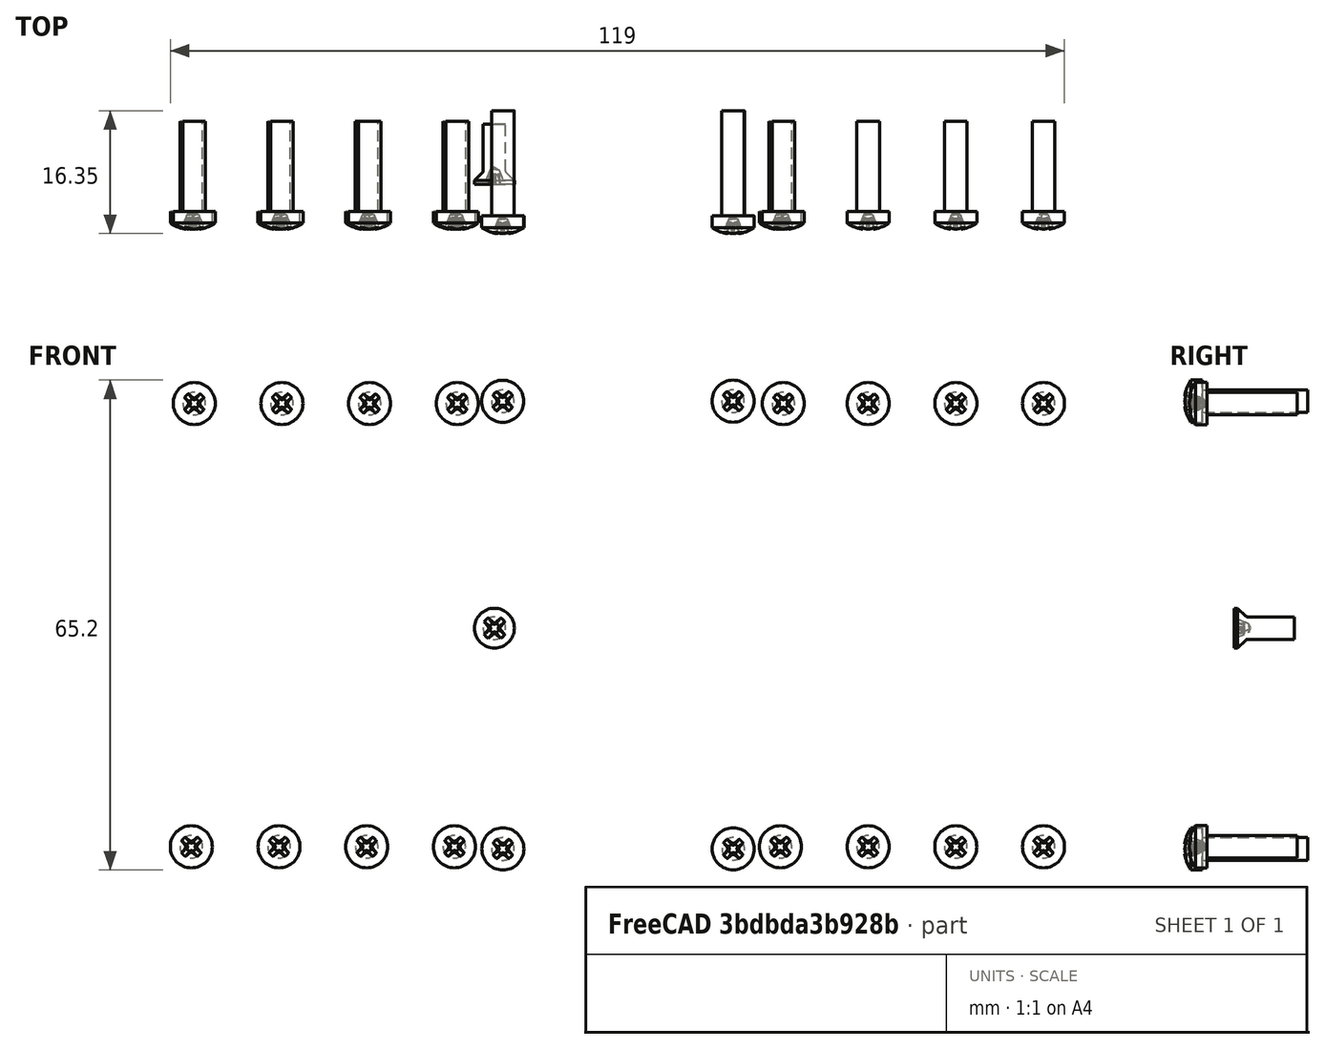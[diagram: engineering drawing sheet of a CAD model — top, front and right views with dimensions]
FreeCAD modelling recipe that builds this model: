
FCSTD DOCUMENT  (FreeCAD 0.19R24291 (Git))
Label: ESC
License: Creative Commons Attribution-NonCommercial-ShareAlike
LicenseURL: http://creativecommons.org/licenses/by-nc-sa/4.0/
objects: Part::FeaturePython×21, App::Link×12, App::DocumentObjectGroup×2, PartDesign::CoordinateSystem×1, App::FeaturePython×1, App::Part×1
note: 22 computed .brp shape members not serialized (recipe doc carries the construction recipe); baked Part::Feature solids carry a one-line shape summary decoded from their .brp
EXTERNAL_REF file=heatsink.FCStd obj=Part
EXTERNAL_REF file=heatsink.FCStd obj=LCS_1
EXTERNAL_REF file=switches.FCStd obj=LCS_0
EXTERNAL_REF file=switches.FCStd obj=Part
EXTERNAL_REF file=busbars.FCStd obj=HoleAxis_7
EXTERNAL_REF file=switches.FCStd obj=HoleAxis_10
EXTERNAL_REF file=busbars.FCStd obj=Body
EXTERNAL_REF file=switches.FCStd obj=HoleAxis_28
EXTERNAL_REF file=busbars.FCStd obj=HoleAxis_6
EXTERNAL_REF file=switches.FCStd obj=HoleAxis_15
EXTERNAL_REF file=busbars.FCStd obj=Body001
EXTERNAL_REF file=switches.FCStd obj=HoleAxis_14
EXTERNAL_REF file=controle.FCStd obj=HoleAxis_1
EXTERNAL_REF file=support1.FCStd obj=HoleAxis_5
EXTERNAL_REF file=controle.FCStd obj=Part
EXTERNAL_REF file=busbars.FCStd obj=HoleAxis_11
EXTERNAL_REF file=caps.FCStd obj=HoleAxis_2
EXTERNAL_REF file=caps.FCStd obj=Part
EXTERNAL_REF file=busbars.FCStd obj=HoleAxis_16
EXTERNAL_REF file=caps.FCStd obj=HoleAxis_4
EXTERNAL_REF file=caps.FCStd obj=HoleAxis_5
EXTERNAL_REF file=caps.FCStd obj=HoleAxis_6
EXTERNAL_REF file=caps.FCStd obj=HoleAxis_7
EXTERNAL_REF file=support1.FCStd obj=HoleAxis_10
EXTERNAL_REF file=support1.FCStd obj=Part
EXTERNAL_REF file=support1.FCStd obj=HoleAxis_11
EXTERNAL_REF file=support1.FCStd obj=HoleAxis_9
EXTERNAL_REF file=support1.FCStd obj=HoleAxis_2
EXTERNAL_REF file=support1.FCStd obj=HoleAxis_1
EXTERNAL_REF file=support1.FCStd obj=HoleAxis_3
EXTERNAL_REF file=support1.FCStd obj=HoleAxis_7
EXTERNAL_REF file=support1.FCStd obj=HoleAxis_4
EXTERNAL_REF file=support1.FCStd obj=HoleAxis_8
EXTERNAL_REF file=controle.FCStd obj=HoleAxis_2
EXTERNAL_REF file=controle.FCStd obj=HoleAxis_3
EXTERNAL_REF file=controle.FCStd obj=HoleAxis_4
EXTERNAL_REF file=busbars.FCStd obj=LCS_0
EXTERNAL_REF file=busbars.FCStd obj=insulator

FEATURE [PartDesign::CoordinateSystem] LCS_Origin
  AttacherType = Attacher::AttachEngine3D
  MapMode = 2
  Support = -> [X_Axis]
FEATURE [App::DocumentObjectGroup] Constraints
FEATURE [App::FeaturePython] Variables  # WARN: FeaturePython — macro-defined, semantics opaque (R4)
FEATURE [App::Link] heatsink_Part
  LinkedObject = -> <external heatsink.FCStd>#Part
FEATURE [App::Link] Switches_Part
  AssemblyType = Asm4EE
  AttachedBy = #LCS_0
  AttachedTo = heatsink_Part#LCS_1
  AttachmentOffset = pos=(87.5,1,0) rot=(-0.57735,-0.57735,-0.57735;2.0944rad)
  LinkPlacement = pos=(-55.0308,-40.4035,87.5) rot=(1,0,0;1.5708rad)
  LinkedObject = -> <external switches.FCStd>#Part
  Placement = pos=(-55.0308,-40.4035,87.5) rot=(1,0,0;1.5708rad)
  expr: Placement = heatsink_Part.Placement * heatsink#LCS_1.Placement * AttachmentOffset * switches#LCS_0.Placement ^ -1
FEATURE [App::Link] busbars_bar1_Body
  AssemblyType = Asm4EE
  AttachedBy = #HoleAxis_7
  AttachedTo = Switches_Part#HoleAxis_10
  AttachmentOffset = pos=(0,0,3) rot=(0,0,1;4.71239rad)
  LinkPlacement = pos=(5.01916,-40.2035,84.31) rot=(-0.57735,-0.57735,0.57735;4.18879rad)
  LinkedObject = -> <external busbars.FCStd>#Body
  Placement = pos=(5.01916,-40.2035,84.31) rot=(-0.57735,-0.57735,0.57735;4.18879rad)
  expr: Placement = Switches_Part.Placement * switches#HoleAxis_10.Placement * AttachmentOffset * busbars#HoleAxis_7.Placement ^ -1
FEATURE [App::Link] busbars_bar1_Body001
  AssemblyType = Asm4EE
  AttachedBy = #HoleAxis_7
  AttachedTo = Switches_Part#HoleAxis_28
  AttachmentOffset = pos=(0,0,3) rot=(0,0,-1;4.71239rad)
  LinkPlacement = pos=(4.91916,-40.2035,15.69) rot=(-0.57735,0.57735,-0.57735;4.18879rad)
  LinkedObject = -> <external busbars.FCStd>#Body
  Placement = pos=(4.91916,-40.2035,15.69) rot=(-0.57735,0.57735,-0.57735;4.18879rad)
  expr: Placement = Switches_Part.Placement * switches#HoleAxis_28.Placement * AttachmentOffset * busbars#HoleAxis_7.Placement ^ -1
FEATURE [App::Link] busbars_bar2_body
  AssemblyType = Asm4EE
  AttachedBy = #HoleAxis_6
  AttachedTo = Switches_Part#HoleAxis_15
  AttachmentOffset = pos=(0,0,3) rot=(0,0,1;4.71239rad)
  LinkPlacement = pos=(-54.6308,-40.2035,79.6) rot=(-0.57735,-0.57735,0.57735;4.18879rad)
  LinkedObject = -> <external busbars.FCStd>#Body001
  Placement = pos=(-54.6308,-40.2035,79.6) rot=(-0.57735,-0.57735,0.57735;4.18879rad)
  expr: Placement = Switches_Part.Placement * switches#HoleAxis_15.Placement * AttachmentOffset * busbars#HoleAxis_6.Placement ^ -1
FEATURE [App::Link] busbars_bar2_body001
  AssemblyType = Asm4EE
  AttachedBy = #HoleAxis_6
  AttachedTo = Switches_Part#HoleAxis_14
  AttachmentOffset = pos=(0,0,3) rot=(0,0,1;1.5708rad)
  LinkPlacement = pos=(64.5692,-40.2035,19.66) rot=(0.57735,-0.57735,0.57735;2.0944rad)
  LinkedObject = -> <external busbars.FCStd>#Body001
  Placement = pos=(64.5692,-40.2035,19.66) rot=(0.57735,-0.57735,0.57735;2.0944rad)
  expr: Placement = Switches_Part.Placement * switches#HoleAxis_14.Placement * AttachmentOffset * busbars#HoleAxis_6.Placement ^ -1
FEATURE [App::Link] Controle_Part
  AssemblyType = Asm4EE
  AttachedBy = #HoleAxis_1
  AttachedTo = support1_Part#HoleAxis_5
  AttachmentOffset = pos=(0.35,0,1.6) rot=(0,0,-1;1.5708rad)
  LinkPlacement = pos=(23.6658,-47.6035,17.45) rot=(-0.57735,0.57735,-0.57735;4.18879rad)
  LinkedObject = -> <external controle.FCStd>#Part
  Placement = pos=(23.6658,-47.6035,17.45) rot=(-0.57735,0.57735,-0.57735;4.18879rad)
  expr: Placement = support1_Part.Placement * support1#HoleAxis_5.Placement * AttachmentOffset * controle#HoleAxis_1.Placement ^ -1
FEATURE [App::Link] Caps_Part
  AssemblyType = Asm4EE
  AttachedBy = #HoleAxis_2
  AttachedTo = busbars_bar1_Body#HoleAxis_11
  AttachmentOffset = pos=(0,0,-1.6) rot=(0,-1,0;3.14159rad)
  LinkPlacement = pos=(-55.0342,-45.0035,12.5) rot=(-0.57735,0.57735,-0.57735;4.18879rad)
  LinkedObject = -> <external caps.FCStd>#Part
  Placement = pos=(-55.0342,-45.0035,12.5) rot=(-0.57735,0.57735,-0.57735;4.18879rad)
  expr: Placement = busbars_bar1_Body.Placement * busbars#HoleAxis_11.Placement * AttachmentOffset * caps#HoleAxis_2.Placement ^ -1
FEATURE [App::Link] Caps_Part001
  AssemblyType = Asm4EE
  AttachedBy = #HoleAxis_4
  AttachedTo = busbars_bar1_Body001#HoleAxis_16
  AttachmentOffset = pos=(0,0,-1.6) rot=(0,-1,0;3.14159rad)
  LinkPlacement = pos=(64.9792,-45.0035,87.5) rot=(0.57735,0.57735,-0.57735;2.0944rad)
  LinkedObject = -> <external caps.FCStd>#Part
  Placement = pos=(64.9792,-45.0035,87.5) rot=(0.57735,0.57735,-0.57735;2.0944rad)
  expr: Placement = busbars_bar1_Body001.Placement * busbars#HoleAxis_16.Placement * AttachmentOffset * caps#HoleAxis_4.Placement ^ -1
FEATURE [Part::FeaturePython] Screw  label="M3x12-Screw1523"  # Fasteners workbench fastener (typed FeaturePython)
  AssemblyType = Asm4EE
  AttachedBy = Origin
  AttachedTo = Caps_Part001#HoleAxis_5
  AttachmentOffset = pos=(0,0,2) rot=(0,0,-1;1.5708rad)
  Placement = pos=(61.4792,-47.0035,79.5) rot=(0,0.707107,-0.707107;3.14159rad)
  diameter = 4
  invert = false
  length = 5
  lengthCustom = 12
  matchOuter = false
  offset = 0
  thread = false
  type = 34
  expr: Placement = Caps_Part001.Placement * caps#HoleAxis_5.Placement * AttachmentOffset
FEATURE [Part::FeaturePython] Screw001  label="M3x12-Screw"  # Fasteners workbench fastener (typed FeaturePython)
  AssemblyType = Asm4EE
  AttachedBy = Origin
  AttachedTo = Caps_Part001#HoleAxis_6
  AttachmentOffset = pos=(0,0,2) rot=(0,0,1;0rad)
  Placement = pos=(49.8125,-47.0035,79.5) rot=(0.57735,0.57735,-0.57735;2.0944rad)
  diameter = 4
  invert = false
  length = 5
  lengthCustom = 12
  matchOuter = false
  offset = 0
  thread = false
  type = 34
  expr: Placement = Caps_Part001.Placement * caps#HoleAxis_6.Placement * AttachmentOffset
FEATURE [Part::FeaturePython] Screw002  label="M3x12-Screw1524"  # Fasteners workbench fastener (typed FeaturePython)
  AssemblyType = Asm4EE
  AttachedBy = Origin
  AttachedTo = Caps_Part001#HoleAxis_7
  AttachmentOffset = pos=(0,0,2) rot=(0,0,1;0rad)
  Placement = pos=(38.1458,-47.0035,79.5) rot=(0.57735,0.57735,-0.57735;2.0944rad)
  diameter = 4
  invert = false
  length = 5
  lengthCustom = 12
  matchOuter = false
  offset = 0
  thread = false
  type = 34
  expr: Placement = Caps_Part001.Placement * caps#HoleAxis_7.Placement * AttachmentOffset
FEATURE [App::Link] support1_Part
  AssemblyType = Asm4EE
  AttachedBy = #HoleAxis_1
  AttachedTo = Caps_Part#HoleAxis_4
  AttachmentOffset = pos=(0,0,2) rot=(0,0,1;1.5708rad)
  LinkPlacement = pos=(-12.8342,-47.0035,89.5) rot=(0,0.707107,-0.707107;3.14159rad)
  LinkedObject = -> <external support1.FCStd>#Part
  Placement = pos=(-12.8342,-47.0035,89.5) rot=(0,0.707107,-0.707107;3.14159rad)
  expr: Placement = Caps_Part.Placement * caps#HoleAxis_4.Placement * AttachmentOffset * support1#HoleAxis_10.Placement ^ -1
FEATURE [App::Link] support1_Part001
  AssemblyType = Asm4EE
  AttachedBy = #HoleAxis_10
  AttachedTo = Caps_Part001#HoleAxis_4
  AttachmentOffset = pos=(0,0,2) rot=(0,0,1;1.5708rad)
  LinkPlacement = pos=(22.7792,-47.0035,10.5) rot=(1,0,0;1.5708rad)
  LinkedObject = -> <external support1.FCStd>#Part
  Placement = pos=(22.7792,-47.0035,10.5) rot=(1,0,0;1.5708rad)
  expr: Placement = Caps_Part001.Placement * caps#HoleAxis_4.Placement * AttachmentOffset * support1#HoleAxis_10.Placement ^ -1
FEATURE [Part::FeaturePython] Screw005  label="M3x12-Screw1536"  # Fasteners workbench fastener (typed FeaturePython)
  AssemblyType = Asm4EE
  AttachedBy = Origin
  AttachedTo = support1_Part#HoleAxis_11
  Placement = pos=(-51.5342,-47.0035,79.5) rot=(0,0.707107,-0.707107;3.14159rad)
  diameter = 4
  invert = false
  length = 5
  lengthCustom = 12
  matchOuter = false
  offset = 0
  thread = false
  type = 34
  expr: Placement = support1_Part.Placement * support1#HoleAxis_11.Placement * AttachmentOffset
FEATURE [Part::FeaturePython] Screw006  label="M3x12-Screw1533"  # Fasteners workbench fastener (typed FeaturePython)
  AssemblyType = Asm4EE
  AttachedBy = Origin
  AttachedTo = support1_Part#HoleAxis_9
  Placement = pos=(-16.5242,-47.0035,79.5) rot=(0,0.707107,-0.707107;3.14159rad)
  diameter = 4
  invert = false
  length = 5
  lengthCustom = 12
  matchOuter = false
  offset = 0
  thread = false
  type = 34
  expr: Placement = support1_Part.Placement * support1#HoleAxis_9.Placement * AttachmentOffset
FEATURE [Part::FeaturePython] Screw007  label="M3x12-Screw1530"  # Fasteners workbench fastener (typed FeaturePython)
  AssemblyType = Asm4EE
  AttachedBy = Origin
  AttachedTo = support1_Part001#HoleAxis_2
  Placement = pos=(-40.2508,-47.0035,20.5) rot=(1,0,0;1.5708rad)
  diameter = 4
  invert = false
  length = 5
  lengthCustom = 12
  matchOuter = false
  offset = 0
  thread = false
  type = 34
  expr: Placement = support1_Part001.Placement * support1#HoleAxis_2.Placement * AttachmentOffset
FEATURE [Part::FeaturePython] Screw008  label="M3x12-Screw1531"  # Fasteners workbench fastener (typed FeaturePython)
  AssemblyType = Asm4EE
  AttachedBy = Origin
  AttachedTo = support1_Part001#HoleAxis_1
  Placement = pos=(-51.9208,-47.0035,20.5) rot=(1,0,0;1.5708rad)
  diameter = 4
  invert = false
  length = 5
  lengthCustom = 12
  matchOuter = false
  offset = 0
  thread = false
  type = 34
  expr: Placement = support1_Part001.Placement * support1#HoleAxis_1.Placement * AttachmentOffset
FEATURE [Part::FeaturePython] Screw009  label="M3x12-Screw1525"  # Fasteners workbench fastener (typed FeaturePython)
  AssemblyType = Asm4EE
  AttachedBy = Origin
  AttachedTo = support1_Part001#HoleAxis_3
  Placement = pos=(-28.5808,-47.0035,20.5) rot=(1,0,0;1.5708rad)
  diameter = 4
  invert = false
  length = 5
  lengthCustom = 12
  matchOuter = false
  offset = 0
  thread = false
  type = 34
  expr: Placement = support1_Part001.Placement * support1#HoleAxis_3.Placement * AttachmentOffset
FEATURE [Part::FeaturePython] Screw010  label="M3x12-Screw1537"  # Fasteners workbench fastener (typed FeaturePython)
  AssemblyType = Asm4EE
  AttachedBy = Origin
  AttachedTo = support1_Part#HoleAxis_7
  Placement = pos=(-28.1942,-47.0035,79.5) rot=(0.57735,0.57735,-0.57735;2.0944rad)
  diameter = 4
  invert = false
  length = 5
  lengthCustom = 12
  matchOuter = false
  offset = 0
  thread = false
  type = 34
  expr: Placement = support1_Part.Placement * support1#HoleAxis_7.Placement * AttachmentOffset
FEATURE [Part::FeaturePython] Screw011  label="M3x12-Screw1532"  # Fasteners workbench fastener (typed FeaturePython)
  AssemblyType = Asm4EE
  AttachedBy = Origin
  AttachedTo = support1_Part001#HoleAxis_4
  Placement = pos=(-16.9108,-47.0035,20.5) rot=(1,0,0;1.5708rad)
  diameter = 4
  invert = false
  length = 5
  lengthCustom = 12
  matchOuter = false
  offset = 0
  thread = false
  type = 34
  expr: Placement = support1_Part001.Placement * support1#HoleAxis_4.Placement * AttachmentOffset
FEATURE [Part::FeaturePython] Screw012  label="M3x12-Screw1527"  # Fasteners workbench fastener (typed FeaturePython)
  AssemblyType = Asm4EE
  AttachedBy = Origin
  AttachedTo = support1_Part001#HoleAxis_7
  Placement = pos=(38.1392,-47.0035,20.5) rot=(0.57735,-0.57735,0.57735;2.0944rad)
  diameter = 4
  invert = false
  length = 5
  lengthCustom = 12
  matchOuter = false
  offset = 0
  thread = false
  type = 34
  expr: Placement = support1_Part001.Placement * support1#HoleAxis_7.Placement * AttachmentOffset
FEATURE [Part::FeaturePython] Screw013  label="M3x12-Screw1526"  # Fasteners workbench fastener (typed FeaturePython)
  AssemblyType = Asm4EE
  AttachedBy = Origin
  AttachedTo = support1_Part001#HoleAxis_8
  Placement = pos=(49.8092,-47.0035,20.5) rot=(1,0,0;1.5708rad)
  diameter = 4
  invert = false
  length = 5
  lengthCustom = 12
  matchOuter = false
  offset = 0
  thread = false
  type = 34
  expr: Placement = support1_Part001.Placement * support1#HoleAxis_8.Placement * AttachmentOffset
FEATURE [Part::FeaturePython] Screw014  label="M3x12-Screw1535"  # Fasteners workbench fastener (typed FeaturePython)
  AssemblyType = Asm4EE
  AttachedBy = Origin
  AttachedTo = support1_Part#HoleAxis_8
  Placement = pos=(-39.8642,-47.0035,79.5) rot=(0,0.707107,-0.707107;3.14159rad)
  diameter = 4
  invert = false
  length = 5
  lengthCustom = 12
  matchOuter = false
  offset = 0
  thread = false
  type = 34
  expr: Placement = support1_Part.Placement * support1#HoleAxis_8.Placement * AttachmentOffset
FEATURE [Part::FeaturePython] Screw015  label="M3x12-Screw1528"  # Fasteners workbench fastener (typed FeaturePython)
  AssemblyType = Asm4EE
  AttachedBy = Origin
  AttachedTo = support1_Part001#HoleAxis_9
  Placement = pos=(26.4692,-47.0035,20.5) rot=(1,0,0;1.5708rad)
  diameter = 4
  invert = false
  length = 5
  lengthCustom = 12
  matchOuter = false
  offset = 0
  thread = false
  type = 34
  expr: Placement = support1_Part001.Placement * support1#HoleAxis_9.Placement * AttachmentOffset
FEATURE [Part::FeaturePython] Screw016  label="M3x12-Screw1529"  # Fasteners workbench fastener (typed FeaturePython)
  AssemblyType = Asm4EE
  AttachedBy = Origin
  AttachedTo = support1_Part001#HoleAxis_11
  Placement = pos=(61.4792,-47.0035,20.5) rot=(1,0,0;1.5708rad)
  diameter = 4
  invert = false
  length = 5
  lengthCustom = 12
  matchOuter = false
  offset = 0
  thread = false
  type = 34
  expr: Placement = support1_Part001.Placement * support1#HoleAxis_11.Placement * AttachmentOffset
FEATURE [Part::FeaturePython] Screw017  label="M3x12-Screw1534"  # Fasteners workbench fastener (typed FeaturePython)
  AssemblyType = Asm4EE
  AttachedBy = Origin
  AttachedTo = support1_Part#HoleAxis_4
  Placement = pos=(26.8558,-47.0035,79.5) rot=(0,0.707107,-0.707107;3.14159rad)
  diameter = 4
  invert = false
  length = 5
  lengthCustom = 12
  matchOuter = false
  offset = 0
  thread = false
  type = 34
  expr: Placement = support1_Part.Placement * support1#HoleAxis_4.Placement * AttachmentOffset
FEATURE [Part::FeaturePython] Screw018  label="M3x14-Screw"  # Fasteners workbench fastener (typed FeaturePython)
  AssemblyType = Asm4EE
  AttachedBy = Origin
  AttachedTo = Controle_Part#HoleAxis_1
  Placement = pos=(-10.4842,-47.6035,79.8) rot=(-0.57735,0.57735,-0.57735;4.18879rad)
  diameter = 4
  invert = false
  length = 6
  lengthCustom = 14
  matchOuter = false
  offset = 0
  thread = false
  type = 34
  expr: Placement = Controle_Part.Placement * controle#HoleAxis_1.Placement * AttachmentOffset
FEATURE [Part::FeaturePython] Screw019  label="M3x14-Screw118"  # Fasteners workbench fastener (typed FeaturePython)
  AssemblyType = Asm4EE
  AttachedBy = Origin
  AttachedTo = Controle_Part#HoleAxis_2
  Placement = pos=(-10.4608,-47.6035,20.2104) rot=(-0.57735,0.57735,-0.57735;4.18879rad)
  diameter = 4
  invert = false
  length = 6
  lengthCustom = 14
  matchOuter = false
  offset = 0
  thread = false
  type = 34
  expr: Placement = Controle_Part.Placement * controle#HoleAxis_2.Placement * AttachmentOffset
FEATURE [Part::FeaturePython] Screw020  label="M3x14-Screw119"  # Fasteners workbench fastener (typed FeaturePython)
  AssemblyType = Asm4EE
  AttachedBy = Origin
  AttachedTo = Controle_Part#HoleAxis_3
  Placement = pos=(20.1898,-47.6035,20.2235) rot=(-0.57735,0.57735,-0.57735;4.18879rad)
  diameter = 4
  invert = false
  length = 6
  lengthCustom = 14
  matchOuter = false
  offset = 0
  thread = false
  type = 34
  expr: Placement = Controle_Part.Placement * controle#HoleAxis_3.Placement * AttachmentOffset
FEATURE [Part::FeaturePython] Screw021  label="M3x14-Screw120"  # Fasteners workbench fastener (typed FeaturePython)
  AssemblyType = Asm4EE
  AttachedBy = Origin
  AttachedTo = Controle_Part#HoleAxis_4
  Placement = pos=(20.1658,-47.6035,79.8121) rot=(-0.57735,0.57735,-0.57735;4.18879rad)
  diameter = 4
  invert = false
  length = 6
  lengthCustom = 14
  matchOuter = false
  offset = 0
  thread = false
  type = 34
  expr: Placement = Controle_Part.Placement * controle#HoleAxis_4.Placement * AttachmentOffset
FEATURE [App::Link] busbars_insulator
  AssemblyType = Asm4EE
  AttachedBy = #LCS_0
  AttachedTo = busbars_bar2_body#HoleAxis_6
  AttachmentOffset = pos=(0,0,-2) rot=(0,0,1;0rad)
  LinkPlacement = pos=(-11.5808,-41.4035,49.6) rot=(-0.57735,-0.57735,0.57735;4.18879rad)
  LinkedObject = -> <external busbars.FCStd>#insulator
  Placement = pos=(-11.5808,-41.4035,49.6) rot=(-0.57735,-0.57735,0.57735;4.18879rad)
  expr: Placement = busbars_bar2_body.Placement * busbars#HoleAxis_6.Placement * AttachmentOffset * busbars#LCS_0.Placement ^ -1
FEATURE [Part::FeaturePython] Screw022  label="M3x8-Screw"  # Fasteners workbench fastener (typed FeaturePython)
  AssemblyType = Asm4EE
  AttachedBy = Origin
  AttachedTo = busbars_bar2_body#HoleAxis_6
  Placement = pos=(-11.5808,-43.4035,49.6) rot=(-0.57735,-0.57735,0.57735;4.18879rad)
  diameter = 4
  invert = false
  length = 3
  lengthCustom = 8
  matchOuter = false
  offset = 0
  thread = false
  type = 35
  expr: Placement = busbars_bar2_body.Placement * busbars#HoleAxis_6.Placement * AttachmentOffset
FEATURE [App::DocumentObjectGroup] Group  label="Screws"
  Group = -> [Screw016,Screw015,Screw013,Screw012,Screw011,Screw009,Screw007,Screw008,Screw005,Screw014,Screw006,Screw010,Screw017,Screw,Screw002,Screw001,Screw018,Screw019,Screw020,Screw021,Screw022]
FEATURE [App::Part] Model
  Configuration = 0
  Group = -> [LCS_Origin,Constraints,Variables,heatsink_Part,Switches_Part,busbars_bar1_Body,busbars_bar1_Body001,busbars_bar2_body,busbars_bar2_body001,Controle_Part,Caps_Part,Caps_Part001,support1_Part,support1_Part001,Screw001,Screw,Screw002,Screw006,Screw009,Screw013,Screw012,Screw015,Screw016,Screw017,Screw007,Screw014,Screw005,Screw010,Screw008,Screw011,Group,Screw018,Screw019,Screw020,Screw021,+2 more]
  Origin = -> Origin
  Placement = pos=(0,0,0) rot=(1,0,0;-1.5708rad)
  Type = Assembly4 Model

RESOLVED EXTERNAL PARTS (link-assembly join: the EXTERNAL_REF files above that resolve inside this repo's crawl, each included once):
---- part busbars.FCStd = doc fcstd_a403adba0c2a ----
FCSTD DOCUMENT  (FreeCAD 0.19R24291 (Git))
Label: busbars
License: All rights reserved
LicenseURL: http://en.wikipedia.org/wiki/All_rights_reserved
objects: TechDraw::DrawViewDimension×44, Part::Cylinder×18, PartDesign::Line×18, Part::Fuse×7, TechDraw::DrawProjGroupItem×6, Part::Box×5, Part::Cut×5, Part::MultiFuse×4, Sketcher::SketchObject×3, PartDesign::CoordinateSystem×3, PartDesign::Hole×3, PartDesign::Body×3, Part::Part2DObjectPython×2, PartDesign::Pad×2, TechDraw::DrawProjGroup×2, App::DocumentObjectGroup×2, TechDraw::DrawViewPart×2, Part::FeaturePython×2, Part::Mirroring×1, TechDraw::DrawSVGTemplate×1, +4 more types
note: 82 computed .brp shape members not serialized (recipe doc carries the construction recipe); baked Part::Feature solids carry a one-line shape summary decoded from their .brp

FEATURE [Part::Box] cube
  AttacherType = Attacher::AttachEngine3D
  Height = 3
  Length = 10
  Width = 60
FEATURE [Part::Cylinder] cylinder
  Angle = 360
  AttacherType = Attacher::AttachEngine3D
  Height = 5
  Placement = pos=(4.81,56.54,-1) rot=(0,0,1;0rad)
  Radius = 1.6
FEATURE [Part::Cylinder] cylinder001
  Angle = 360
  AttacherType = Attacher::AttachEngine3D
  Height = 5
  Placement = pos=(4.81,44.87,-1) rot=(0,0,1;0rad)
  Radius = 1.6
FEATURE [Part::Cylinder] cylinder002
  Angle = 360
  AttacherType = Attacher::AttachEngine3D
  Height = 5
  Placement = pos=(4.81,33.2,-1) rot=(0,0,1;0rad)
  Radius = 1.6
FEATURE [Part::Cylinder] cylinder003
  Angle = 360
  AttacherType = Attacher::AttachEngine3D
  Height = 5
  Placement = pos=(4.81,21.53,-1) rot=(0,0,1;0rad)
  Radius = 1.6
FEATURE [Part::MultiFuse] Group
  Shapes = -> [cylinder,cylinder001,cylinder002,cylinder003]
FEATURE [Part::Cylinder] cylinder004
  Angle = 360
  AttacherType = Attacher::AttachEngine3D
  Height = 5
  Placement = pos=(4.52,15.3,-1) rot=(0,0,1;0rad)
  Radius = 1.6
FEATURE [Part::Fuse] union
  Base = -> Group
  Tool = -> cylinder004
FEATURE [Part::Cut] difference
  Base = -> cube
  Tool = -> union
FEATURE [Part::Box] cube001
  AttacherType = Attacher::AttachEngine3D
  Height = 3
  Length = 10
  Width = 60
FEATURE [Part::Cylinder] cylinder005 .. cylinder008  x4 (patterned run collapsed; names and placements below)
  Angle = 360
  AttacherType = Attacher::AttachEngine3D
  Height = 5
  Radius = 1.6
  placements: 4 in arithmetic series — first pos=(4.81,56.54,-1) rot=(0,0,1;0rad), step (0,-11.67,0), last pos=(4.81,21.53,-1) rot=(0,0,1;0rad)
FEATURE [Part::MultiFuse] Group001
  Shapes = -> [cylinder005,cylinder006,cylinder007,cylinder008]
FEATURE [Part::Cylinder] cylinder009
  Angle = 360
  AttacherType = Attacher::AttachEngine3D
  Height = 5
  Placement = pos=(4.52,15.3,-1) rot=(0,0,1;0rad)
  Radius = 1.6
FEATURE [Part::Fuse] union001
  Base = -> Group001
  Tool = -> cylinder009
FEATURE [Part::Cut] difference001
  Base = -> cube001
  Tool = -> union001
FEATURE [Part::Mirroring] mirr_difference001  label="mirrored difference001"
  Base = (0,0,0)
  Normal = (0,1,0)
  Source = -> difference001
FEATURE [Part::Fuse] Group002
  Base = -> difference
  Tool = -> mirr_difference001
FEATURE [Part::Box] cube002
  AttacherType = Attacher::AttachEngine3D
  Height = 3
  Length = 10
  Placement = pos=(0,-80,0) rot=(0,0,1;0rad)
  Width = 20
FEATURE [Part::Cylinder] cylinder010
  Angle = 360
  AttacherType = Attacher::AttachEngine3D
  Height = 5
  Placement = pos=(5,-76,-1) rot=(0,0,1;0rad)
  Radius = 2.1
FEATURE [Part::Cylinder] cylinder011
  Angle = 360
  AttacherType = Attacher::AttachEngine3D
  Height = 5
  Placement = pos=(5,-68,-1) rot=(0,0,1;0rad)
  Radius = 2.1
FEATURE [Part::Fuse] union002
  Base = -> cylinder010
  Tool = -> cylinder011
FEATURE [Part::Cut] difference002
  Base = -> cube002
  Tool = -> union002
FEATURE [Part::Fuse] union003  label="bar1_fromOpenScad"
  Base = -> Group002
  Tool = -> difference002
FEATURE [Part::Box] cube003
  AttacherType = Attacher::AttachEngine3D
  Height = 3
  Length = 10
  Width = 60
FEATURE [Part::Cylinder] cylinder012 .. cylinder015  x4 (patterned run collapsed; names and placements below)
  Angle = 360
  AttacherType = Attacher::AttachEngine3D
  Height = 5
  Radius = 1.6
  placements: 4 in arithmetic series — first pos=(5,8.86,-1) rot=(0,0,1;0rad), step (0,13.8925,0), last pos=(5,50.5375,-1) rot=(0,0,1;0rad)
FEATURE [Part::MultiFuse] Group003
  Shapes = -> [cylinder012,cylinder013,cylinder014,cylinder015]
FEATURE [Part::Cut] difference003
  Base = -> cube003
  Tool = -> Group003
FEATURE [Part::Box] cube004
  AttacherType = Attacher::AttachEngine3D
  Height = 3
  Length = 10
  Placement = pos=(0,-20,0) rot=(0,0,1;0rad)
  Width = 20
FEATURE [Part::Cylinder] cylinder016
  Angle = 360
  AttacherType = Attacher::AttachEngine3D
  Height = 5
  Placement = pos=(5,-16,-1) rot=(0,0,1;0rad)
  Radius = 2.1
FEATURE [Part::Cylinder] cylinder017
  Angle = 360
  AttacherType = Attacher::AttachEngine3D
  Height = 5
  Placement = pos=(5,-8,-1) rot=(0,0,1;0rad)
  Radius = 2.1
FEATURE [Part::Fuse] union004
  Base = -> cylinder016
  Tool = -> cylinder017
FEATURE [Part::Cut] difference004
  Base = -> cube004
  Tool = -> union004
FEATURE [Part::Fuse] union005  label="bar2_fromOpenScad"
  Base = -> difference003
  Placement = pos=(25,0,0) rot=(0,0,1;0rad)
  Tool = -> difference004
FEATURE [TechDraw::DrawSVGTemplate] Template
  EditableTexts = APPROVER_NAME=APPROVER NAME,AUTHOR_NAME=AUTHOR NAME,DATE=YYYY-MM-DD,DN=DN,DOCUMENT_TYPE=Mechanical assembly drawing,OWNER_NAME=OWNER NAME,PM=PM,PN=PN,+7 more (map truncated)
  Height = 297
  Orientation = 1
  Width = 420
FEATURE [Part::Part2DObjectPython] Shape2DView  label="bar1_Shape2DView"  # Draft 2D object (typed FeaturePython)
  Base = -> union003
  FuseArch = false
  HiddenLines = false
  InPlace = true
  Projection = (0,0,1)
  ProjectionMode = 0
  SegmentLength = 0.05
  Tessellation = false
  VisibleOnly = false
FEATURE [Sketcher::SketchObject] Sketch  label="bar1_Sketch"
  FullyConstrained = true
  expr: Constraints[47] = Spreadsheet.varH
  expr: Constraints[46] = 2 * Spreadsheet.tab / 5
  expr: Constraints[33] = Spreadsheet.varA
  expr: Constraints[20] = Spreadsheet.varD
  expr: Constraints[45] = Spreadsheet.tab / 5
  expr: Constraints[34] = Spreadsheet.varA
  expr: Constraints[36] = Spreadsheet.varC
  expr: Constraints[41] = Spreadsheet.varE
  expr: Constraints[40] = Spreadsheet.varE
  expr: Constraints[39] = Spreadsheet.varD
  expr: Constraints[37] = Spreadsheet.varC
  expr: Constraints[35] = Spreadsheet.varA
  expr: Constraints[31] = Spreadsheet.varA
  expr: Constraints[25] = Spreadsheet.lenght1
  expr: Constraints[28] = Spreadsheet.varC
  expr: Constraints[30] = Spreadsheet.varA
  expr: Constraints[8] = Spreadsheet.hole2_diameter
  expr: Constraints[44] = Spreadsheet.width / 2
  expr: Constraints[19] = Spreadsheet.varA
  expr: Constraints[42] = Spreadsheet.varB
  expr: Constraints[7] = Spreadsheet.hole2_diameter
  expr: Constraints[43] = Spreadsheet.width / 2
  expr: Constraints[27] = Spreadsheet.varC
  expr: Constraints[9] = Spreadsheet.hole1_diameter
  expr: Constraints[32] = Spreadsheet.varA
  expr: Constraints[26] = Spreadsheet.varC
  expr: Constraints[3] = Spreadsheet.width
  expr: Constraints[29] = Spreadsheet.varA
  expr: Constraints[38] = Spreadsheet.varC
  sketch-geometry (16):
    g0: LineSegment StartX=0 StartY=60 StartZ=0 EndX=10 EndY=60 EndZ=0
    g1: Circle CenterX=4.52 CenterY=15.32 CenterZ=0 NormalX=0 NormalY=0 NormalZ=1 AngleXU=0 Radius=2
    g2: Circle CenterX=4.81 CenterY=21.54 CenterZ=0 NormalX=0 NormalY=0 NormalZ=1 AngleXU=0 Radius=2
    g3: Circle CenterX=4.81 CenterY=33.21 CenterZ=0 NormalX=0 NormalY=0 NormalZ=1 AngleXU=0 Radius=2
    g4: Circle CenterX=4.81 CenterY=44.88 CenterZ=0 NormalX=0 NormalY=0 NormalZ=1 AngleXU=0 Radius=2
    g5: Circle CenterX=4.81 CenterY=56.55 CenterZ=0 NormalX=0 NormalY=0 NormalZ=1 AngleXU=0 Radius=2
    g6: Circle CenterX=4.52 CenterY=-15.33 CenterZ=0 NormalX=0 NormalY=0 NormalZ=-1 AngleXU=-3.14159 Radius=2
    g7: Circle CenterX=4.81 CenterY=-21.55 CenterZ=0 NormalX=0 NormalY=0 NormalZ=-1 AngleXU=-3.14159 Radius=2
    g8: Circle CenterX=4.81 CenterY=-33.22 CenterZ=0 NormalX=0 NormalY=0 NormalZ=-1 AngleXU=-3.14159 Radius=2
    g9: Circle CenterX=4.81 CenterY=-44.89 CenterZ=0 NormalX=0 NormalY=0 NormalZ=-1 AngleXU=-3.14159 Radius=2
    g10: Circle CenterX=4.81 CenterY=-56.56 CenterZ=0 NormalX=0 NormalY=0 NormalZ=-1 AngleXU=-3.14159 Radius=2
    g11: LineSegment StartX=0 StartY=-80 StartZ=0 EndX=10 EndY=-80 EndZ=0
    g12: Circle CenterX=5 CenterY=-76 CenterZ=0 NormalX=0 NormalY=0 NormalZ=1 AngleXU=0 Radius=2.1
    g13: Circle CenterX=5 CenterY=-68 CenterZ=0 NormalX=0 NormalY=0 NormalZ=1 AngleXU=0 Radius=2.1
    g14: LineSegment StartX=0 StartY=60 StartZ=0 EndX=0 EndY=-80 EndZ=0
    g15: LineSegment StartX=10 StartY=-80 StartZ=0 EndX=10 EndY=60 EndZ=0
  constraints (50):
    c: Horizontal(g11)
    c: Horizontal(g0)
    c: Vertical(g14)
    c: Distance(g11) = 10
    c: Coincident(g11,g14)
    c: DistanceX(g11) = 0
    c: DistanceY(g11) = -80
    c: Diameter(g12) = 4.2
    c: Diameter(g13) = 4.2
    c: Diameter(g10) = 4
    c: Equal(g5,g4)
    c: Equal(g4,g3)
    c: Equal(g3,g2)
    c: Equal(g2,g1)
    c: Equal(g1,g7)
    c: Equal(g7,g6)
    c: Equal(g6,g8)
    c: Equal(g8,g10)
    c: Equal(g9,g10)
    c: Distance(g9,g14) = 4.81
    c: Distance(g6,g14) = 4.52
    c: Vertical(g15)
    c: Coincident(g0,g14)
    c: Coincident(g0,g15)
    c: Coincident(g15,g11)
    c: DistanceY(g11,g0) = 140
    c: DistanceY(g10,g9) = 11.67
    c: DistanceY(g9,g8) = 11.67
    c: DistanceY(g8,g7) = 11.67
    c: Distance(g10,g14) = 4.81
    c: Distance(g8,g14) = 4.81
    c: Distance(g7,g14) = 4.81
    c: Distance(g2,g14) = 4.81
    c: Distance(g3,g14) = 4.81
    c: Distance(g4,g14) = 4.81
    c: Distance(g5,g14) = 4.81
    c: DistanceY(g2,g3) = 11.67
    c: DistanceY(g3,g4) = 11.67
    c: DistanceY(g4,g5) = 11.67
    c: Distance(g1,g14) = 4.52
    c: DistanceY(g7,g6) = 6.22
    c: DistanceY(g1,g2) = 6.22
    c: Distance(g5,g0) = 3.45
    c: Distance(g12,g14) = 5
    c: Distance(g13,g14) = 5
    c: Distance(g12,g11) = 4
    c: DistanceY(g12,g13) = 8
    c: DistanceY(g6,g1) = 30.65
    c: Distance(g10,g11) = 23.44
    c: DistanceY(g13,g10) = 11.44
FEATURE [Part::Part2DObjectPython] Shape2DView001  label="bar2_Shape2DView"  # Draft 2D object (typed FeaturePython)
  Base = -> union005
  FuseArch = false
  HiddenLines = false
  InPlace = true
  Projection = (0,0,1)
  ProjectionMode = 0
  SegmentLength = 0.05
  Tessellation = false
  VisibleOnly = false
FEATURE [Sketcher::SketchObject] Sketch001  label="bar2_Sketch"
  FullyConstrained = true
  expr: Constraints[29] = Spreadsheet.varG
  expr: Constraints[26] = Spreadsheet.width / 2
  expr: Constraints[24] = Spreadsheet.width / 2
  expr: Constraints[28] = Spreadsheet.varG
  expr: Constraints[25] = Spreadsheet.width / 2
  expr: Constraints[21] = Spreadsheet.hole1_diameter
  expr: Constraints[23] = Spreadsheet.width / 2
  expr: Constraints[19] = Spreadsheet.hole1_diameter
  expr: Constraints[18] = Spreadsheet.hole1_diameter
  expr: Constraints[20] = Spreadsheet.hole1_diameter
  expr: Constraints[15] = Spreadsheet.width / 2
  expr: Constraints[13] = 2 * Spreadsheet.tab / 5
  expr: Constraints[12] = Spreadsheet.tab / 5
  expr: Constraints[22] = Spreadsheet.varF
  expr: Constraints[14] = Spreadsheet.width / 2
  expr: Constraints[17] = Spreadsheet.hole2_diameter
  expr: Constraints[9] = Spreadsheet.length2
  expr: Constraints[27] = Spreadsheet.varG
  expr: Constraints[16] = Spreadsheet.hole2_diameter
  expr: Constraints[8] = Spreadsheet.width
  sketch-geometry (10):
    g0: LineSegment StartX=25 StartY=47.5 StartZ=0 EndX=35 EndY=47.5 EndZ=0
    g1: Circle CenterX=30 CenterY=4.05 CenterZ=0 NormalX=0 NormalY=0 NormalZ=1 AngleXU=0 Radius=2
    g2: Circle CenterX=30 CenterY=17.05 CenterZ=0 NormalX=0 NormalY=0 NormalZ=1 AngleXU=0 Radius=2
    g3: Circle CenterX=30 CenterY=30.05 CenterZ=0 NormalX=0 NormalY=0 NormalZ=1 AngleXU=0 Radius=2
    g4: Circle CenterX=30 CenterY=43.05 CenterZ=0 NormalX=0 NormalY=0 NormalZ=1 AngleXU=0 Radius=2
    g5: LineSegment StartX=25 StartY=-20 StartZ=0 EndX=35 EndY=-20 EndZ=0
    g6: Circle CenterX=30 CenterY=-16 CenterZ=0 NormalX=0 NormalY=0 NormalZ=1 AngleXU=0 Radius=2.1
    g7: Circle CenterX=30 CenterY=-8 CenterZ=0 NormalX=0 NormalY=0 NormalZ=1 AngleXU=0 Radius=2.1
    g8: LineSegment StartX=35 StartY=-20 StartZ=0 EndX=35 EndY=47.5 EndZ=0
    g9: LineSegment StartX=25 StartY=47.5 StartZ=0 EndX=25 EndY=-20 EndZ=0
  constraints (32):
    c: Coincident(g8,g0)
    c: Coincident(g0,g9)
    c: Coincident(g9,g5)
    c: Coincident(g5,g8)
    c: Vertical(g8)
    c: Vertical(g9)
    c: Horizontal(g5)
    c: Horizontal(g0)
    c: Distance(g5) = 10
    c: Distance(g9) = 67.5
    c: DistanceX(g5) = 25
    c: DistanceY(g5) = -20
    c: Distance(g6,g5) = 4
    c: DistanceY(g6,g7) = 8
    c: Distance(g7,g9) = 5
    c: Distance(g6,g9) = 5
    c: Diameter(g7) = 4.2
    c: Diameter(g6) = 4.2
    c: Diameter(g1) = 4
    c: Diameter(g2) = 4
    c: Diameter(g3) = 4
    c: Diameter(g4) = 4
    c: Distance(g4,g0) = 4.45
    c: Distance(g1,g9) = 5
    c: Distance(g2,g9) = 5
    c: Distance(g4,g9) = 5
    c: Distance(g3,g9) = 5
    c: Distance(g4,g3) = 13
    c: Distance(g3,g2) = 13
    c: Distance(g1,g2) = 13
    c: Distance(g1,g5) = 24.05
    c: Distance(g7,g1) = 12.05
FEATURE [Spreadsheet::Sheet] Spreadsheet  label="Dimensions"
  cells = A1=Parameter; B1=Value; C1=Description; A2=L1; B2(lenght1)==120mm + tab; C2=Comprimento da barra 1; A3=L2; B3(length2)==50mm + tab - 2.5mm; C3=Comprimento da barra 2; A4=W; B4(width)==10mm; C4=Largura das barras; A5=T; B5(thickness)==3.2mm; C5=Espessura das barras; A6=H1; B6(hole1_diameter)==4mm; C6=Diâmetro interno do furo sem rosca; A7=H2; B7(hole2_diameter)==4.2mm; C7=Furo com rosca M5; A8=A; B8(varA)==4.81mm; C8=Distância entre a borda lateral da barra e centro do furo; A9=B; B9(varB)==3.45mm; A10=C; B10(varC)==11.67mm; A11=D; B11(varD)==4.52mm; C11=Distância entre a borda lateral da barra e centro do furo; A12=E; B12(varE)==6.22mm; A13=F; B13(varF)==4.45mm; C13=Distância entre a borda frontal da barra e centro do furo; A14=G; B14(varG)==13mm; A15=H; B15(varH)==30.65mm; A16=Tab; B16(tab)==20mm
FEATURE [PartDesign::Pad] Pad  label="bar1_Pad"
  Direction = (1,1,1)
  Length = 3.2
  Length2 = 100
  Profile = -> Sketch
  Type = 0
  expr: Length = Spreadsheet.thickness
FEATURE [PartDesign::Pad] Pad001  label="bar2_Pad"
  Direction = (1,1,1)
  Length = 3.2
  Length2 = 100
  Profile = -> Sketch001
  Type = 0
  expr: Length = Spreadsheet.thickness
FEATURE [TechDraw::DrawViewSpreadsheet] Sheet
  CellEnd = B15
  CellStart = A1
  Font = osifont
  LineWidth = 0.35
  LockPosition = false
  Rotation = 0
  ScaleType = 2
  Source = -> Spreadsheet
  Symbol = <blob: 6326 chars omitted>
  TextSize = 12
  X = 376.234
  Y = 116.135
FEATURE [PartDesign::CoordinateSystem] LCS_1
  AttacherType = Attacher::AttachEngine3D
  MapMode = 6
  Placement = pos=(10,60,3.2) rot=(0,0,1;3.14159rad)
  Support = -> [Pad]
FEATURE [PartDesign::CoordinateSystem] LCS_2
  AttacherType = Attacher::AttachEngine3D
  MapMode = 6
  Placement = pos=(35,47.5,3.2) rot=(0,0,1;3.14159rad)
  Support = -> [Pad001]
FEATURE [PartDesign::Line] HoleAxis_1
  AttacherType = Attacher::AttachEngineLine
  Length = 5.91808
  MapMode = 19
  Placement = pos=(30,-8,3.2) rot=(0,0,1;0rad)
  ResizeMode = 1
  Support = -> [Pad001]
FEATURE [PartDesign::Line] HoleAxis_2
  AttacherType = Attacher::AttachEngineLine
  Length = 5.91808
  MapMode = 19
  Placement = pos=(30,-16,3.2) rot=(0,0,1;0rad)
  ResizeMode = 1
  Support = -> [Pad001]
FEATURE [PartDesign::Line] HoleAxis_3
  AttacherType = Attacher::AttachEngineLine
  Length = 5.63627
  MapMode = 19
  Placement = pos=(30,17.05,3.2) rot=(0,0,1;0rad)
  ResizeMode = 1
  Support = -> [Pad001]
FEATURE [PartDesign::Line] HoleAxis_4
  AttacherType = Attacher::AttachEngineLine
  Length = 5.63627
  MapMode = 19
  Placement = pos=(30,30.05,3.2) rot=(0,0,1;0rad)
  ResizeMode = 1
  Support = -> [Pad001]
FEATURE [PartDesign::Line] HoleAxis_5
  AttacherType = Attacher::AttachEngineLine
  Length = 5.63627
  MapMode = 19
  Placement = pos=(30,4.05,3.2) rot=(0,0,1;0rad)
  ResizeMode = 1
  Support = -> [Pad001]
FEATURE [PartDesign::Line] HoleAxis_6
  AttacherType = Attacher::AttachEngineLine
  Length = 5.63627
  MapMode = 19
  Placement = pos=(30,43.05,3.2) rot=(0,0,1;0rad)
  ResizeMode = 1
  Support = -> [Pad001]
FEATURE [PartDesign::Line] HoleAxis_7
  AttacherType = Attacher::AttachEngineLine
  Length = 5.63627
  MapMode = 19
  Placement = pos=(4.81,56.55,3.2) rot=(0,0,1;0rad)
  ResizeMode = 1
  Support = -> [Pad]
FEATURE [PartDesign::Line] HoleAxis_8
  AttacherType = Attacher::AttachEngineLine
  Length = 5.63627
  MapMode = 19
  Placement = pos=(4.81,44.88,3.2) rot=(0,0,1;0rad)
  ResizeMode = 1
  Support = -> [Pad]
FEATURE [PartDesign::Line] HoleAxis_9
  AttacherType = Attacher::AttachEngineLine
  Length = 5.63627
  MapMode = 19
  Placement = pos=(4.81,33.21,3.2) rot=(0,0,1;0rad)
  ResizeMode = 1
  Support = -> [Pad]
FEATURE [PartDesign::Line] HoleAxis_10
  AttacherType = Attacher::AttachEngineLine
  Length = 5.63627
  MapMode = 19
  Placement = pos=(4.52,15.32,3.2) rot=(0,0,1;0rad)
  ResizeMode = 1
  Support = -> [Pad]
FEATURE [PartDesign::Line] HoleAxis_11
  AttacherType = Attacher::AttachEngineLine
  Length = 5.63627
  MapMode = 19
  Placement = pos=(4.81,-33.22,3.2) rot=(-1,0,0;3.14159rad)
  ResizeMode = 1
  Support = -> [Pad]
FEATURE [PartDesign::Line] HoleAxis_12
  AttacherType = Attacher::AttachEngineLine
  Length = 5.63627
  MapMode = 19
  Placement = pos=(4.81,21.54,3.2) rot=(0,0,1;0rad)
  ResizeMode = 1
  Support = -> [Pad]
FEATURE [PartDesign::Line] HoleAxis_13
  AttacherType = Attacher::AttachEngineLine
  Length = 5.63627
  MapMode = 19
  Placement = pos=(4.81,-21.55,3.2) rot=(-1,0,0;3.14159rad)
  ResizeMode = 1
  Support = -> [Pad]
FEATURE [PartDesign::Line] HoleAxis_14
  AttacherType = Attacher::AttachEngineLine
  Length = 5.63627
  MapMode = 19
  Placement = pos=(4.52,-15.33,3.2) rot=(-1,0,0;3.14159rad)
  ResizeMode = 1
  Support = -> [Pad]
FEATURE [PartDesign::Line] HoleAxis_15
  AttacherType = Attacher::AttachEngineLine
  Length = 5.63627
  MapMode = 19
  Placement = pos=(4.81,-44.89,3.2) rot=(-1,0,0;3.14159rad)
  ResizeMode = 1
  Support = -> [Pad]
FEATURE [PartDesign::Line] HoleAxis_16
  AttacherType = Attacher::AttachEngineLine
  Length = 5.63627
  MapMode = 19
  Placement = pos=(4.81,-56.56,3.2) rot=(-1,0,0;3.14159rad)
  ResizeMode = 1
  Support = -> [Pad]
FEATURE [PartDesign::Line] HoleAxis_17
  AttacherType = Attacher::AttachEngineLine
  Length = 5.91808
  MapMode = 19
  Placement = pos=(5,-68,3.2) rot=(0,0,1;0rad)
  ResizeMode = 1
  Support = -> [Pad]
FEATURE [PartDesign::Line] HoleAxis_18
  AttacherType = Attacher::AttachEngineLine
  Length = 5.91808
  MapMode = 19
  Placement = pos=(5,-76,3.2) rot=(0,0,1;0rad)
  ResizeMode = 1
  Support = -> [Pad]
FEATURE [Sketcher::SketchObject] Sketch002
  FullyConstrained = true
  MapMode = 5
  Placement = pos=(0,0,3.2) rot=(0,0,1;0rad)
  Support = -> [Pad]
FEATURE [PartDesign::Hole] Hole
  BaseFeature = -> Pad001
  Depth = 25
  DepthType = 0
  Diameter = 3.4
  DrillForDepth = true
  DrillPoint = 1
  DrillPointAngle = 118
  HoleCutCountersinkAngle = 90
  HoleCutCustomValues = false
  HoleCutDepth = 2
  HoleCutDiameter = 8
  HoleCutType = 1
  ModelActualThread = false
  Profile = -> Pad001 [Edge30,Edge27,Edge21,Edge24]
  Tapered = false
  TaperedAngle = 90
  ThreadAngle = 0
  ThreadClass = 0
  ThreadCutOffInner = 0
  ThreadCutOffOuter = 0
  ThreadDirection = 0
  ThreadFit = 0
  ThreadPitch = 0
  ThreadSize = 9
  ThreadType = 1
  Threaded = false
FEATURE [PartDesign::Hole] Hole001
  BaseFeature = -> Hole
  Depth = 3
  DepthType = 0
  Diameter = 4.2
  DrillForDepth = false
  DrillPoint = 1
  DrillPointAngle = 118
  HoleCutCountersinkAngle = 90
  HoleCutCustomValues = false
  HoleCutDepth = 5.4
  HoleCutDiameter = 6.72
  HoleCutType = 0
  ModelActualThread = false
  Profile = -> Hole [Edge20,Edge19]
  Tapered = false
  TaperedAngle = 90
  ThreadAngle = 60
  ThreadClass = 0
  ThreadCutOffInner = 0.0866025
  ThreadCutOffOuter = 0.173205
  ThreadDirection = 0
  ThreadFit = 0
  ThreadPitch = 0.8
  ThreadSize = 13
  ThreadType = 1
  Threaded = true
FEATURE [PartDesign::Body] Body001  label="bar2_body"
  Group = -> [Sketch001,Pad001,LCS_2,HoleAxis_1,HoleAxis_2,HoleAxis_3,HoleAxis_4,HoleAxis_5,HoleAxis_6,Hole,Hole001]
  Origin = -> Origin001
  Tip = -> Hole001
FEATURE [TechDraw::DrawProjGroupItem] ProjItem003  label="Front001"
  CoarseView = false
  Direction = (0,0,1)
  Focus = 100
  HardHidden = false
  IsoCount = 0
  IsoHidden = false
  IsoVisible = false
  LockPosition = true
  Perspective = false
  Rotation = 0
  RotationVector = (1,0,0)
  ScaleType = 2
  SeamHidden = false
  SeamVisible = true
  SmoothHidden = false
  SmoothVisible = true
  Source = -> [Body001]
  Type = 0
  X = 0
  XDirection = (1,0,0)
  Y = 0
FEATURE [TechDraw::DrawProjGroupItem] ProjItem004  label="Bottom001"
  CoarseView = false
  Direction = (0,-1,0)
  Focus = 100
  HardHidden = false
  IsoCount = 0
  IsoHidden = false
  IsoVisible = false
  LockPosition = false
  Perspective = false
  Rotation = 0
  RotationVector = (1,0,0)
  ScaleType = 2
  SeamHidden = false
  SeamVisible = true
  SmoothHidden = false
  SmoothVisible = true
  Source = -> [Body001]
  Type = 5
  X = 0
  XDirection = (1,0,0)
  Y = 50.35
FEATURE [TechDraw::DrawProjGroupItem] ProjItem005  label="Right001"
  CoarseView = false
  Direction = (1,0,1e-16)
  Focus = 100
  HardHidden = false
  IsoCount = 0
  IsoHidden = false
  IsoVisible = false
  LockPosition = false
  Perspective = false
  Rotation = 0
  RotationVector = (1,0,0)
  ScaleType = 2
  SeamHidden = false
  SeamVisible = true
  SmoothHidden = false
  SmoothVisible = true
  Source = -> [Body001]
  Type = 2
  X = -21.6
  XDirection = (1e-16,0,-1)
  Y = 0
FEATURE [TechDraw::DrawProjGroup] ProjGroup001  label="bar2_ProjGroup"
  Anchor = -> ProjItem003
  AutoDistribute = true
  LockPosition = false
  ProjectionType = 0
  Rotation = 0
  ScaleType = 0
  Source = -> [Body001]
  Views = -> [ProjItem003,ProjItem004,ProjItem005]
  X = 229.028
  Y = 134.779
  spacingX = 15
  spacingY = 15
FEATURE [App::DocumentObjectGroup] Group005  label="bar2_group"
  Group = -> [union005,Shape2DView001,Body001,ProjGroup001]
FEATURE [TechDraw::DrawViewDimension] Dimension024
  Arbitrary = false
  ArbitraryTolerances = false
  EqualTolerance = true
  FormatSpec = %.2f
  FormatSpecOverTolerance = %+.2f
  FormatSpecUnderTolerance = %+.2f
  Inverted = false
  LockPosition = false
  MeasureType = 1
  OverTolerance = 0
  References2D = -> [ProjItem003]
  Rotation = 0
  ScaleType = 0
  TheoreticalExact = false
  Type = 2
  UnderTolerance = 0
  X = 13.4217
  Y = 0.123273
FEATURE [TechDraw::DrawViewDimension] Dimension025
  Arbitrary = false
  ArbitraryTolerances = false
  EqualTolerance = true
  FormatSpec = %.2f
  FormatSpecOverTolerance = %+.2f
  FormatSpecUnderTolerance = %+.2f
  Inverted = false
  LockPosition = false
  MeasureType = 1
  OverTolerance = 0
  References2D = -> [ProjItem003]
  Rotation = 0
  ScaleType = 0
  TheoreticalExact = false
  Type = 2
  UnderTolerance = 0
  X = 13.3126
  Y = 13.6689
FEATURE [TechDraw::DrawViewDimension] Dimension026
  Arbitrary = false
  ArbitraryTolerances = false
  EqualTolerance = true
  FormatSpec = %.2f
  FormatSpecOverTolerance = %+.2f
  FormatSpecUnderTolerance = %+.2f
  Inverted = false
  LockPosition = false
  MeasureType = 1
  OverTolerance = 0
  References2D = -> [ProjItem003]
  Rotation = 0
  ScaleType = 0
  TheoreticalExact = false
  Type = 2
  UnderTolerance = 0
  X = 13.3126
  Y = 26.2324
FEATURE [TechDraw::DrawViewDimension] Dimension027
  Arbitrary = false
  ArbitraryTolerances = false
  EqualTolerance = true
  FormatSpec = %.2f
  FormatSpecOverTolerance = %+.2f
  FormatSpecUnderTolerance = %+.2f
  Inverted = false
  LockPosition = false
  MeasureType = 1
  OverTolerance = 0
  References2D = -> [ProjItem003]
  Rotation = 0
  ScaleType = 0
  TheoreticalExact = false
  Type = 2
  UnderTolerance = 0
  X = 13.4217
  Y = -13.6517
FEATURE [TechDraw::DrawViewDimension] Dimension028
  Arbitrary = false
  ArbitraryTolerances = false
  EqualTolerance = true
  FormatSpec = %.2f
  FormatSpecOverTolerance = %+.2f
  FormatSpecUnderTolerance = %+.2f
  Inverted = false
  LockPosition = false
  MeasureType = 1
  OverTolerance = 0
  References2D = -> [ProjItem003]
  Rotation = 0
  ScaleType = 0
  TheoreticalExact = false
  Type = 2
  UnderTolerance = 0
  X = 29.0448
  Y = -15.0874
FEATURE [TechDraw::DrawViewDimension] Dimension029
  Arbitrary = false
  ArbitraryTolerances = false
  EqualTolerance = true
  FormatSpec = %.2f
  FormatSpecOverTolerance = %+.2f
  FormatSpecUnderTolerance = %+.2f
  Inverted = false
  LockPosition = false
  MeasureType = 1
  OverTolerance = 0
  References2D = -> [ProjItem003]
  Rotation = 0
  ScaleType = 0
  TheoreticalExact = false
  Type = 2
  UnderTolerance = 0
  X = 28.9947
  Y = 42.3775
FEATURE [TechDraw::DrawViewDimension] Dimension030
  Arbitrary = false
  ArbitraryTolerances = false
  EqualTolerance = true
  FormatSpec = %.2f
  FormatSpecOverTolerance = %+.2f
  FormatSpecUnderTolerance = %+.2f
  Inverted = false
  LockPosition = false
  MeasureType = 1
  OverTolerance = 0
  References2D = -> [ProjItem003]
  Rotation = 0
  ScaleType = 0
  TheoreticalExact = false
  Type = 2
  UnderTolerance = 0
  X = 20.9139
  Y = -38.0316
FEATURE [TechDraw::DrawViewDimension] Dimension031
  Arbitrary = false
  ArbitraryTolerances = false
  EqualTolerance = true
  FormatSpec = %.2f
  FormatSpecOverTolerance = %+.2f
  FormatSpecUnderTolerance = %+.2f
  Inverted = false
  LockPosition = false
  MeasureType = 1
  OverTolerance = 0
  References2D = -> [ProjItem003]
  Rotation = 0
  ScaleType = 0
  TheoreticalExact = false
  Type = 1
  UnderTolerance = 0
  X = -18.1472
  Y = -12.4166
FEATURE [TechDraw::DrawViewDimension] Dimension032
  Arbitrary = false
  ArbitraryTolerances = false
  EqualTolerance = true
  FormatSpec = ⌀%.2f
  FormatSpecOverTolerance = %+.2f
  FormatSpecUnderTolerance = %+.2f
  Inverted = false
  LockPosition = false
  MeasureType = 1
  OverTolerance = 0
  References2D = -> [ProjItem003]
  Rotation = 0
  ScaleType = 0
  TheoreticalExact = false
  Type = 5
  UnderTolerance = 0
  X = -19.2094
  Y = 8.43112
FEATURE [TechDraw::DrawViewDimension] Dimension033
  Arbitrary = true
  ArbitraryTolerances = false
  EqualTolerance = true
  FormatSpec = ⌀M5 c/ rosca
  FormatSpecOverTolerance = %+.2f
  FormatSpecUnderTolerance = %+.2f
  Inverted = false
  LockPosition = false
  MeasureType = 1
  OverTolerance = 0
  References2D = -> [ProjItem003]
  Rotation = 0
  ScaleType = 0
  TheoreticalExact = false
  Type = 5
  UnderTolerance = 0
  X = -22.7419
  Y = -33.2918
FEATURE [TechDraw::DrawViewDimension] Dimension035
  Arbitrary = true
  ArbitraryTolerances = false
  EqualTolerance = true
  FormatSpec = ⌀M5 c/ rosca
  FormatSpecOverTolerance = %+.2f
  FormatSpecUnderTolerance = %+.2f
  Inverted = false
  LockPosition = false
  MeasureType = 1
  OverTolerance = 0
  References2D = -> [ProjItem003]
  Rotation = 0
  ScaleType = 0
  TheoreticalExact = false
  Type = 5
  UnderTolerance = 0
  X = -23.8113
  Y = -25.5326
FEATURE [TechDraw::DrawViewDimension] Dimension043
  Arbitrary = false
  ArbitraryTolerances = false
  EqualTolerance = true
  FormatSpec = %.2f
  FormatSpecOverTolerance = %+.2f
  FormatSpecUnderTolerance = %+.2f
  Inverted = false
  LockPosition = false
  MeasureType = 1
  OverTolerance = 0
  References2D = -> [ProjItem005]
  Rotation = 0
  ScaleType = 0
  TheoreticalExact = false
  Type = 2
  UnderTolerance = 0
  X = -14.6369
  Y = 1.23933
FEATURE [TechDraw::DrawViewDimension] Dimension044
  Arbitrary = false
  ArbitraryTolerances = false
  EqualTolerance = true
  FormatSpec = %.2f
  FormatSpecOverTolerance = %+.2f
  FormatSpecUnderTolerance = %+.2f
  Inverted = false
  LockPosition = false
  MeasureType = 1
  OverTolerance = 0
  References2D = -> [ProjItem005]
  Rotation = 0
  ScaleType = 0
  TheoreticalExact = false
  Type = 1
  UnderTolerance = 0
  X = -0.495734
  Y = 44.6668
FEATURE [TechDraw::DrawViewDimension] Dimension045
  Arbitrary = false
  ArbitraryTolerances = false
  EqualTolerance = true
  FormatSpec = %.2f
  FormatSpecOverTolerance = %+.2f
  FormatSpecUnderTolerance = %+.2f
  Inverted = false
  LockPosition = false
  MeasureType = 1
  OverTolerance = 0
  References2D = -> [ProjItem004]
  Rotation = 0
  ScaleType = 0
  TheoreticalExact = false
  Type = 1
  UnderTolerance = 0
  X = 0
  Y = 13.6455
FEATURE [TechDraw::DrawViewPart] View001
  CoarseView = false
  Direction = (0.577,-0.577,0.577)
  Focus = 100
  HardHidden = false
  IsoCount = 0
  IsoHidden = false
  IsoVisible = false
  LockPosition = false
  Perspective = false
  Rotation = 0
  ScaleType = 0
  SeamHidden = false
  SeamVisible = true
  SmoothHidden = false
  SmoothVisible = true
  Source = -> [Body001]
  X = 212.253
  XDirection = (0.707,0.707,0)
  Y = 231.311
FEATURE [PartDesign::Hole] Hole002
  BaseFeature = -> Pad
  Depth = 25
  DepthType = 0
  Diameter = 4.2
  DrillForDepth = false
  DrillPoint = 1
  DrillPointAngle = 118
  HoleCutCountersinkAngle = 90
  HoleCutCustomValues = false
  HoleCutDepth = 0
  HoleCutDiameter = 6.1
  HoleCutType = 0
  ModelActualThread = false
  Profile = -> Pad [Edge15,Edge18]
  Tapered = false
  TaperedAngle = 90
  ThreadAngle = 60
  ThreadClass = 0
  ThreadCutOffInner = 0.0866025
  ThreadCutOffOuter = 0.173205
  ThreadDirection = 0
  ThreadFit = 0
  ThreadPitch = 0.8
  ThreadSize = 13
  ThreadType = 1
  Threaded = true
FEATURE [PartDesign::Body] Body  label="bar1_Body"
  Group = -> [Sketch,Pad,LCS_1,HoleAxis_7,HoleAxis_8,HoleAxis_9,HoleAxis_10,HoleAxis_11,HoleAxis_12,HoleAxis_13,HoleAxis_14,HoleAxis_15,HoleAxis_16,HoleAxis_17,HoleAxis_18,Hole002]
  Origin = -> Origin
  Tip = -> Hole002
FEATURE [TechDraw::DrawProjGroupItem] ProjItem  label="Front"
  CoarseView = false
  Direction = (0,0,1)
  Focus = 100
  HardHidden = false
  IsoCount = 0
  IsoHidden = false
  IsoVisible = false
  LockPosition = true
  Perspective = false
  Rotation = 0
  RotationVector = (1,0,0)
  ScaleType = 2
  SeamHidden = false
  SeamVisible = true
  SmoothHidden = false
  SmoothVisible = true
  Source = -> [Body]
  Type = 0
  X = 0
  XDirection = (1,0,0)
  Y = 0
FEATURE [TechDraw::DrawProjGroupItem] ProjItem001  label="Right"
  CoarseView = false
  Direction = (1,0,1e-16)
  Focus = 100
  HardHidden = false
  IsoCount = 0
  IsoHidden = false
  IsoVisible = false
  LockPosition = false
  Perspective = false
  Rotation = 0
  RotationVector = (1,0,0)
  ScaleType = 2
  SeamHidden = false
  SeamVisible = true
  SmoothHidden = false
  SmoothVisible = true
  Source = -> [Body]
  Type = 2
  X = -21.6
  XDirection = (1e-16,0,-1)
  Y = 0
FEATURE [TechDraw::DrawProjGroupItem] ProjItem002  label="Bottom"
  CoarseView = false
  Direction = (0,-1,0)
  Focus = 100
  HardHidden = false
  IsoCount = 0
  IsoHidden = false
  IsoVisible = false
  LockPosition = false
  Perspective = false
  Rotation = 0
  RotationVector = (1,0,0)
  ScaleType = 2
  SeamHidden = false
  SeamVisible = true
  SmoothHidden = false
  SmoothVisible = true
  Source = -> [Body]
  Type = 5
  X = 0
  XDirection = (1,0,0)
  Y = 86.6
FEATURE [TechDraw::DrawProjGroup] ProjGroup  label="bar1_ProjGroup"
  Anchor = -> ProjItem
  AutoDistribute = true
  LockPosition = false
  ProjectionType = 0
  Rotation = 0
  ScaleType = 0
  Source = -> [Body]
  Views = -> [ProjItem,ProjItem001,ProjItem002]
  X = 113.787
  Y = 98.3052
  spacingX = 15
  spacingY = 15
FEATURE [App::DocumentObjectGroup] Group004  label="bar1_group"
  Group = -> [union003,Shape2DView,Body,ProjGroup]
FEATURE [TechDraw::DrawViewDimension] Dimension001
  Arbitrary = false
  ArbitraryTolerances = false
  EqualTolerance = true
  FormatSpec = %.2f
  FormatSpecOverTolerance = %+.2f
  FormatSpecUnderTolerance = %+.2f
  Inverted = false
  LockPosition = false
  MeasureType = 1
  OverTolerance = 0
  References2D = -> [ProjItem]
  Rotation = 0
  ScaleType = 0
  TheoreticalExact = false
  Type = 1
  UnderTolerance = 0
  X = -17.6797
  Y = -35.607
FEATURE [TechDraw::DrawViewDimension] Dimension
  Arbitrary = false
  ArbitraryTolerances = false
  EqualTolerance = true
  FormatSpec = %.2f
  FormatSpecOverTolerance = %+.2f
  FormatSpecUnderTolerance = %+.2f
  Inverted = false
  LockPosition = false
  MeasureType = 1
  OverTolerance = 0
  References2D = -> [ProjItem]
  Rotation = 0
  ScaleType = 0
  TheoreticalExact = false
  Type = 1
  UnderTolerance = 0
  X = -17.4484
  Y = -47.7836
FEATURE [TechDraw::DrawViewDimension] Dimension003
  Arbitrary = false
  ArbitraryTolerances = false
  EqualTolerance = true
  FormatSpec = %.2f
  FormatSpecOverTolerance = %+.2f
  FormatSpecUnderTolerance = %+.2f
  Inverted = false
  LockPosition = false
  MeasureType = 1
  OverTolerance = 0
  References2D = -> [ProjItem]
  Rotation = 0
  ScaleType = 0
  TheoreticalExact = false
  Type = 2
  UnderTolerance = 0
  X = 13.8288
  Y = -38.2243
FEATURE [TechDraw::DrawViewDimension] Dimension004
  Arbitrary = false
  ArbitraryTolerances = false
  EqualTolerance = true
  FormatSpec = %.2f
  FormatSpecOverTolerance = %+.2f
  FormatSpecUnderTolerance = %+.2f
  Inverted = false
  LockPosition = false
  MeasureType = 1
  OverTolerance = 0
  References2D = -> [ProjItem]
  Rotation = 0
  ScaleType = 0
  TheoreticalExact = false
  Type = 2
  UnderTolerance = 0
  X = 13.8387
  Y = -26.3987
FEATURE [TechDraw::DrawViewDimension] Dimension005
  Arbitrary = false
  ArbitraryTolerances = false
  EqualTolerance = true
  FormatSpec = %.2f
  FormatSpecOverTolerance = %+.2f
  FormatSpecUnderTolerance = %+.2f
  Inverted = false
  LockPosition = false
  MeasureType = 1
  OverTolerance = 0
  References2D = -> [ProjItem]
  Rotation = 0
  ScaleType = 0
  TheoreticalExact = false
  Type = 2
  UnderTolerance = 0
  X = 13.8387
  Y = -15.1437
FEATURE [TechDraw::DrawViewDimension] Dimension006
  Arbitrary = false
  ArbitraryTolerances = false
  EqualTolerance = true
  FormatSpec = %.2f
  FormatSpecOverTolerance = %+.2f
  FormatSpecUnderTolerance = %+.2f
  Inverted = false
  LockPosition = false
  MeasureType = 1
  OverTolerance = 0
  References2D = -> [ProjItem]
  Rotation = 0
  ScaleType = 0
  TheoreticalExact = false
  Type = 2
  UnderTolerance = 0
  X = 20.2765
  Y = 1.03219
FEATURE [TechDraw::DrawViewDimension] Dimension007
  Arbitrary = false
  ArbitraryTolerances = false
  EqualTolerance = true
  FormatSpec = %.2f
  FormatSpecOverTolerance = %+.2f
  FormatSpecUnderTolerance = %+.2f
  Inverted = false
  LockPosition = false
  MeasureType = 1
  OverTolerance = 0
  References2D = -> [ProjItem]
  Rotation = 0
  ScaleType = 0
  TheoreticalExact = false
  Type = 2
  UnderTolerance = 0
  X = 28.4399
  Y = -50.4693
FEATURE [TechDraw::DrawViewDimension] Dimension008
  Arbitrary = false
  ArbitraryTolerances = false
  EqualTolerance = true
  FormatSpec = %.2f
  FormatSpecOverTolerance = %+.2f
  FormatSpecUnderTolerance = %+.2f
  Inverted = false
  LockPosition = false
  MeasureType = 1
  OverTolerance = 0
  References2D = -> [ProjItem]
  Rotation = 0
  ScaleType = 0
  TheoreticalExact = false
  Type = 2
  UnderTolerance = 0
  X = 19.8657
  Y = -73.109
FEATURE [TechDraw::DrawViewDimension] Dimension009
  Arbitrary = true
  ArbitraryTolerances = false
  EqualTolerance = true
  FormatSpec = ⌀M5 c/ rosca
  FormatSpecOverTolerance = %+.2f
  FormatSpecUnderTolerance = %+.2f
  Inverted = false
  LockPosition = false
  MeasureType = 1
  OverTolerance = 0
  References2D = -> [ProjItem]
  Rotation = 0
  ScaleType = 0
  TheoreticalExact = false
  Type = 5
  UnderTolerance = 0
  X = -21.8084
  Y = -66.722
FEATURE [TechDraw::DrawViewDimension] Dimension010
  Arbitrary = false
  ArbitraryTolerances = false
  EqualTolerance = true
  FormatSpec = %.2f
  FormatSpecOverTolerance = %+.2f
  FormatSpecUnderTolerance = %+.2f
  Inverted = false
  LockPosition = false
  MeasureType = 1
  OverTolerance = 0
  References2D = -> [ProjItem]
  Rotation = 0
  ScaleType = 0
  TheoreticalExact = false
  Type = 2
  UnderTolerance = 0
  X = 9.28199
  Y = 11.788
FEATURE [TechDraw::DrawViewDimension] Dimension011
  Arbitrary = false
  ArbitraryTolerances = false
  EqualTolerance = true
  FormatSpec = %.2f
  FormatSpecOverTolerance = %+.2f
  FormatSpecUnderTolerance = %+.2f
  Inverted = false
  LockPosition = false
  MeasureType = 1
  OverTolerance = 0
  References2D = -> [ProjItem]
  Rotation = 0
  ScaleType = 0
  TheoreticalExact = false
  Type = 2
  UnderTolerance = 0
  X = 20.2847
  Y = 22.1544
FEATURE [TechDraw::DrawViewDimension] Dimension012
  Arbitrary = false
  ArbitraryTolerances = false
  EqualTolerance = true
  FormatSpec = %.2f
  FormatSpecOverTolerance = %+.2f
  FormatSpecUnderTolerance = %+.2f
  Inverted = false
  LockPosition = false
  MeasureType = 1
  OverTolerance = 0
  References2D = -> [ProjItem]
  Rotation = 0
  ScaleType = 0
  TheoreticalExact = false
  Type = 2
  UnderTolerance = 0
  X = 13.5804
  Y = 51.1966
FEATURE [TechDraw::DrawViewDimension] Dimension013
  Arbitrary = false
  ArbitraryTolerances = false
  EqualTolerance = true
  FormatSpec = %.2f
  FormatSpecOverTolerance = %+.2f
  FormatSpecUnderTolerance = %+.2f
  Inverted = false
  LockPosition = false
  MeasureType = 1
  OverTolerance = 0
  References2D = -> [ProjItem]
  Rotation = 0
  ScaleType = 0
  TheoreticalExact = false
  Type = 2
  UnderTolerance = 0
  X = 13.5804
  Y = 63.2969
FEATURE [TechDraw::DrawViewDimension] Dimension014
  Arbitrary = false
  ArbitraryTolerances = false
  EqualTolerance = true
  FormatSpec = %.2f
  FormatSpecOverTolerance = %+.2f
  FormatSpecUnderTolerance = %+.2f
  Inverted = false
  LockPosition = false
  MeasureType = 1
  OverTolerance = 0
  References2D = -> [ProjItem]
  Rotation = 0
  ScaleType = 0
  TheoreticalExact = false
  Type = 2
  UnderTolerance = 0
  X = 13.5804
  Y = 39.5266
FEATURE [TechDraw::DrawViewDimension] Dimension015
  Arbitrary = false
  ArbitraryTolerances = false
  EqualTolerance = true
  FormatSpec = %.2f
  FormatSpecOverTolerance = %+.2f
  FormatSpecUnderTolerance = %+.2f
  Inverted = false
  LockPosition = false
  MeasureType = 1
  OverTolerance = 0
  References2D = -> [ProjItem]
  Rotation = 0
  ScaleType = 0
  TheoreticalExact = false
  Type = 1
  UnderTolerance = 0
  X = -17.2861
  Y = 66.9147
FEATURE [TechDraw::DrawViewDimension] Dimension016
  Arbitrary = false
  ArbitraryTolerances = false
  EqualTolerance = true
  FormatSpec = %.2f
  FormatSpecOverTolerance = %+.2f
  FormatSpecUnderTolerance = %+.2f
  Inverted = false
  LockPosition = false
  MeasureType = 1
  OverTolerance = 0
  References2D = -> [ProjItem]
  Rotation = 0
  ScaleType = 0
  TheoreticalExact = false
  Type = 2
  UnderTolerance = 0
  X = 20.7713
  Y = 79.0366
FEATURE [TechDraw::DrawViewDimension] Dimension017
  Arbitrary = false
  ArbitraryTolerances = false
  EqualTolerance = true
  FormatSpec = %.2f
  FormatSpecOverTolerance = %+.2f
  FormatSpecUnderTolerance = %+.2f
  Inverted = false
  LockPosition = false
  MeasureType = 1
  OverTolerance = 0
  References2D = -> [ProjItem001]
  Rotation = 0
  ScaleType = 0
  TheoreticalExact = false
  Type = 2
  UnderTolerance = 0
  X = -13.5557
  Y = -1.1404
FEATURE [TechDraw::DrawViewDimension] Dimension018
  Arbitrary = false
  ArbitraryTolerances = false
  EqualTolerance = true
  FormatSpec = %.2f
  FormatSpecOverTolerance = %+.2f
  FormatSpecUnderTolerance = %+.2f
  Inverted = false
  LockPosition = false
  MeasureType = 1
  OverTolerance = 0
  References2D = -> [ProjItem001]
  Rotation = 0
  ScaleType = 0
  TheoreticalExact = false
  Type = 1
  UnderTolerance = 0
  X = -1.0861
  Y = 80.5895
FEATURE [TechDraw::DrawViewDimension] Dimension019
  Arbitrary = false
  ArbitraryTolerances = false
  EqualTolerance = true
  FormatSpec = %.2f
  FormatSpecOverTolerance = %+.2f
  FormatSpecUnderTolerance = %+.2f
  Inverted = false
  LockPosition = false
  MeasureType = 1
  OverTolerance = 0
  References2D = -> [ProjItem002]
  Rotation = 0
  ScaleType = 0
  TheoreticalExact = false
  Type = 1
  UnderTolerance = 0
  X = -0.543049
  Y = 11.8047
FEATURE [TechDraw::DrawViewDimension] Dimension020
  Arbitrary = false
  ArbitraryTolerances = false
  EqualTolerance = true
  FormatSpec = ⌀%.2f
  FormatSpecOverTolerance = %+.2f
  FormatSpecUnderTolerance = %+.2f
  Inverted = false
  LockPosition = false
  MeasureType = 1
  OverTolerance = 0
  References2D = -> [ProjItem]
  Rotation = 0
  ScaleType = 0
  TheoreticalExact = false
  Type = 5
  UnderTolerance = 0
  X = -28.5336
  Y = 41.9241
FEATURE [TechDraw::DrawViewDimension] Dimension021
  Arbitrary = false
  ArbitraryTolerances = false
  EqualTolerance = true
  FormatSpec = ⌀%.2f
  FormatSpecOverTolerance = %+.2f
  FormatSpecUnderTolerance = %+.2f
  Inverted = false
  LockPosition = false
  MeasureType = 1
  OverTolerance = 0
  References2D = -> [ProjItem]
  Rotation = 0
  ScaleType = 0
  TheoreticalExact = false
  Type = 5
  UnderTolerance = 0
  X = -26.8721
  Y = 61.6716
FEATURE [TechDraw::DrawViewDimension] Dimension022
  Arbitrary = false
  ArbitraryTolerances = false
  EqualTolerance = true
  FormatSpec = ⌀%.2f
  FormatSpecOverTolerance = %+.2f
  FormatSpecUnderTolerance = %+.2f
  Inverted = false
  LockPosition = false
  MeasureType = 1
  OverTolerance = 0
  References2D = -> [ProjItem]
  Rotation = 0
  ScaleType = 0
  TheoreticalExact = false
  Type = 5
  UnderTolerance = 0
  X = -33.8173
  Y = -24.6167
FEATURE [TechDraw::DrawViewDimension] Dimension023
  Arbitrary = false
  ArbitraryTolerances = false
  EqualTolerance = true
  FormatSpec = %.2f
  FormatSpecOverTolerance = %+.2f
  FormatSpecUnderTolerance = %+.2f
  Inverted = false
  LockPosition = false
  MeasureType = 1
  OverTolerance = 0
  References2D = -> [ProjItem]
  Rotation = 0
  ScaleType = 0
  TheoreticalExact = false
  Type = 2
  UnderTolerance = 0
  X = 13.8374
  Y = -49.9492
FEATURE [TechDraw::DrawViewDimension] Dimension034
  Arbitrary = true
  ArbitraryTolerances = false
  EqualTolerance = true
  FormatSpec = ⌀M5 c/ rosca
  FormatSpecOverTolerance = %+.2f
  FormatSpecUnderTolerance = %+.2f
  Inverted = false
  LockPosition = false
  MeasureType = 1
  OverTolerance = 0
  References2D = -> [ProjItem]
  Rotation = 0
  ScaleType = 0
  TheoreticalExact = false
  Type = 5
  UnderTolerance = 0
  X = -23.9847
  Y = -59.5306
FEATURE [TechDraw::DrawViewDimension] Dimension036
  Arbitrary = false
  ArbitraryTolerances = false
  EqualTolerance = true
  FormatSpec = ⌀%.2f
  FormatSpecOverTolerance = %+.2f
  FormatSpecUnderTolerance = %+.2f
  Inverted = false
  LockPosition = false
  MeasureType = 1
  OverTolerance = 0
  References2D = -> [ProjItem]
  Rotation = 0
  ScaleType = 0
  TheoreticalExact = false
  Type = 5
  UnderTolerance = 0
  X = -29.5552
  Y = 34.0748
FEATURE [TechDraw::DrawViewDimension] Dimension037
  Arbitrary = false
  ArbitraryTolerances = false
  EqualTolerance = true
  FormatSpec = ⌀%.2f
  FormatSpecOverTolerance = %+.2f
  FormatSpecUnderTolerance = %+.2f
  Inverted = false
  LockPosition = false
  MeasureType = 1
  OverTolerance = 0
  References2D = -> [ProjItem]
  Rotation = 0
  ScaleType = 0
  TheoreticalExact = false
  Type = 5
  UnderTolerance = 0
  X = -24.9027
  Y = -16.2327
FEATURE [TechDraw::DrawViewDimension] Dimension038
  Arbitrary = false
  ArbitraryTolerances = false
  EqualTolerance = true
  FormatSpec = ⌀%.2f
  FormatSpecOverTolerance = %+.2f
  FormatSpecUnderTolerance = %+.2f
  Inverted = false
  LockPosition = false
  MeasureType = 1
  OverTolerance = 0
  References2D = -> [ProjItem]
  Rotation = 0
  ScaleType = 0
  TheoreticalExact = false
  Type = 5
  UnderTolerance = 0
  X = -34.52
  Y = -37.7093
FEATURE [TechDraw::DrawViewDimension] Dimension039
  Arbitrary = false
  ArbitraryTolerances = false
  EqualTolerance = true
  FormatSpec = ⌀%.2f
  FormatSpecOverTolerance = %+.2f
  FormatSpecUnderTolerance = %+.2f
  Inverted = false
  LockPosition = false
  MeasureType = 1
  OverTolerance = 0
  References2D = -> [ProjItem]
  Rotation = 0
  ScaleType = 0
  TheoreticalExact = false
  Type = 5
  UnderTolerance = 0
  X = -27.8953
  Y = 52.4132
FEATURE [TechDraw::DrawViewPart] View
  CoarseView = false
  Direction = (0.577,-0.577,0.577)
  Focus = 100
  HardHidden = false
  IsoCount = 0
  IsoHidden = false
  IsoVisible = false
  LockPosition = false
  Perspective = false
  Rotation = 0
  ScaleType = 0
  SeamHidden = false
  SeamVisible = true
  SmoothHidden = false
  SmoothVisible = true
  Source = -> [Body]
  X = 100.708
  XDirection = (0.707,0.707,0)
  Y = 245.598
FEATURE [PartDesign::CoordinateSystem] LCS_0
  AttacherType = Attacher::AttachEngine3D
  MapMode = 2
  Support = -> [X_Axis002]
FEATURE [Part::FeaturePython] Tube  # WARN: FeaturePython — macro-defined, semantics opaque (R4)
  AttacherType = Attacher::AttachEngine3D
  Height = 2
  InnerRadius = 3
  OuterRadius = 4
FEATURE [Part::FeaturePython] Tube001  # WARN: FeaturePython — macro-defined, semantics opaque (R4)
  AttacherType = Attacher::AttachEngine3D
  Height = 1
  InnerRadius = 1.5
  OuterRadius = 3
FEATURE [Part::MultiFuse] Fusion
  Shapes = -> [Tube,Tube001]
FEATURE [PartDesign::FeatureBase] BaseFeature
  BaseFeature = -> Fusion
FEATURE [PartDesign::Body] insulator
  BaseFeature = -> Fusion
  Group = -> [BaseFeature,LCS_0]
  Origin = -> Origin002
  Placement = pos=(50,0,0) rot=(0,0,1;0rad)
  Tip = -> BaseFeature
FEATURE [TechDraw::DrawViewDimension] Dimension046
  Arbitrary = false
  ArbitraryTolerances = false
  EqualTolerance = true
  FormatSpec = ⌀%.4f
  FormatSpecOverTolerance = %+.4f
  FormatSpecUnderTolerance = %+.4f
  Inverted = false
  LockPosition = false
  MeasureType = 1
  OverTolerance = 0
  References2D = -> [ProjItem003]
  Rotation = 0
  ScaleType = 0
  TheoreticalExact = false
  Type = 5
  UnderTolerance = 0
  X = -25.2801
  Y = -3.641
FEATURE [TechDraw::DrawViewDimension] Dimension047
  Arbitrary = false
  ArbitraryTolerances = false
  EqualTolerance = true
  FormatSpec = %.4f
  FormatSpecOverTolerance = %+.4f
  FormatSpecUnderTolerance = %+.4f
  Inverted = false
  LockPosition = false
  MeasureType = 1
  OverTolerance = 0
  References2D = -> [ProjItem]
  Rotation = 0
  ScaleType = 0
  TheoreticalExact = false
  Type = 0
  UnderTolerance = 0
  X = -16.9882
  Y = 6.72652
FEATURE [TechDraw::DrawPage] Page
  KeepUpdated = true
  NextBalloonIndex = 1
  ProjectionType = 0
  Template = -> Template
  Views = -> [Sheet,ProjGroup,ProjGroup001,Dimension001,Dimension,Dimension003,Dimension004,Dimension005,Dimension006,Dimension007,Dimension008,Dimension009,Dimension010,Dimension011,Dimension012,Dimension013,Dimension014,Dimension015,Dimension016,Dimension017,Dimension018,Dimension019,Dimension020,Dimension021,Dimension022,Dimension023,Dimension024,Dimension025,Dimension026,Dimension027,Dimension028,+18 more]
---- part caps.FCStd = doc fcstd_51091139d212 ----
FCSTD DOCUMENT  (FreeCAD 0.19R24291 (Git))
Label: caps
License: Creative Commons Attribution-NonCommercial-ShareAlike
LicenseURL: http://creativecommons.org/licenses/by-nc-sa/4.0/
objects: App::Link×106, PartDesign::Line×8, App::LinkGroup×4, Part::Feature×3, PartDesign::CoordinateSystem×2, Sketcher::SketchObject×1, App::Part×1
note: 14 computed .brp shape members not serialized (recipe doc carries the construction recipe); baked Part::Feature solids carry a one-line shape summary decoded from their .brp

FEATURE [PartDesign::CoordinateSystem] Local_CS_1fb6
  AttacherType = Attacher::AttachEngine3D
FEATURE [Part::Feature] Pcb_1fb6
  Placement = pos=(-110.5,80.5,0) rot=(0,0,1;0rad)
  shape: bbox 75 x 42 x 1.6 mm, 14 faces (baked)
FEATURE [Sketcher::SketchObject] PCB_Sketch_1fb6
  FullyConstrained = false
  sketch-geometry (4):
    g0: LineSegment StartX=0 StartY=0 StartZ=0 EndX=75 EndY=0 EndZ=0
    g1: LineSegment StartX=0 StartY=-42 StartZ=0 EndX=0 EndY=0 EndZ=0
    g2: LineSegment StartX=75 StartY=-42 StartZ=0 EndX=0 EndY=-42 EndZ=0
    g3: LineSegment StartX=75 StartY=0 StartZ=0 EndX=75 EndY=-42 EndZ=0
  constraints (4):
    c: Coincident(g1,g2)
    c: Coincident(g0,g1)
    c: Coincident(g2,g3)
    c: Coincident(g0,g3)
FEATURE [App::LinkGroup] Board_Geoms_1fb6
  ElementList = -> [Pcb_1fb6,Local_CS_1fb6,PCB_Sketch_1fb6]
  LinkMode = 0
FEATURE [Part::Feature] Shape  label="C232_C_0603_1608Metric_6077F2BE"
  Placement = pos=(13.825,-10.655,0) rot=(0,0,-1;1.5708rad)
  shape: bbox 0.8 x 1.6 x 0.8 mm, 28 faces (baked)
FEATURE [App::Link] C232_C_0603_1608Metric_6077F2BE_ln_  label="C231_C_0603_1608Metric_607530A9"
  LinkPlacement = pos=(12.3,-10.65,0) rot=(0,0,-1;1.5708rad)
  LinkedObject = -> Shape
  Placement = pos=(12.3,-10.65,0) rot=(0,0,-1;1.5708rad)
FEATURE [Part::Feature] Shape001  label="C230_C_1210_3225Metric_6077E91F"
  Placement = pos=(35.875,-24.645,0) rot=(0,0,-1;1.5708rad)
  shape: bbox 2.5 x 3.2 x 2.5 mm, 28 faces (baked)
FEATURE [App::Link] C230_C_1210_3225Metric_6077E91F_ln_  label="C229_C_1210_3225Metric_6077F675"
  LinkPlacement = pos=(19.575,-10.655,0) rot=(0,0,-1;1.5708rad)
  LinkedObject = -> Shape001
  Placement = pos=(19.575,-10.655,0) rot=(0,0,-1;1.5708rad)
FEATURE [App::Link] C230_C_1210_3225Metric_6077E91F_ln_001  label="C228_C_1210_3225Metric_6077E3C7"
  LinkPlacement = pos=(32.625,-24.645,0) rot=(0,0,-1;1.5708rad)
  LinkedObject = -> Shape001
  Placement = pos=(32.625,-24.645,0) rot=(0,0,-1;1.5708rad)
FEATURE [App::Link] C230_C_1210_3225Metric_6077E91F_ln_002  label="C227_C_1210_3225Metric_6077FA4A"
  LinkPlacement = pos=(32.575,-10.655,0) rot=(0,0,-1;1.5708rad)
  LinkedObject = -> Shape001
  Placement = pos=(32.575,-10.655,0) rot=(0,0,-1;1.5708rad)
FEATURE [App::Link] C230_C_1210_3225Metric_6077E91F_ln_003  label="C225_C_1210_3225Metric_6077EF6A"
  LinkPlacement = pos=(26.075,-10.655,0) rot=(0,0,-1;1.5708rad)
  LinkedObject = -> Shape001
  Placement = pos=(26.075,-10.655,0) rot=(0,0,-1;1.5708rad)
FEATURE [App::Link] C230_C_1210_3225Metric_6077E91F_ln_004  label="C222_C_1210_3225Metric_6077F4A1"
  LinkPlacement = pos=(26.125,-24.645,0) rot=(0,0,-1;1.5708rad)
  LinkedObject = -> Shape001
  Placement = pos=(26.125,-24.645,0) rot=(0,0,-1;1.5708rad)
FEATURE [App::Link] C230_C_1210_3225Metric_6077E91F_ln_005  label="C221_C_1210_3225Metric_6077EDA8"
  LinkPlacement = pos=(42.325,-10.655,0) rot=(0,0,-1;1.5708rad)
  LinkedObject = -> Shape001
  Placement = pos=(42.325,-10.655,0) rot=(0,0,-1;1.5708rad)
FEATURE [App::Link] C230_C_1210_3225Metric_6077E91F_ln_006  label="C218_C_1210_3225Metric_6077F705"
  LinkPlacement = pos=(16.375,-24.65,0) rot=(0,0,-1;1.5708rad)
  LinkedObject = -> Shape001
  Placement = pos=(16.375,-24.65,0) rot=(0,0,-1;1.5708rad)
FEATURE [App::Link] C230_C_1210_3225Metric_6077E91F_ln_007  label="C217_C_1210_3225Metric_6077EF34"
  LinkPlacement = pos=(16.375,-10.65,0) rot=(0,0,-1;1.5708rad)
  LinkedObject = -> Shape001
  Placement = pos=(16.375,-10.65,0) rot=(0,0,-1;1.5708rad)
FEATURE [App::Link] C230_C_1210_3225Metric_6077E91F_ln_008  label="C216_C_1210_3225Metric_6077F9F0"
  LinkPlacement = pos=(35.825,-10.655,0) rot=(0,0,-1;1.5708rad)
  LinkedObject = -> Shape001
  Placement = pos=(35.825,-10.655,0) rot=(0,0,-1;1.5708rad)
FEATURE [App::Link] C230_C_1210_3225Metric_6077E91F_ln_009  label="C215_C_1210_3225Metric_6077E9EE"
  LinkPlacement = pos=(39.075,-10.655,0) rot=(0,0,-1;1.5708rad)
  LinkedObject = -> Shape001
  Placement = pos=(39.075,-10.655,0) rot=(0,0,-1;1.5708rad)
FEATURE [App::Link] C230_C_1210_3225Metric_6077E91F_ln_010  label="C214_C_1210_3225Metric_6077F0CC"
  LinkPlacement = pos=(19.625,-24.645,0) rot=(0,0,-1;1.5708rad)
  LinkedObject = -> Shape001
  Placement = pos=(19.625,-24.645,0) rot=(0,0,-1;1.5708rad)
FEATURE [App::Link] C230_C_1210_3225Metric_6077E91F_ln_011  label="C213_C_1210_3225Metric_6077EB6E"
  LinkPlacement = pos=(45.625,-24.645,0) rot=(0,0,-1;1.5708rad)
  LinkedObject = -> Shape001
  Placement = pos=(45.625,-24.645,0) rot=(0,0,-1;1.5708rad)
FEATURE [App::Link] C232_C_0603_1608Metric_6077F2BE_ln_001  label="C212_C_0603_1608Metric_6077F138"
  LinkPlacement = pos=(62.625,-24.6325,0) rot=(0,0,-1;1.5708rad)
  LinkedObject = -> Shape
  Placement = pos=(62.625,-24.6325,0) rot=(0,0,-1;1.5708rad)
FEATURE [App::Link] C232_C_0603_1608Metric_6077F2BE_ln_002  label="C211_C_0603_1608Metric_6077E469"
  LinkPlacement = pos=(61.075,-10.655,0) rot=(0,0,-1;1.5708rad)
  LinkedObject = -> Shape
  Placement = pos=(61.075,-10.655,0) rot=(0,0,-1;1.5708rad)
FEATURE [App::Link] C232_C_0603_1608Metric_6077F2BE_ln_003  label="C210_C_0603_1608Metric_6077F9C0"
  LinkPlacement = pos=(12.375,-24.645,0) rot=(0,0,-1;1.5708rad)
  LinkedObject = -> Shape
  Placement = pos=(12.375,-24.645,0) rot=(0,0,-1;1.5708rad)
FEATURE [App::Link] C232_C_0603_1608Metric_6077F2BE_ln_004  label="C209_C_0603_1608Metric_6077E2A4"
  LinkPlacement = pos=(62.575,-10.655,0) rot=(0,0,-1;1.5708rad)
  LinkedObject = -> Shape
  Placement = pos=(62.575,-10.655,0) rot=(0,0,-1;1.5708rad)
FEATURE [App::Link] C230_C_1210_3225Metric_6077E91F_ln_012  label="C208_C_1210_3225Metric_6077F1FE"
  LinkPlacement = pos=(52.075,-10.655,0) rot=(0,0,-1;1.5708rad)
  LinkedObject = -> Shape001
  Placement = pos=(52.075,-10.655,0) rot=(0,0,-1;1.5708rad)
FEATURE [App::Link] C230_C_1210_3225Metric_6077E91F_ln_013  label="C207_C_1210_3225Metric_6077EAE7"
  LinkPlacement = pos=(55.375,-24.645,0) rot=(0,0,-1;1.5708rad)
  LinkedObject = -> Shape001
  Placement = pos=(55.375,-24.645,0) rot=(0,0,-1;1.5708rad)
FEATURE [App::Link] C230_C_1210_3225Metric_6077E91F_ln_014  label="C206_C_1210_3225Metric_6077E7AE"
  LinkPlacement = pos=(48.875,-24.645,0) rot=(0,0,-1;1.5708rad)
  LinkedObject = -> Shape001
  Placement = pos=(48.875,-24.645,0) rot=(0,0,-1;1.5708rad)
FEATURE [App::Link] C230_C_1210_3225Metric_6077E91F_ln_015  label="C204_C_1210_3225Metric_6077EC8B"
  LinkPlacement = pos=(45.575,-10.655,0) rot=(0,0,-1;1.5708rad)
  LinkedObject = -> Shape001
  Placement = pos=(45.575,-10.655,0) rot=(0,0,-1;1.5708rad)
FEATURE [App::Link] C230_C_1210_3225Metric_6077E91F_ln_016  label="C203_C_1210_3225Metric_6077EC58"
  LinkPlacement = pos=(22.875,-24.645,0) rot=(0,0,-1;1.5708rad)
  LinkedObject = -> Shape001
  Placement = pos=(22.875,-24.645,0) rot=(0,0,-1;1.5708rad)
FEATURE [App::Link] C230_C_1210_3225Metric_6077E91F_ln_017  label="C201_C_1210_3225Metric_6077EA1E"
  LinkPlacement = pos=(48.825,-10.655,0) rot=(0,0,-1;1.5708rad)
  LinkedObject = -> Shape001
  Placement = pos=(48.825,-10.655,0) rot=(0,0,-1;1.5708rad)
FEATURE [App::Link] C230_C_1210_3225Metric_6077E91F_ln_018  label="C200_C_1210_3225Metric_6077FC45"
  LinkPlacement = pos=(52.125,-24.645,0) rot=(0,0,-1;1.5708rad)
  LinkedObject = -> Shape001
  Placement = pos=(52.125,-24.645,0) rot=(0,0,-1;1.5708rad)
FEATURE [App::Link] C230_C_1210_3225Metric_6077E91F_ln_019  label="C199_C_1210_3225Metric_6077EAB1"
  LinkPlacement = pos=(55.325,-10.655,0) rot=(0,0,-1;1.5708rad)
  LinkedObject = -> Shape001
  Placement = pos=(55.325,-10.655,0) rot=(0,0,-1;1.5708rad)
FEATURE [App::Link] C230_C_1210_3225Metric_6077E91F_ln_020  label="C198_C_1210_3225Metric_6077F34E"
  LinkPlacement = pos=(29.375,-24.645,0) rot=(0,0,-1;1.5708rad)
  LinkedObject = -> Shape001
  Placement = pos=(29.375,-24.645,0) rot=(0,0,-1;1.5708rad)
FEATURE [App::Link] C230_C_1210_3225Metric_6077E91F_ln_021  label="C196_C_1210_3225Metric_6077EDE1"
  LinkPlacement = pos=(58.625,-24.645,0) rot=(0,0,-1;1.5708rad)
  LinkedObject = -> Shape001
  Placement = pos=(58.625,-24.645,0) rot=(0,0,-1;1.5708rad)
FEATURE [App::Link] C230_C_1210_3225Metric_6077E91F_ln_022  label="C195_C_1210_3225Metric_6077E23E"
  LinkPlacement = pos=(58.575,-10.655,0) rot=(0,0,-1;1.5708rad)
  LinkedObject = -> Shape001
  Placement = pos=(58.575,-10.655,0) rot=(0,0,-1;1.5708rad)
FEATURE [App::Link] C230_C_1210_3225Metric_6077E91F_ln_023  label="C194_C_1210_3225Metric_6077FB79"
  LinkPlacement = pos=(22.825,-10.655,0) rot=(0,0,-1;1.5708rad)
  LinkedObject = -> Shape001
  Placement = pos=(22.825,-10.655,0) rot=(0,0,-1;1.5708rad)
FEATURE [App::Link] C230_C_1210_3225Metric_6077E91F_ln_024  label="C193_C_1210_3225Metric_6077EA7B"
  LinkPlacement = pos=(39.125,-24.645,0) rot=(0,0,-1;1.5708rad)
  LinkedObject = -> Shape001
  Placement = pos=(39.125,-24.645,0) rot=(0,0,-1;1.5708rad)
FEATURE [App::Link] C230_C_1210_3225Metric_6077E91F_ln_025  label="C192_C_1210_3225Metric_6077E5B9"
  LinkPlacement = pos=(42.375,-24.645,0) rot=(0,0,-1;1.5708rad)
  LinkedObject = -> Shape001
  Placement = pos=(42.375,-24.645,0) rot=(0,0,-1;1.5708rad)
FEATURE [App::Link] C230_C_1210_3225Metric_6077E91F_ln_026  label="C191_C_1210_3225Metric_6077E5E9"
  LinkPlacement = pos=(29.325,-10.655,0) rot=(0,0,-1;1.5708rad)
  LinkedObject = -> Shape001
  Placement = pos=(29.325,-10.655,0) rot=(0,0,-1;1.5708rad)
FEATURE [App::Link] C232_C_0603_1608Metric_6077F2BE_ln_005  label="C190_C_0603_1608Metric_6077F465"
  LinkPlacement = pos=(13.875,-24.645,0) rot=(0,0,-1;1.5708rad)
  LinkedObject = -> Shape
  Placement = pos=(13.875,-24.645,0) rot=(0,0,-1;1.5708rad)
FEATURE [App::Link] C232_C_0603_1608Metric_6077F2BE_ln_006  label="C189_C_0603_1608Metric_6077F633"
  LinkPlacement = pos=(61.125,-24.6325,0) rot=(0,0,-1;1.5708rad)
  LinkedObject = -> Shape
  Placement = pos=(61.125,-24.6325,0) rot=(0,0,-1;1.5708rad)
FEATURE [App::Link] C232_C_0603_1608Metric_6077F2BE_ln_007  label="C168_C_0603_1608Metric_6077F7CE"
  LinkPlacement = pos=(12.375,-38.2125,0) rot=(0,0,-1;1.5708rad)
  LinkedObject = -> Shape
  Placement = pos=(12.375,-38.2125,0) rot=(0,0,-1;1.5708rad)
FEATURE [App::Link] C232_C_0603_1608Metric_6077F2BE_ln_008  label="C188_C_0603_1608Metric_6077E1F6"
  LinkPlacement = pos=(62.625,-38.2125,0) rot=(0,0,-1;1.5708rad)
  LinkedObject = -> Shape
  Placement = pos=(62.625,-38.2125,0) rot=(0,0,-1;1.5708rad)
FEATURE [App::Link] C232_C_0603_1608Metric_6077F2BE_ln_009  label="C187_C_0603_1608Metric_6077E391"
  LinkPlacement = pos=(13.875,-38.2125,0) rot=(0,0,-1;1.5708rad)
  LinkedObject = -> Shape
  Placement = pos=(13.875,-38.2125,0) rot=(0,0,-1;1.5708rad)
FEATURE [App::Link] C230_C_1210_3225Metric_6077E91F_ln_027  label="C186_C_1210_3225Metric_6077F381"
  LinkPlacement = pos=(58.625,-38.2125,0) rot=(0,0,-1;1.5708rad)
  LinkedObject = -> Shape001
  Placement = pos=(58.625,-38.2125,0) rot=(0,0,-1;1.5708rad)
FEATURE [App::Link] C230_C_1210_3225Metric_6077E91F_ln_028  label="C184_C_1210_3225Metric_6077F045"
  LinkPlacement = pos=(29.375,-38.2125,0) rot=(0,0,-1;1.5708rad)
  LinkedObject = -> Shape001
  Placement = pos=(29.375,-38.2125,0) rot=(0,0,-1;1.5708rad)
FEATURE [App::Link] C230_C_1210_3225Metric_6077E91F_ln_029  label="C183_C_1210_3225Metric_6077F288"
  LinkPlacement = pos=(16.375,-38.2125,0) rot=(0,0,-1;1.5708rad)
  LinkedObject = -> Shape001
  Placement = pos=(16.375,-38.2125,0) rot=(0,0,-1;1.5708rad)
FEATURE [App::Link] C230_C_1210_3225Metric_6077E91F_ln_030  label="C182_C_1210_3225Metric_6077F906"
  LinkPlacement = pos=(39.125,-38.2125,0) rot=(0,0,-1;1.5708rad)
  LinkedObject = -> Shape001
  Placement = pos=(39.125,-38.2125,0) rot=(0,0,-1;1.5708rad)
FEATURE [App::Link] C230_C_1210_3225Metric_6077E91F_ln_031  label="C180_C_1210_3225Metric_6077F3C3"
  LinkPlacement = pos=(19.625,-38.2125,0) rot=(0,0,-1;1.5708rad)
  LinkedObject = -> Shape001
  Placement = pos=(19.625,-38.2125,0) rot=(0,0,-1;1.5708rad)
FEATURE [App::Link] C230_C_1210_3225Metric_6077E91F_ln_032  label="C179_C_1210_3225Metric_6077E733"
  LinkPlacement = pos=(48.875,-38.2125,0) rot=(0,0,-1;1.5708rad)
  LinkedObject = -> Shape001
  Placement = pos=(48.875,-38.2125,0) rot=(0,0,-1;1.5708rad)
FEATURE [App::Link] C230_C_1210_3225Metric_6077E91F_ln_033  label="C178_C_1210_3225Metric_6077EF9D"
  LinkPlacement = pos=(45.625,-38.2125,0) rot=(0,0,-1;1.5708rad)
  LinkedObject = -> Shape001
  Placement = pos=(45.625,-38.2125,0) rot=(0,0,-1;1.5708rad)
FEATURE [App::Link] C230_C_1210_3225Metric_6077E91F_ln_034  label="C177_C_1210_3225Metric_6077F4EC"
  LinkPlacement = pos=(35.875,-38.2125,0) rot=(0,0,-1;1.5708rad)
  LinkedObject = -> Shape001
  Placement = pos=(35.875,-38.2125,0) rot=(0,0,-1;1.5708rad)
FEATURE [App::Link] C230_C_1210_3225Metric_6077E91F_ln_035  label="C175_C_1210_3225Metric_6077E67C"
  LinkPlacement = pos=(26.125,-38.2125,0) rot=(0,0,-1;1.5708rad)
  LinkedObject = -> Shape001
  Placement = pos=(26.125,-38.2125,0) rot=(0,0,-1;1.5708rad)
FEATURE [App::Link] C230_C_1210_3225Metric_6077E91F_ln_036  label="C174_C_1210_3225Metric_6077FB28"
  LinkPlacement = pos=(52.125,-38.2125,0) rot=(0,0,-1;1.5708rad)
  LinkedObject = -> Shape001
  Placement = pos=(52.125,-38.2125,0) rot=(0,0,-1;1.5708rad)
FEATURE [App::Link] C230_C_1210_3225Metric_6077E91F_ln_037  label="C172_C_1210_3225Metric_6077E61C"
  LinkPlacement = pos=(32.625,-38.2125,0) rot=(0,0,-1;1.5708rad)
  LinkedObject = -> Shape001
  Placement = pos=(32.625,-38.2125,0) rot=(0,0,-1;1.5708rad)
FEATURE [App::Link] C230_C_1210_3225Metric_6077E91F_ln_038  label="C171_C_1210_3225Metric_6077E64C"
  LinkPlacement = pos=(55.375,-38.2125,0) rot=(0,0,-1;1.5708rad)
  LinkedObject = -> Shape001
  Placement = pos=(55.375,-38.2125,0) rot=(0,0,-1;1.5708rad)
FEATURE [App::Link] C230_C_1210_3225Metric_6077E91F_ln_039  label="C170_C_1210_3225Metric_6077F3F3"
  LinkPlacement = pos=(42.375,-38.2125,0) rot=(0,0,-1;1.5708rad)
  LinkedObject = -> Shape001
  Placement = pos=(42.375,-38.2125,0) rot=(0,0,-1;1.5708rad)
FEATURE [App::Link] C230_C_1210_3225Metric_6077E91F_ln_040  label="C169_C_1210_3225Metric_6077F08D"
  LinkPlacement = pos=(22.875,-38.2125,0) rot=(0,0,-1;1.5708rad)
  LinkedObject = -> Shape001
  Placement = pos=(22.875,-38.2125,0) rot=(0,0,-1;1.5708rad)
FEATURE [App::Link] C232_C_0603_1608Metric_6077F2BE_ln_010  label="C167_C_0603_1608Metric_6077F82E"
  LinkPlacement = pos=(61.125,-38.2125,0) rot=(0,0,-1;1.5708rad)
  LinkedObject = -> Shape
  Placement = pos=(61.125,-38.2125,0) rot=(0,0,-1;1.5708rad)
FEATURE [App::Link] C232_C_0603_1608Metric_6077F2BE_ln_011  label="C166_C_0603_1608Metric_6077E982"
  LinkPlacement = pos=(61.125,-31.3125,0) rot=(0,0,-1;1.5708rad)
  LinkedObject = -> Shape
  Placement = pos=(61.125,-31.3125,0) rot=(0,0,-1;1.5708rad)
FEATURE [App::Link] C232_C_0603_1608Metric_6077F2BE_ln_012  label="C165_C_0603_1608Metric_6077ED2D"
  LinkPlacement = pos=(12.375,-31.3125,0) rot=(0,0,-1;1.5708rad)
  LinkedObject = -> Shape
  Placement = pos=(12.375,-31.3125,0) rot=(0,0,-1;1.5708rad)
FEATURE [App::Link] C230_C_1210_3225Metric_6077E91F_ln_041  label="C164_C_1210_3225Metric_6077ED6F"
  LinkPlacement = pos=(16.375,-31.3125,0) rot=(0,0,-1;1.5708rad)
  LinkedObject = -> Shape001
  Placement = pos=(16.375,-31.3125,0) rot=(0,0,-1;1.5708rad)
FEATURE [App::Link] C230_C_1210_3225Metric_6077E91F_ln_042  label="C162_C_1210_3225Metric_6077EE9B"
  LinkPlacement = pos=(19.625,-31.3125,0) rot=(0,0,-1;1.5708rad)
  LinkedObject = -> Shape001
  Placement = pos=(19.625,-31.3125,0) rot=(0,0,-1;1.5708rad)
FEATURE [App::Link] C230_C_1210_3225Metric_6077E91F_ln_043  label="C161_C_1210_3225Metric_6077FA89"
  LinkPlacement = pos=(22.875,-31.3125,0) rot=(0,0,-1;1.5708rad)
  LinkedObject = -> Shape001
  Placement = pos=(22.875,-31.3125,0) rot=(0,0,-1;1.5708rad)
FEATURE [App::Link] C230_C_1210_3225Metric_6077E91F_ln_044  label="C160_C_1210_3225Metric_6077E826"
  LinkPlacement = pos=(35.875,-31.3125,0) rot=(0,0,-1;1.5708rad)
  LinkedObject = -> Shape001
  Placement = pos=(35.875,-31.3125,0) rot=(0,0,-1;1.5708rad)
FEATURE [App::Link] C230_C_1210_3225Metric_6077E91F_ln_045  label="C159_C_1210_3225Metric_6077EBB9"
  LinkPlacement = pos=(26.125,-31.3125,0) rot=(0,0,-1;1.5708rad)
  LinkedObject = -> Shape001
  Placement = pos=(26.125,-31.3125,0) rot=(0,0,-1;1.5708rad)
FEATURE [App::Link] C230_C_1210_3225Metric_6077E91F_ln_046  label="C157_C_1210_3225Metric_6077F23A"
  LinkPlacement = pos=(58.625,-31.3125,0) rot=(0,0,-1;1.5708rad)
  LinkedObject = -> Shape001
  Placement = pos=(58.625,-31.3125,0) rot=(0,0,-1;1.5708rad)
FEATURE [App::Link] C230_C_1210_3225Metric_6077E91F_ln_047  label="C156_C_1210_3225Metric_6077E868"
  LinkPlacement = pos=(42.375,-31.3125,0) rot=(0,0,-1;1.5708rad)
  LinkedObject = -> Shape001
  Placement = pos=(42.375,-31.3125,0) rot=(0,0,-1;1.5708rad)
FEATURE [App::Link] C230_C_1210_3225Metric_6077E91F_ln_048  label="C155_C_1210_3225Metric_6077FCF3"
  LinkPlacement = pos=(29.375,-31.3125,0) rot=(0,0,-1;1.5708rad)
  LinkedObject = -> Shape001
  Placement = pos=(29.375,-31.3125,0) rot=(0,0,-1;1.5708rad)
FEATURE [App::Link] C230_C_1210_3225Metric_6077E91F_ln_049  label="C153_C_1210_3225Metric_6077E9BE"
  LinkPlacement = pos=(48.875,-31.3125,0) rot=(0,0,-1;1.5708rad)
  LinkedObject = -> Shape001
  Placement = pos=(48.875,-31.3125,0) rot=(0,0,-1;1.5708rad)
FEATURE [App::Link] C230_C_1210_3225Metric_6077E91F_ln_050  label="C152_C_1210_3225Metric_6077E26E"
  LinkPlacement = pos=(32.625,-31.3125,0) rot=(0,0,-1;1.5708rad)
  LinkedObject = -> Shape001
  Placement = pos=(32.625,-31.3125,0) rot=(0,0,-1;1.5708rad)
FEATURE [App::Link] C230_C_1210_3225Metric_6077E91F_ln_051  label="C151_C_1210_3225Metric_6077ECFD"
  LinkPlacement = pos=(39.125,-31.3125,0) rot=(0,0,-1;1.5708rad)
  LinkedObject = -> Shape001
  Placement = pos=(39.125,-31.3125,0) rot=(0,0,-1;1.5708rad)
FEATURE [App::Link] C230_C_1210_3225Metric_6077E91F_ln_052  label="C150_C_1210_3225Metric_6077E89B"
  LinkPlacement = pos=(52.125,-31.3125,0) rot=(0,0,-1;1.5708rad)
  LinkedObject = -> Shape001
  Placement = pos=(52.125,-31.3125,0) rot=(0,0,-1;1.5708rad)
FEATURE [App::Link] C230_C_1210_3225Metric_6077E91F_ln_053  label="C149_C_1210_3225Metric_6077F6A5"
  LinkPlacement = pos=(45.625,-31.3125,0) rot=(0,0,-1;1.5708rad)
  LinkedObject = -> Shape001
  Placement = pos=(45.625,-31.3125,0) rot=(0,0,-1;1.5708rad)
FEATURE [App::Link] C230_C_1210_3225Metric_6077E91F_ln_054  label="C148_C_1210_3225Metric_6077E34C"
  LinkPlacement = pos=(55.375,-31.3125,0) rot=(0,0,-1;1.5708rad)
  LinkedObject = -> Shape001
  Placement = pos=(55.375,-31.3125,0) rot=(0,0,-1;1.5708rad)
FEATURE [App::Link] C232_C_0603_1608Metric_6077F2BE_ln_013  label="C146_C_0603_1608Metric_6077E3FA"
  LinkPlacement = pos=(62.625,-31.3125,0) rot=(0,0,-1;1.5708rad)
  LinkedObject = -> Shape
  Placement = pos=(62.625,-31.3125,0) rot=(0,0,-1;1.5708rad)
FEATURE [App::Link] C232_C_0603_1608Metric_6077F2BE_ln_014  label="C145_C_0603_1608Metric_6077ECCA"
  LinkPlacement = pos=(13.875,-31.3125,0) rot=(0,0,-1;1.5708rad)
  LinkedObject = -> Shape
  Placement = pos=(13.875,-31.3125,0) rot=(0,0,-1;1.5708rad)
FEATURE [App::Link] C232_C_0603_1608Metric_6077F2BE_ln_015  label="C144_C_0603_1608Metric_6077E2DD"
  LinkPlacement = pos=(12.375,-17.65,0) rot=(0,0,-1;1.5708rad)
  LinkedObject = -> Shape
  Placement = pos=(12.375,-17.65,0) rot=(0,0,-1;1.5708rad)
FEATURE [App::Link] C232_C_0603_1608Metric_6077F2BE_ln_016  label="C143_C_0603_1608Metric_6077E439"
  LinkPlacement = pos=(13.875,-17.65,0) rot=(0,0,-1;1.5708rad)
  LinkedObject = -> Shape
  Placement = pos=(13.875,-17.65,0) rot=(0,0,-1;1.5708rad)
FEATURE [App::Link] C230_C_1210_3225Metric_6077E91F_ln_055  label="C142_C_1210_3225Metric_6077E4F6"
  LinkPlacement = pos=(52.125,-17.65,0) rot=(0,0,-1;1.5708rad)
  LinkedObject = -> Shape001
  Placement = pos=(52.125,-17.65,0) rot=(0,0,-1;1.5708rad)
FEATURE [App::Link] C230_C_1210_3225Metric_6077E91F_ln_056  label="C141_C_1210_3225Metric_6077FC78"
  LinkPlacement = pos=(35.875,-17.65,0) rot=(0,0,-1;1.5708rad)
  LinkedObject = -> Shape001
  Placement = pos=(35.875,-17.65,0) rot=(0,0,-1;1.5708rad)
FEATURE [App::Link] C230_C_1210_3225Metric_6077E91F_ln_057  label="C140_C_1210_3225Metric_6077F76E"
  LinkPlacement = pos=(22.875,-17.65,0) rot=(0,0,-1;1.5708rad)
  LinkedObject = -> Shape001
  Placement = pos=(22.875,-17.65,0) rot=(0,0,-1;1.5708rad)
FEATURE [App::Link] C230_C_1210_3225Metric_6077E91F_ln_058  label="C139_C_1210_3225Metric_6077F891"
  LinkPlacement = pos=(55.375,-17.65,0) rot=(0,0,-1;1.5708rad)
  LinkedObject = -> Shape001
  Placement = pos=(55.375,-17.65,0) rot=(0,0,-1;1.5708rad)
FEATURE [App::Link] C230_C_1210_3225Metric_6077E91F_ln_059  label="C138_C_1210_3225Metric_6077F423"
  LinkPlacement = pos=(42.375,-17.65,0) rot=(0,0,-1;1.5708rad)
  LinkedObject = -> Shape001
  Placement = pos=(42.375,-17.65,0) rot=(0,0,-1;1.5708rad)
FEATURE [App::Link] C230_C_1210_3225Metric_6077E91F_ln_060  label="C137_C_1210_3225Metric_6077FBAC"
  LinkPlacement = pos=(29.375,-17.65,0) rot=(0,0,-1;1.5708rad)
  LinkedObject = -> Shape001
  Placement = pos=(29.375,-17.65,0) rot=(0,0,-1;1.5708rad)
FEATURE [App::Link] C230_C_1210_3225Metric_6077E91F_ln_061  label="C135_C_1210_3225Metric_6077F16B"
  LinkPlacement = pos=(58.625,-17.65,0) rot=(0,0,-1;1.5708rad)
  LinkedObject = -> Shape001
  Placement = pos=(58.625,-17.65,0) rot=(0,0,-1;1.5708rad)
FEATURE [App::Link] C230_C_1210_3225Metric_6077E91F_ln_062  label="C134_C_1210_3225Metric_6077E76F"
  LinkPlacement = pos=(48.875,-17.65,0) rot=(0,0,-1;1.5708rad)
  LinkedObject = -> Shape001
  Placement = pos=(48.875,-17.65,0) rot=(0,0,-1;1.5708rad)
FEATURE [App::Link] C230_C_1210_3225Metric_6077E91F_ln_063  label="C131_C_1210_3225Metric_6077F5A3"
  LinkPlacement = pos=(19.625,-17.65,0) rot=(0,0,-1;1.5708rad)
  LinkedObject = -> Shape001
  Placement = pos=(19.625,-17.65,0) rot=(0,0,-1;1.5708rad)
FEATURE [App::Link] C230_C_1210_3225Metric_6077E91F_ln_064  label="C129_C_1210_3225Metric_6077F73B"
  LinkPlacement = pos=(39.125,-17.65,0) rot=(0,0,-1;1.5708rad)
  LinkedObject = -> Shape001
  Placement = pos=(39.125,-17.65,0) rot=(0,0,-1;1.5708rad)
FEATURE [App::Link] C230_C_1210_3225Metric_6077E91F_ln_065  label="C128_C_1210_3225Metric_6077F7FE"
  LinkPlacement = pos=(26.125,-17.65,0) rot=(0,0,-1;1.5708rad)
  LinkedObject = -> Shape001
  Placement = pos=(26.125,-17.65,0) rot=(0,0,-1;1.5708rad)
FEATURE [App::Link] C230_C_1210_3225Metric_6077E91F_ln_066  label="C127_C_1210_3225Metric_6077F009"
  LinkPlacement = pos=(45.625,-17.65,0) rot=(0,0,-1;1.5708rad)
  LinkedObject = -> Shape001
  Placement = pos=(45.625,-17.65,0) rot=(0,0,-1;1.5708rad)
FEATURE [App::Link] C230_C_1210_3225Metric_6077E91F_ln_067  label="C126_C_1210_3225Metric_6077F603"
  LinkPlacement = pos=(32.625,-17.65,0) rot=(0,0,-1;1.5708rad)
  LinkedObject = -> Shape001
  Placement = pos=(32.625,-17.65,0) rot=(0,0,-1;1.5708rad)
FEATURE [App::Link] C230_C_1210_3225Metric_6077E91F_ln_068  label="C125_C_1210_3225Metric_6077F31E"
  LinkPlacement = pos=(16.375,-17.65,0) rot=(0,0,-1;1.5708rad)
  LinkedObject = -> Shape001
  Placement = pos=(16.375,-17.65,0) rot=(0,0,-1;1.5708rad)
FEATURE [App::Link] C232_C_0603_1608Metric_6077F2BE_ln_017  label="C124_C_0603_1608Metric_6077F1AA"
  LinkPlacement = pos=(61.125,-17.65,0) rot=(0,0,-1;1.5708rad)
  LinkedObject = -> Shape
  Placement = pos=(61.125,-17.65,0) rot=(0,0,-1;1.5708rad)
FEATURE [App::Link] C232_C_0603_1608Metric_6077F2BE_ln_018  label="C123_C_0603_1608Metric_6077F531"
  LinkPlacement = pos=(62.625,-17.65,0) rot=(0,0,-1;1.5708rad)
  LinkedObject = -> Shape
  Placement = pos=(62.625,-17.65,0) rot=(0,0,-1;1.5708rad)
FEATURE [App::Link] C232_C_0603_1608Metric_6077F2BE_ln_019  label="C122_C_0603_1608Metric_6077F2EE"
  LinkPlacement = pos=(12.375,-3.9,0) rot=(0,0,-1;1.5708rad)
  LinkedObject = -> Shape
  Placement = pos=(12.375,-3.9,0) rot=(0,0,-1;1.5708rad)
FEATURE [App::Link] C232_C_0603_1608Metric_6077F2BE_ln_020  label="C121_C_0603_1608Metric_6077F85E"
  LinkPlacement = pos=(13.875,-3.9,0) rot=(0,0,-1;1.5708rad)
  LinkedObject = -> Shape
  Placement = pos=(13.875,-3.9,0) rot=(0,0,-1;1.5708rad)
FEATURE [App::Link] C230_C_1210_3225Metric_6077E91F_ln_069  label="C120_C_1210_3225Metric_6077F945"
  LinkPlacement = pos=(16.375,-3.9,0) rot=(0,0,-1;1.5708rad)
  LinkedObject = -> Shape001
  Placement = pos=(16.375,-3.9,0) rot=(0,0,-1;1.5708rad)
FEATURE [App::Link] C230_C_1210_3225Metric_6077E91F_ln_070  label="C119_C_1210_3225Metric_6077E52C"
  LinkPlacement = pos=(19.625,-3.9,0) rot=(0,0,-1;1.5708rad)
  LinkedObject = -> Shape001
  Placement = pos=(19.625,-3.9,0) rot=(0,0,-1;1.5708rad)
FEATURE [App::Link] C230_C_1210_3225Metric_6077E91F_ln_071  label="C118_C_1210_3225Metric_6077E4B4"
  LinkPlacement = pos=(22.875,-3.9,0) rot=(0,0,-1;1.5708rad)
  LinkedObject = -> Shape001
  Placement = pos=(22.875,-3.9,0) rot=(0,0,-1;1.5708rad)
FEATURE [App::Link] C230_C_1210_3225Metric_6077E91F_ln_072  label="C117_C_1210_3225Metric_6077F97B"
  LinkPlacement = pos=(26.125,-3.9,0) rot=(0,0,-1;1.5708rad)
  LinkedObject = -> Shape001
  Placement = pos=(26.125,-3.9,0) rot=(0,0,-1;1.5708rad)
FEATURE [App::Link] C230_C_1210_3225Metric_6077E91F_ln_073  label="C116_C_1210_3225Metric_6077E6C1"
  LinkPlacement = pos=(29.375,-3.9,0) rot=(0,0,-1;1.5708rad)
  LinkedObject = -> Shape001
  Placement = pos=(29.375,-3.9,0) rot=(0,0,-1;1.5708rad)
FEATURE [App::Link] C230_C_1210_3225Metric_6077E91F_ln_074  label="C115_C_1210_3225Metric_6077F5D3"
  LinkPlacement = pos=(32.625,-3.9,0) rot=(0,0,-1;1.5708rad)
  LinkedObject = -> Shape001
  Placement = pos=(32.625,-3.9,0) rot=(0,0,-1;1.5708rad)
FEATURE [App::Link] C230_C_1210_3225Metric_6077E91F_ln_075  label="C110_C_1210_3225Metric_6077E1C6"
  LinkPlacement = pos=(35.875,-3.9,0) rot=(0,0,-1;1.5708rad)
  LinkedObject = -> Shape001
  Placement = pos=(35.875,-3.9,0) rot=(0,0,-1;1.5708rad)
FEATURE [App::Link] C230_C_1210_3225Metric_6077E91F_ln_076  label="C109_C_1210_3225Metric_6077E571"
  LinkPlacement = pos=(39.125,-3.9,0) rot=(0,0,-1;1.5708rad)
  LinkedObject = -> Shape001
  Placement = pos=(39.125,-3.9,0) rot=(0,0,-1;1.5708rad)
FEATURE [App::Link] C230_C_1210_3225Metric_6077E91F_ln_077  label="C108_C_1210_3225Metric_6077FCC3"
  LinkPlacement = pos=(42.375,-3.9,0) rot=(0,0,-1;1.5708rad)
  LinkedObject = -> Shape001
  Placement = pos=(42.375,-3.9,0) rot=(0,0,-1;1.5708rad)
FEATURE [App::Link] C230_C_1210_3225Metric_6077E91F_ln_078  label="C107_C_1210_3225Metric_6077EC19"
  LinkPlacement = pos=(45.625,-3.9,0) rot=(0,0,-1;1.5708rad)
  LinkedObject = -> Shape001
  Placement = pos=(45.625,-3.9,0) rot=(0,0,-1;1.5708rad)
FEATURE [App::Link] C230_C_1210_3225Metric_6077E91F_ln_079  label="C106_C_1210_3225Metric_6077EE62"
  LinkPlacement = pos=(48.875,-3.9,0) rot=(0,0,-1;1.5708rad)
  LinkedObject = -> Shape001
  Placement = pos=(48.875,-3.9,0) rot=(0,0,-1;1.5708rad)
FEATURE [App::Link] C230_C_1210_3225Metric_6077E91F_ln_080  label="C105_C_1210_3225Metric_6077F108"
  LinkPlacement = pos=(52.125,-3.9,0) rot=(0,0,-1;1.5708rad)
  LinkedObject = -> Shape001
  Placement = pos=(52.125,-3.9,0) rot=(0,0,-1;1.5708rad)
FEATURE [App::Link] C230_C_1210_3225Metric_6077E91F_ln_081  label="C104_C_1210_3225Metric_6077FAD7"
  LinkPlacement = pos=(55.375,-3.9,0) rot=(0,0,-1;1.5708rad)
  LinkedObject = -> Shape001
  Placement = pos=(55.375,-3.9,0) rot=(0,0,-1;1.5708rad)
FEATURE [App::Link] C230_C_1210_3225Metric_6077E91F_ln_082  label="C103_C_1210_3225Metric_6077EB1A"
  LinkPlacement = pos=(58.625,-3.9,0) rot=(0,0,-1;1.5708rad)
  LinkedObject = -> Shape001
  Placement = pos=(58.625,-3.9,0) rot=(0,0,-1;1.5708rad)
FEATURE [App::Link] C232_C_0603_1608Metric_6077F2BE_ln_021  label="C102_C_0603_1608Metric_6077EE2F"
  LinkPlacement = pos=(62.625,-3.9,0) rot=(0,0,-1;1.5708rad)
  LinkedObject = -> Shape
  Placement = pos=(62.625,-3.9,0) rot=(0,0,-1;1.5708rad)
FEATURE [App::Link] C232_C_0603_1608Metric_6077F2BE_ln_022  label="C101_C_0603_1608Metric_6077F8CA"
  LinkPlacement = pos=(61.125,-3.9,0) rot=(0,0,-1;1.5708rad)
  LinkedObject = -> Shape
  Placement = pos=(61.125,-3.9,0) rot=(0,0,-1;1.5708rad)
FEATURE [App::LinkGroup] Top_1fb6
  ElementList = -> [Shape,C232_C_0603_1608Metric_6077F2BE_ln_,Shape001,C230_C_1210_3225Metric_6077E91F_ln_,C230_C_1210_3225Metric_6077E91F_ln_001,C230_C_1210_3225Metric_6077E91F_ln_002,C230_C_1210_3225Metric_6077E91F_ln_003,C230_C_1210_3225Metric_6077E91F_ln_004,C230_C_1210_3225Metric_6077E91F_ln_005,C230_C_1210_3225Metric_6077E91F_ln_006,C230_C_1210_3225Metric_6077E91F_ln_007,C230_C_1210_3225Metric_6077E91F_ln_008,+96 more]
  LinkMode = 0
FEATURE [App::LinkGroup] Step_Models_1fb6
  ElementList = -> [Top_1fb6]
  LinkMode = 0
FEATURE [App::LinkGroup] Board_1fb6  label="Caps"
  ElementList = -> [Board_Geoms_1fb6,Step_Models_1fb6]
  LinkMode = 0
FEATURE [PartDesign::CoordinateSystem] LCS_0
  AttacherType = Attacher::AttachEngine3D
  MapMode = 2
  Support = -> [X_Axis]
FEATURE [PartDesign::Line] HoleAxis_1
  AttacherType = Attacher::AttachEngineLine
  Length = 4.50902
  MapMode = 19
  Placement = pos=(67,-38.5,0) rot=(0,0,1;0rad)
  ResizeMode = 1
  Support = -> [Pcb_1fb6]
FEATURE [PartDesign::Line] HoleAxis_2
  AttacherType = Attacher::AttachEngineLine
  Length = 4.50902
  MapMode = 19
  Placement = pos=(67,-26.8333,0) rot=(0,0,1;0rad)
  ResizeMode = 1
  Support = -> [Pcb_1fb6]
FEATURE [PartDesign::Line] HoleAxis_3
  AttacherType = Attacher::AttachEngineLine
  Length = 4.50902
  MapMode = 19
  Placement = pos=(67,-15.1667,0) rot=(0,0,1;0rad)
  ResizeMode = 1
  Support = -> [Pcb_1fb6]
FEATURE [PartDesign::Line] HoleAxis_4
  AttacherType = Attacher::AttachEngineLine
  Length = 4.50902
  MapMode = 19
  Placement = pos=(67,-3.5,0) rot=(0,0,1;0rad)
  ResizeMode = 1
  Support = -> [Pcb_1fb6]
FEATURE [PartDesign::Line] HoleAxis_5
  AttacherType = Attacher::AttachEngineLine
  Length = 4.50902
  MapMode = 19
  Placement = pos=(8,-3.5,0) rot=(0,0,1;0rad)
  ResizeMode = 1
  Support = -> [Pcb_1fb6]
FEATURE [PartDesign::Line] HoleAxis_6
  AttacherType = Attacher::AttachEngineLine
  Length = 4.50902
  MapMode = 19
  Placement = pos=(8,-15.1667,0) rot=(0,0,1;0rad)
  ResizeMode = 1
  Support = -> [Pcb_1fb6]
FEATURE [PartDesign::Line] HoleAxis_7
  AttacherType = Attacher::AttachEngineLine
  Length = 4.50902
  MapMode = 19
  Placement = pos=(8,-26.8333,0) rot=(0,0,1;0rad)
  ResizeMode = 1
  Support = -> [Pcb_1fb6]
FEATURE [PartDesign::Line] HoleAxis_8
  AttacherType = Attacher::AttachEngineLine
  Length = 4.50902
  MapMode = 19
  Placement = pos=(8,-38.5,0) rot=(0,0,1;0rad)
  ResizeMode = 1
  Support = -> [Pcb_1fb6]
FEATURE [App::Part] Part
  Group = -> [LCS_0,C230_C_1210_3225Metric_6077E91F_ln_061,C230_C_1210_3225Metric_6077E91F_ln_040,C230_C_1210_3225Metric_6077E91F_ln_068,C230_C_1210_3225Metric_6077E91F_ln_008,C230_C_1210_3225Metric_6077E91F_ln_027,C230_C_1210_3225Metric_6077E91F_ln_072,C232_C_0603_1608Metric_6077F2BE_ln_021,C232_C_0603_1608Metric_6077F2BE_ln_017,C230_C_1210_3225Metric_6077E91F_ln_041,C230_C_1210_3225Metric_6077E91F_ln_052,+113 more]
  Origin = -> Origin
---- part controle.FCStd = doc fcstd_db1a329fb71e ----
FCSTD DOCUMENT  (FreeCAD 0.19R24276 (Git))
Label: controle
License: Creative Commons Attribution-NonCommercial-ShareAlike
LicenseURL: http://creativecommons.org/licenses/by-nc-sa/4.0/
objects: App::Link×24, Part::Feature×19, App::LinkGroup×8, PartDesign::Line×4, PartDesign::CoordinateSystem×2, Sketcher::SketchObject×1, App::Part×1
note: 26 computed .brp shape members not serialized (recipe doc carries the construction recipe); baked Part::Feature solids carry a one-line shape summary decoded from their .brp

FEATURE [PartDesign::CoordinateSystem] Local_CS_266e
  AttacherType = Attacher::AttachEngine3D
FEATURE [Part::Feature] Pcb_266e
  Placement = pos=(-125.663,89.27,0) rot=(0,0,1;0rad)
  shape: bbox 75 x 36.09 x 1.6 mm, 22 faces (baked)
FEATURE [Sketcher::SketchObject] PCB_Sketch_266e
  FullyConstrained = false
  sketch-geometry (4):
    g0: LineSegment StartX=70.0635 StartY=0.77064 StartZ=0 EndX=-4.94 EndY=0.77 EndZ=0
    g1: LineSegment StartX=70.0635 StartY=36.856 StartZ=0 EndX=70.0635 EndY=0.77064 EndZ=0
    g2: LineSegment StartX=-4.94 StartY=36.856 StartZ=0 EndX=70.0635 EndY=36.856 EndZ=0
    g3: LineSegment StartX=-4.94 StartY=0.77 StartZ=0 EndX=-4.94 EndY=36.856 EndZ=0
  constraints (4):
    c: Coincident(g0,g3)
    c: Coincident(g2,g3)
    c: Coincident(g0,g1)
    c: Coincident(g1,g2)
FEATURE [App::LinkGroup] Board_Geoms_266e
  ElementList = -> [Pcb_266e,Local_CS_266e,PCB_Sketch_266e]
  LinkMode = 0
FEATURE [App::LinkGroup] TopV_266e
  LinkMode = 0
FEATURE [App::LinkGroup] BotV_266e
  LinkMode = 0
FEATURE [App::LinkGroup] Step_Virtual_Models_266e
  ElementList = -> [TopV_266e,BotV_266e]
  LinkMode = 0
FEATURE [Part::Feature] Shape  label="R103_R_0603_1608Metric_607532D5"
  Placement = pos=(35.1841,22.092,0) rot=(0,0,-1;1.5708rad)
  shape: bbox 0.8 x 1.6 x 0.45 mm, 26 faces (baked)
FEATURE [Part::Feature] Shape001  label="J103_PinHeader_1x02_P254mm_Vertical_SMD_Pin1Left_60752E1C"
  Placement = pos=(33.1521,26.537,0) rot=(0,0,1;0rad)
  shape: bbox 5 x 5.08 x 9.3 mm, 58 faces (baked)
FEATURE [App::Link] R103_R_0603_1608Metric_607532D5_ln_  label="R102_R_0603_1608Metric_60753017"
  LinkPlacement = pos=(38.8671,17.266,0) rot=(0,0,1;3.14159rad)
  LinkedObject = -> Shape
  Placement = pos=(38.8671,17.266,0) rot=(0,0,1;3.14159rad)
FEATURE [App::Link] R103_R_0603_1608Metric_607532D5_ln_001  label="R101_R_0603_1608Metric_60753692"
  LinkPlacement = pos=(37.9781,24.505,0) rot=(0,0,1;3.14159rad)
  LinkedObject = -> Shape
  Placement = pos=(37.9781,24.505,0) rot=(0,0,1;3.14159rad)
FEATURE [Part::Feature] Shape002  label="Q101_SOT_23_6075318C"
  Placement = pos=(37.8511,20.949,0) rot=(0,0,1;1.5708rad)
  shape: bbox 3 x 2.5 x 1.2 mm, 76 faces (baked)
FEATURE [Part::Feature] Shape003  label="C104_C_1206_3216Metric_60753A85"
  Placement = pos=(55.7581,30.22,0) rot=(0,0,1;3.14159rad)
  shape: bbox 3.2 x 1.6 x 1.6 mm, 28 faces (baked)
FEATURE [App::Link] C104_C_1206_3216Metric_60753A85_ln_  label="C103_C_1206_3216Metric_60752CED"
  LinkPlacement = pos=(40.8991,21.838,0) rot=(0,0,1;1.5708rad)
  LinkedObject = -> Shape003
  Placement = pos=(40.8991,21.838,0) rot=(0,0,1;1.5708rad)
FEATURE [App::Link] C104_C_1206_3216Metric_60753A85_ln_001  label="C102_C_1206_3216Metric_60752EF7"
  LinkPlacement = pos=(43.3121,21.838,0) rot=(0,0,1;1.5708rad)
  LinkedObject = -> Shape003
  Placement = pos=(43.3121,21.838,0) rot=(0,0,1;1.5708rad)
FEATURE [App::Link] C104_C_1206_3216Metric_60753A85_ln_002  label="C12_C_1206_3216Metric_60752D4D"
  LinkPlacement = pos=(57.7393,7.25838,0) rot=(0,0,1;3.14159rad)
  LinkedObject = -> Shape003
  Placement = pos=(57.7393,7.25838,0) rot=(0,0,1;3.14159rad)
FEATURE [App::Link] C104_C_1206_3216Metric_60753A85_ln_003  label="C7_C_1206_3216Metric_60752DAD"
  LinkPlacement = pos=(45.8521,21.711,0) rot=(0,0,-1;1.5708rad)
  LinkedObject = -> Shape003
  Placement = pos=(45.8521,21.711,0) rot=(0,0,-1;1.5708rad)
FEATURE [App::Link] C104_C_1206_3216Metric_60753A85_ln_004  label="C6_C_1206_3216Metric_60752E64"
  LinkPlacement = pos=(27.6911,26.41,0) rot=(0,0,-1;1.5708rad)
  LinkedObject = -> Shape003
  Placement = pos=(27.6911,26.41,0) rot=(0,0,-1;1.5708rad)
FEATURE [App::Link] C104_C_1206_3216Metric_60753A85_ln_005  label="C5_C_1206_3216Metric_60752F27"
  LinkPlacement = pos=(27.6911,31.617,0) rot=(0,0,1;1.5708rad)
  LinkedObject = -> Shape003
  Placement = pos=(27.6911,31.617,0) rot=(0,0,1;1.5708rad)
FEATURE [App::Link] C104_C_1206_3216Metric_60753A85_ln_006  label="C4_C_1206_3216Metric_60753077"
  LinkPlacement = pos=(37.8511,29.839,0) rot=(0,0,1;3.14159rad)
  LinkedObject = -> Shape003
  Placement = pos=(37.8511,29.839,0) rot=(0,0,1;3.14159rad)
FEATURE [App::Link] C104_C_1206_3216Metric_60753A85_ln_007  label="C3_C_1206_3216Metric_60752E94"
  LinkPlacement = pos=(50.4241,30.22,0) rot=(0,0,1;3.14159rad)
  LinkedObject = -> Shape003
  Placement = pos=(50.4241,30.22,0) rot=(0,0,1;3.14159rad)
FEATURE [App::Link] C104_C_1206_3216Metric_60753A85_ln_008  label="C2_C_1206_3216Metric_60753755"
  LinkPlacement = pos=(64.7751,26.029,0) rot=(0,0,1;3.14159rad)
  LinkedObject = -> Shape003
  Placement = pos=(64.7751,26.029,0) rot=(0,0,1;3.14159rad)
FEATURE [App::Link] C104_C_1206_3216Metric_60753A85_ln_009  label="C1_C_1206_3216Metric_60752D7D"
  LinkPlacement = pos=(55.7581,32.76,0) rot=(0,0,1;3.14159rad)
  LinkedObject = -> Shape003
  Placement = pos=(55.7581,32.76,0) rot=(0,0,1;3.14159rad)
FEATURE [Part::Feature] Shape004  label="U401_SOT_89_3_607525BD"
  Placement = pos=(64.2671,22.092,0) rot=(0,0,-1;1.5708rad)
  shape: bbox 4.5 x 4 x 1.52 mm, 43 faces (baked)
FEATURE [Part::Feature] Shape005  label="J102_PinHeader_1x05_P254mm_Vertical_SMD_Pin1Left_607527F2"
  Placement = pos=(22.7381,7.10598,0) rot=(0,0,1;1.5708rad)
  shape: bbox 12.7 x 5 x 9.3 mm, 139 faces (baked)
FEATURE [Part::Feature] Shape006  label="D102_D_SOD_123F_60752671"
  Placement = pos=(37.8511,27.299,0) rot=(0,0,1;3.14159rad)
  shape: bbox 3.5 x 1.6 x 1.1 mm, 27 faces (baked)
FEATURE [Part::Feature] Shape007  label="U601_SOIC_8_39x49mm_P127mm_6075390B"
  Placement = pos=(56.2661,12.821,0) rot=(0,0,1;3.14159rad)
  shape: bbox 6 x 4.9 x 1.75 mm, 156 faces (baked)
FEATURE [Part::Feature] Shape008  label="D501_LED_0603_1608Metric_6077B07B"
  Placement = pos=(49.7841,6.40898,0) rot=(0,0,1;3.14159rad)
  shape: bbox 1.6 x 0.8 x 1.1 mm, 50 faces (baked)
FEATURE [App::Link] R103_R_0603_1608Metric_607532D5_ln_002  label="R502_R_0603_1608Metric_6077B043"
  LinkPlacement = pos=(49.7841,7.91878,0) rot=(0,0,1;0rad)
  LinkedObject = -> Shape
  Placement = pos=(49.7841,7.91878,0) rot=(0,0,1;0rad)
FEATURE [Part::Feature] Shape009  label="U501_LQFP_48_7x7mm_P05mm_607528ED"
  Placement = pos=(44.8361,13.329,0) rot=(0,0,1;2.35619rad)
  shape: bbox 10.41 x 10.41 x 1.5 mm, 764 faces (baked)
FEATURE [App::Link] R103_R_0603_1608Metric_607532D5_ln_003  label="R505_R_0603_1608Metric_60752576"
  LinkPlacement = pos=(41.5341,6.08998,0) rot=(0,0,1;1.5708rad)
  LinkedObject = -> Shape
  Placement = pos=(41.5341,6.08998,0) rot=(0,0,1;1.5708rad)
FEATURE [Part::Feature] Shape010  label="R504_R_0402_1005Metric_6075253D"
  Placement = pos=(43.3121,4.94698,0) rot=(0,0,1;3.14159rad)
  shape: bbox 1 x 0.5 x 0.35 mm, 26 faces (baked)
FEATURE [Part::Feature] Shape011  label="J101_PinHeader_1x04_P254mm_Vertical_SMD_Pin1Left_60752A18"
  Placement = pos=(35.3111,7.10598,0) rot=(0,0,1;1.5708rad)
  shape: bbox 10.16 x 5 x 9.3 mm, 112 faces (baked)
FEATURE [Part::Feature] Shape012  label="C201_C_0603_1608Metric_6075323F"
  Placement = pos=(34.2686,19.674,0) rot=(0,0,1;0rad)
  shape: bbox 1.6 x 0.8 x 0.8 mm, 28 faces (baked)
FEATURE [App::Link] R103_R_0603_1608Metric_607532D5_ln_004  label="R205_R_0603_1608Metric_60752B49"
  LinkPlacement = pos=(28.8341,22.854,0) rot=(0,0,1;0rad)
  LinkedObject = -> Shape
  Placement = pos=(28.8341,22.854,0) rot=(0,0,1;0rad)
FEATURE [App::Link] R103_R_0603_1608Metric_607532D5_ln_005  label="R204_R_0603_1608Metric_60752A9B"
  LinkPlacement = pos=(31.5011,20.314,0) rot=(0,0,-1;1.5708rad)
  LinkedObject = -> Shape
  Placement = pos=(31.5011,20.314,0) rot=(0,0,-1;1.5708rad)
FEATURE [App::Link] R103_R_0603_1608Metric_607532D5_ln_006  label="R203_R_0603_1608Metric_60752C51"
  LinkPlacement = pos=(29.8501,20.314,0) rot=(0,0,-1;1.5708rad)
  LinkedObject = -> Shape
  Placement = pos=(29.8501,20.314,0) rot=(0,0,-1;1.5708rad)
FEATURE [App::Link] C201_C_0603_1608Metric_6075323F_ln_  label="C202_C_0603_1608Metric_607526B4"
  LinkPlacement = pos=(32.3901,22.854,0) rot=(0,0,1;0rad)
  LinkedObject = -> Shape012
  Placement = pos=(32.3901,22.854,0) rot=(0,0,1;0rad)
FEATURE [Part::Feature] Shape013  label="U403_TO-220-3_Horizontal_TabDown_607524A3"
  Placement = pos=(23.1191,30.601,0) rot=(0,0,1;3.14159rad)
  shape: bbox 10.25 x 19.74 x 10.78 mm, 80 faces (baked)
FEATURE [Part::Feature] Shape014  label="U402_SOT_223_6075262C"
  Placement = pos=(44.2011,29.204,0) rot=(0,0,-1;1.5708rad)
  shape: bbox 6.5 x 7 x 1.7 mm, 78 faces (baked)
FEATURE [App::Link] D102_D_SOD_123F_60752671_ln_  label="D101_D_SOD_123F_6075328F"
  LinkPlacement = pos=(10.4191,31.998,0) rot=(0,0,1;3.14159rad)
  LinkedObject = -> Shape006
  Placement = pos=(10.4191,31.998,0) rot=(0,0,1;3.14159rad)
FEATURE [App::Link] C201_C_0603_1608Metric_6075323F_ln_001  label="C11_C_0603_1608Metric_60753953"
  LinkPlacement = pos=(47.2491,5.96298,0) rot=(0,0,1;1.5708rad)
  LinkedObject = -> Shape012
  Placement = pos=(47.2491,5.96298,0) rot=(0,0,1;1.5708rad)
FEATURE [App::Link] C201_C_0603_1608Metric_6075323F_ln_002  label="C9_C_0603_1608Metric_60752F87"
  LinkPlacement = pos=(48.7731,19.806,0) rot=(0,0,1;3.14159rad)
  LinkedObject = -> Shape012
  Placement = pos=(48.7731,19.806,0) rot=(0,0,1;3.14159rad)
FEATURE [App::Link] C201_C_0603_1608Metric_6075323F_ln_003  label="C10_C_0603_1608Metric_6075386F"
  LinkPlacement = pos=(38.1051,13.329,0) rot=(0,0,-1;1.5708rad)
  LinkedObject = -> Shape012
  Placement = pos=(38.1051,13.329,0) rot=(0,0,-1;1.5708rad)
FEATURE [Part::Feature] Shape015  label="J107_PinSocket_2x10_P127mm_Vertical_SMD_606F5D48"
  Placement = pos=(48.5634,18.7697,-1.6) rot=(0,1,0;3.14159rad)
  shape: bbox 5.185 x 12.7 x 4.825 mm, 710 faces (baked)
FEATURE [App::LinkGroup] Bot_266e
  ElementList = -> [Shape015]
  LinkMode = 0
FEATURE [Part::Feature] Shape016  label="J106_PinHeader_1x03_P254mm_Vertical_SMD_Pin1Left_607539D0"
  Placement = pos=(57.4091,24.505,0) rot=(0,0,1;0rad)
  shape: bbox 5 x 7.62 x 9.3 mm, 85 faces (baked)
FEATURE [App::Link] J106_PinHeader_1x03_P254mm_Vertical_SMD_Pin1Left_607539D0_ln_  label="J105_PinHeader_1x03_P254mm_Vertical_SMD_Pin1Left_60753A33"
  LinkPlacement = pos=(51.4401,24.505,0) rot=(0,0,1;0rad)
  LinkedObject = -> Shape016
  Placement = pos=(51.4401,24.505,0) rot=(0,0,1;0rad)
FEATURE [App::Link] C201_C_0603_1608Metric_6075323F_ln_004  label="C8_C_0603_1608Metric_60753047"
  LinkPlacement = pos=(44.0741,6.34398,0) rot=(0,0,1;0rad)
  LinkedObject = -> Shape012
  Placement = pos=(44.0741,6.34398,0) rot=(0,0,1;0rad)
FEATURE [Part::Feature] _15008142621_1_fd_cp  label="615008142621_1_sp"
  Placement = pos=(2.5,18.2,6.5) rot=(0,0,-1;1.5708rad)
  shape: bbox 21.2 x 15.88 x 17.34 mm, 703 faces (baked)
FEATURE [App::LinkGroup] Top_266e
  ElementList = -> [Shape,Shape001,R103_R_0603_1608Metric_607532D5_ln_,R103_R_0603_1608Metric_607532D5_ln_001,Shape002,Shape003,C104_C_1206_3216Metric_60753A85_ln_,C104_C_1206_3216Metric_60753A85_ln_001,C104_C_1206_3216Metric_60753A85_ln_002,C104_C_1206_3216Metric_60753A85_ln_003,C104_C_1206_3216Metric_60753A85_ln_004,C104_C_1206_3216Metric_60753A85_ln_005,C104_C_1206_3216Metric_60753A85_ln_006,+28 more]
  LinkMode = 0
FEATURE [App::LinkGroup] Step_Models_266e
  ElementList = -> [Top_266e,Bot_266e]
  LinkMode = 0
FEATURE [App::LinkGroup] Board_266e  label="Controle"
  ElementList = -> [Board_Geoms_266e,Step_Models_266e,Step_Virtual_Models_266e]
  LinkMode = 0
FEATURE [PartDesign::CoordinateSystem] LCS_0
  AttacherType = Attacher::AttachEngine3D
  MapMode = 2
  Support = -> [X_Axis]
FEATURE [PartDesign::Line] HoleAxis_1
  AttacherType = Attacher::AttachEngineLine
  Length = 4.50902
  MapMode = 19
  Placement = pos=(62.35,34.15,0) rot=(0,0,1;0rad)
  ResizeMode = 1
  Support = -> [Pcb_266e]
FEATURE [PartDesign::Line] HoleAxis_2
  AttacherType = Attacher::AttachEngineLine
  Length = 4.50902
  MapMode = 19
  Placement = pos=(2.7604,34.1266,0) rot=(0,0,1;0rad)
  ResizeMode = 1
  Support = -> [Pcb_266e]
FEATURE [PartDesign::Line] HoleAxis_3
  AttacherType = Attacher::AttachEngineLine
  Length = 4.50902
  MapMode = 19
  Placement = pos=(2.77348,3.47598,0) rot=(0,0,1;0rad)
  ResizeMode = 1
  Support = -> [Pcb_266e]
FEATURE [PartDesign::Line] HoleAxis_4
  AttacherType = Attacher::AttachEngineLine
  Length = 4.50902
  MapMode = 19
  Placement = pos=(62.3621,3.5,0) rot=(0,0,1;0rad)
  ResizeMode = 1
  Support = -> [Pcb_266e]
FEATURE [App::Part] Part
  Group = -> [LCS_0,R103_R_0603_1608Metric_607532D5_ln_001,TopV_266e,Shape,Shape002,C104_C_1206_3216Metric_60753A85_ln_001,C104_C_1206_3216Metric_60753A85_ln_,C104_C_1206_3216Metric_60753A85_ln_003,C104_C_1206_3216Metric_60753A85_ln_004,C104_C_1206_3216Metric_60753A85_ln_005,C104_C_1206_3216Metric_60753A85_ln_006,C104_C_1206_3216Metric_60753A85_ln_007,Shape004,C104_C_1206_3216Metric_60753A85_ln_002,Shape003,+43 more]
  Origin = -> Origin
---- part heatsink.FCStd = doc fcstd_6f6a2555591a ----
FCSTD DOCUMENT  (FreeCAD 0.19R24276 (Git))
Label: heatsink
License: Creative Commons Attribution-NonCommercial-ShareAlike
LicenseURL: http://creativecommons.org/licenses/by-nc-sa/4.0/
objects: PartDesign::Body×1, Image::ImagePlane×1, Sketcher::SketchObject×1, PartDesign::Pad×1, PartDesign::CoordinateSystem×1, App::Part×1
note: 5 computed .brp shape members not serialized (recipe doc carries the construction recipe); baked Part::Feature solids carry a one-line shape summary decoded from their .brp

FEATURE [PartDesign::Body] Body
  Origin = -> Origin
FEATURE [Image::ImagePlane] ImagePlane
  Placement = pos=(0,0,-0.0001) rot=(0,0,1;0rad)
  XSize = 189.664
  YSize = 135.264
FEATURE [Sketcher::SketchObject] Sketch002  label="heatsink"
  FullyConstrained = true
  sketch-geometry (66):
    g0: LineSegment StartX=64.9692 StartY=-39.4035 StartZ=0 EndX=64.9692 EndY=-33.0535 EndZ=0
    g1: LineSegment StartX=64.9692 StartY=-33.0535 StartZ=0 EndX=61.9692 EndY=-33.0535 EndZ=0
    g2: LineSegment StartX=61.9692 StartY=-33.0535 StartZ=0 EndX=61.9692 EndY=-34.5535 EndZ=0
    g3: LineSegment StartX=61.9692 StartY=-34.5535 StartZ=0 EndX=56.9692 EndY=-34.5535 EndZ=0
    g4: LineSegment StartX=56.9692 StartY=-26.2535 StartZ=0 EndX=61.9692 EndY=-26.2535 EndZ=0
    g5: LineSegment StartX=61.9692 StartY=-26.2535 StartZ=0 EndX=61.9692 EndY=-27.7535 EndZ=0
    g6: LineSegment StartX=61.9692 StartY=-27.7535 StartZ=0 EndX=64.9692 EndY=-27.7535 EndZ=0
    g7: LineSegment StartX=64.9692 StartY=-27.7535 StartZ=0 EndX=64.9692 EndY=26.5965 EndZ=0
    g8: LineSegment StartX=66.9692 StartY=28.5965 StartZ=0 EndX=77.4692 EndY=28.5965 EndZ=0
    g9: LineSegment StartX=77.4692 StartY=28.5965 StartZ=0 EndX=77.4692 EndY=30.5965 EndZ=0
    g10: LineSegment StartX=77.4692 StartY=30.5965 StartZ=0 EndX=64.9692 EndY=30.5965 EndZ=0
    g11: LineSegment StartX=62.9692 StartY=28.5965 StartZ=0 EndX=62.9692 EndY=-15.4035 EndZ=0
    g12: LineSegment StartX=54.9692 StartY=-15.4035 StartZ=0 EndX=53.1692 EndY=29.3465 EndZ=0
    g13: LineSegment StartX=51.0549 StartY=29.3465 StartZ=0 EndX=50.2549 EndY=-24.4035 EndZ=0
    g14: LineSegment StartX=38.2549 StartY=-24.4035 StartZ=0 EndX=37.4549 EndY=29.3465 EndZ=0
    g15: LineSegment StartX=35.3406 StartY=29.3465 StartZ=0 EndX=34.5406 EndY=-24.4035 EndZ=0
    g16: LineSegment StartX=22.5406 StartY=-24.4035 StartZ=0 EndX=21.7406 EndY=29.3465 EndZ=0
    g17: LineSegment StartX=19.6263 StartY=29.3465 StartZ=0 EndX=18.8263 EndY=-24.4035 EndZ=0
    g18: LineSegment StartX=6.8263 StartY=-24.4035 StartZ=0 EndX=6.0263 EndY=29.3465 EndZ=0
    g19: ArcOfCircle CenterX=28.5406 CenterY=-24.4035 CenterZ=0 NormalX=0 NormalY=0 NormalZ=1 AngleXU=0 Radius=6 StartAngle=3.14159 EndAngle=6.28319
    g20: ArcOfCircle CenterX=12.8263 CenterY=-24.4035 CenterZ=0 NormalX=0 NormalY=0 NormalZ=1 AngleXU=0 Radius=6 StartAngle=3.14159 EndAngle=6.28319
    g21: ArcOfCircle CenterX=44.2549 CenterY=-24.4035 CenterZ=0 NormalX=0 NormalY=0 NormalZ=1 AngleXU=0 Radius=6 StartAngle=3.14159 EndAngle=6.28319
    g22: ArcOfCircle CenterX=58.9692 CenterY=-15.4035 CenterZ=0 NormalX=0 NormalY=0 NormalZ=1 AngleXU=0 Radius=4 StartAngle=3.14159 EndAngle=6.28319
    g23: ArcOfCircle CenterX=52.112 CenterY=29.3465 CenterZ=0 NormalX=0 NormalY=0 NormalZ=1 AngleXU=0 Radius=1.05714 StartAngle=0 EndAngle=3.14159
    g24: ArcOfCircle CenterX=20.6834 CenterY=29.3465 CenterZ=0 NormalX=0 NormalY=0 NormalZ=1 AngleXU=0 Radius=1.05714 StartAngle=0 EndAngle=3.14159
    g25: LineSegment StartX=56.9692 StartY=-26.2535 StartZ=0 EndX=56.9692 EndY=-30.4035 EndZ=0
    g26: LineSegment StartX=56.9692 StartY=-30.4035 StartZ=0 EndX=56.9692 EndY=-34.5535 EndZ=0
    g27: LineSegment StartX=-55.0308 StartY=-39.4035 StartZ=0 EndX=-55.0308 EndY=-33.0535 EndZ=0
    g28: LineSegment StartX=-55.0308 StartY=-33.0535 StartZ=0 EndX=-52.0308 EndY=-33.0535 EndZ=0
    g29: LineSegment StartX=-52.0308 StartY=-33.0535 StartZ=0 EndX=-52.0308 EndY=-34.5535 EndZ=0
    g30: LineSegment StartX=-52.0308 StartY=-34.5535 StartZ=0 EndX=-47.0308 EndY=-34.5535 EndZ=0
    g31: LineSegment StartX=-47.0308 StartY=-26.2535 StartZ=0 EndX=-52.0308 EndY=-26.2535 EndZ=0
    g32: LineSegment StartX=-52.0308 StartY=-26.2535 StartZ=0 EndX=-52.0308 EndY=-27.7535 EndZ=0
    g33: LineSegment StartX=-52.0308 StartY=-27.7535 StartZ=0 EndX=-55.0308 EndY=-27.7535 EndZ=0
    g34: LineSegment StartX=-55.0308 StartY=-27.7535 StartZ=0 EndX=-55.0308 EndY=26.5965 EndZ=0
    g35: LineSegment StartX=-57.0308 StartY=28.5965 StartZ=0 EndX=-67.5308 EndY=28.5965 EndZ=0
    g36: LineSegment StartX=-67.5308 StartY=28.5965 StartZ=0 EndX=-67.5308 EndY=30.5965 EndZ=0
    g37: LineSegment StartX=-67.5308 StartY=30.5965 StartZ=0 EndX=-55.0308 EndY=30.5965 EndZ=0
    g38: LineSegment StartX=-53.0308 StartY=28.5965 StartZ=0 EndX=-53.0308 EndY=-15.4035 EndZ=0
    g39: LineSegment StartX=-45.0308 StartY=-15.4035 StartZ=0 EndX=-43.2308 EndY=29.3465 EndZ=0
    g40: LineSegment StartX=-41.1166 StartY=29.3465 StartZ=0 EndX=-40.3166 EndY=-24.4035 EndZ=0
    g41: LineSegment StartX=-28.3166 StartY=-24.4035 StartZ=0 EndX=-27.5166 EndY=29.3465 EndZ=0
    g42: LineSegment StartX=-25.4023 StartY=29.3465 StartZ=0 EndX=-24.6023 EndY=-24.4035 EndZ=0
    g43: LineSegment StartX=-12.6023 StartY=-24.4035 StartZ=0 EndX=-11.8023 EndY=29.3465 EndZ=0
    g44: LineSegment StartX=-9.68798 StartY=29.3465 StartZ=0 EndX=-8.88798 EndY=-24.4035 EndZ=0
    g45: LineSegment StartX=3.11202 StartY=-24.4035 StartZ=0 EndX=3.91202 EndY=29.3465 EndZ=0
    g46: ArcOfCircle CenterX=-18.6023 CenterY=-24.4035 CenterZ=0 NormalX=0 NormalY=0 NormalZ=1 AngleXU=0 Radius=6 StartAngle=3.14159 EndAngle=6.28319
    g47: ArcOfCircle CenterX=-2.88798 CenterY=-24.4035 CenterZ=0 NormalX=0 NormalY=0 NormalZ=1 AngleXU=0 Radius=6 StartAngle=3.14159 EndAngle=6.28319
    g48: ArcOfCircle CenterX=-34.3166 CenterY=-24.4035 CenterZ=0 NormalX=0 NormalY=0 NormalZ=1 AngleXU=0 Radius=6 StartAngle=3.14159 EndAngle=6.28319
    g49: ArcOfCircle CenterX=-49.0308 CenterY=-15.4035 CenterZ=0 NormalX=0 NormalY=0 NormalZ=1 AngleXU=0 Radius=4 StartAngle=3.14159 EndAngle=6.28319
    g50: ArcOfCircle CenterX=-42.1737 CenterY=29.3465 CenterZ=0 NormalX=0 NormalY=0 NormalZ=1 AngleXU=0 Radius=1.05714 StartAngle=0 EndAngle=3.14159
    g51: ArcOfCircle CenterX=-26.4594 CenterY=29.3465 CenterZ=0 NormalX=0 NormalY=0 NormalZ=1 AngleXU=0 Radius=1.05714 StartAngle=3e-16 EndAngle=3.14159
    g52: ArcOfCircle CenterX=-10.7451 CenterY=29.3465 CenterZ=0 NormalX=0 NormalY=0 NormalZ=1 AngleXU=0 Radius=1.05714 StartAngle=6e-16 EndAngle=3.14159
    g53: ArcOfCircle CenterX=4.96916 CenterY=29.3465 CenterZ=0 NormalX=0 NormalY=0 NormalZ=1 AngleXU=0 Radius=1.05714 StartAngle=-9e-16 EndAngle=3.14159
    g54: LineSegment StartX=-47.0308 StartY=-26.2535 StartZ=0 EndX=-47.0308 EndY=-30.4035 EndZ=0
    g55: LineSegment StartX=-47.0308 StartY=-30.4035 StartZ=0 EndX=-47.0308 EndY=-34.5535 EndZ=0
    g56: ArcOfCircle CenterX=36.3977 CenterY=29.3465 CenterZ=0 NormalX=0 NormalY=0 NormalZ=1 AngleXU=0 Radius=1.05714 StartAngle=-9e-16 EndAngle=3.14159
    g57: ArcOfCircle CenterX=-57.0308 CenterY=26.5965 CenterZ=0 NormalX=0 NormalY=0 NormalZ=1 AngleXU=0 Radius=2 StartAngle=0 EndAngle=1.5708
    g58: GeomPoint X=-55.0308 Y=28.5965 Z=0
    g59: ArcOfCircle CenterX=-55.0308 CenterY=28.5965 CenterZ=0 NormalX=0 NormalY=0 NormalZ=1 AngleXU=0 Radius=2 StartAngle=0 EndAngle=1.5708
    g60: GeomPoint X=-53.0308 Y=30.5965 Z=0
    g61: ArcOfCircle CenterX=66.9692 CenterY=26.5965 CenterZ=0 NormalX=0 NormalY=0 NormalZ=1 AngleXU=0 Radius=2 StartAngle=1.5708 EndAngle=3.14159
    g62: GeomPoint X=64.9692 Y=28.5965 Z=0
    g63: ArcOfCircle CenterX=64.9692 CenterY=28.5965 CenterZ=0 NormalX=0 NormalY=0 NormalZ=1 AngleXU=0 Radius=2 StartAngle=1.5708 EndAngle=3.14159
    g64: GeomPoint X=62.9692 Y=30.5965 Z=0
    g65: LineSegment StartX=64.9692 StartY=-39.4035 StartZ=0 EndX=-55.0308 EndY=-39.4035 EndZ=0
  constraints (209):
    c: Horizontal(g8)
    c: Horizontal(g10)
    c: Radius(g22) = 4
    c: Radius(g21) = 6
    c: Equal(g21,g19)
    c: Equal(g21,g20)
    c: Vertical(g9)
    c: Vertical(g7)
    c: Vertical(g0)
    c: Vertical(g5)
    c: Vertical(g2)
    c: Horizontal(g6)
    c: Horizontal(g1)
    c: Horizontal(g3)
    c: Horizontal(g4)
    c: Coincident(g13,g23)
    c: Coincident(g12,g23)
    c: Coincident(g24,g16)
    c: Coincident(g24,g17)
    c: Equal(g23,g24)
    c: Equal(g6,g1)
    c: Equal(g5,g2)
    c: Equal(g4,g3)
    c: Distance(g6,g0) = 5.3
    c: Coincident(g4,g5)
    c: Coincident(g2,g3)
    c: Coincident(g1,g2)
    c: Coincident(g0,g1)
    c: Coincident(g6,g7)
    c: Coincident(g9,g10)
    c: Coincident(g8,g9)
    c: Vertical(g11)
    c: Coincident(g5,g6)
    c: Coincident(g13,g21)
    c: Coincident(g14,g21)
    c: Coincident(g15,g19)
    c: Coincident(g16,g19)
    c: Coincident(g17,g20)
    c: Coincident(g18,g20)
    c: Coincident(g12,g22)
    c: Coincident(g11,g22)
    c: Coincident(g25,g4)
    c: Vertical(g25)
    c: Coincident(g26,g25)
    c: Coincident(g26,g3)
    c: Vertical(g26)
    c: Equal(g26,g25)
    c: Horizontal(g35)
    c: Horizontal(g37)
    c: Radius(g49) = 4
    c: Radius(g48) = 6
    c: Equal(g48,g46)
    c: Equal(g48,g47)
    c: Vertical(g36)
    c: Vertical(g34)
    c: Vertical(g27)
    c: Vertical(g32)
    c: Vertical(g29)
    c: Horizontal(g33)
    c: Horizontal(g28)
    c: Horizontal(g30)
    c: Horizontal(g31)
    c: Coincident(g40,g50)
    c: Coincident(g39,g50)
    c: Coincident(g51,g42)
    c: Coincident(g52,g43)
    c: Coincident(g52,g44)
    c: Coincident(g53,g45)
    c: Equal(g50,g52)
    c: Equal(g33,g28)
    c: Equal(g32,g29)
    c: Equal(g31,g30)
    c: Distance(g33,g27) = 5.3
    c: DistanceY(g30,g31) = 8.3
    c: Coincident(g31,g32)
    c: Coincident(g29,g30)
    c: Coincident(g28,g29)
    c: Coincident(g27,g28)
    c: Coincident(g33,g34)
    c: Coincident(g36,g37)
    c: Coincident(g35,g36)
    c: Vertical(g38)
    c: DistanceX(g60,g39) = 9.8
    c: DistanceX(g36,g60) = 14.5
    c: DistanceY(g27,g36) = 70
    c: Coincident(g32,g33)
    c: Coincident(g40,g48)
    c: Coincident(g41,g48)
    c: Coincident(g42,g46)
    c: Coincident(g43,g46)
    c: Coincident(g44,g47)
    c: Coincident(g45,g47)
    c: Coincident(g39,g49)
    c: Coincident(g38,g49)
    c: DistanceY(g38,g39) = 0
    c: DistanceY(g41,g40) = 0
    c: DistanceY(g42,g43) = 0
    c: DistanceY(g44,g45) = 0
    c: DistanceY(g41,g42) = 0
    c: DistanceY(g43,g44) = 0
    c: Coincident(g54,g31)
    c: Vertical(g54)
    c: Coincident(g55,g54)
    c: Coincident(g55,g30)
    c: Vertical(g55)
    c: Equal(g55,g54)
    c: DistanceX(g28,g28) = 3
    c: DistanceX(g30,g30) = 5
    c: DistanceX(g27) = -55.0308
    c: DistanceY(g27) = -39.4035
    c: DistanceY(g40,g39) = 0
    c: DistanceY(g41,g42) = 0
    c: DistanceY(g43,g44) = 0
    c: DistanceY(g53,g45) = 0
    c: DistanceY(g40,g50) = 0
    c: DistanceY(g41,g51) = 0
    c: DistanceY(g52,g43) = 0
    c: DistanceY(g45,g53) = 0
    c: DistanceY(g39,g60) = 1.25
    c: DistanceY(g50,g51) = 0
    c: DistanceY(g52,g53) = 0
    c: DistanceY(g36,g36) = 2
    c: DistanceY(g51,g52) = 0
    c: Equal(g4,g31)
    c: Equal(g25,g54)
    c: Equal(g33,g6)
    c: Equal(g27,g0)
    c: Coincident(g53,g18)
    c: Equal(g9,g36)
    c: DistanceY(g17,g24) = 0
    c: DistanceY(g16,g24) = 0
    c: DistanceY(g53,g24) = 0
    c: DistanceY(g13,g23) = 0
    c: DistanceY(g23,g12) = 0
    c: Coincident(g56,g15)
    c: Coincident(g56,g14)
    c: DistanceY(g56,g15) = 0
    c: DistanceY(g56,g14) = 0
    c: DistanceY(g24,g56) = 0
    c: DistanceY(g56,g23) = 0
    c: DistanceY(g14,g21) = 0
    c: DistanceY(g15,g19) = 0
    c: DistanceY(g16,g19) = 0
    c: DistanceY(g17,g20) = 0
    c: DistanceY(g20,g18) = 0
    c: Parallel(g40,g42)
    c: Parallel(g42,g44)
    c: Parallel(g44,g18)
    c: Parallel(g18,g16)
    c: Parallel(g16,g14)
    c: Parallel(g13,g15)
    c: Parallel(g15,g17)
    c: Parallel(g17,g45)
    c: Parallel(g45,g43)
    c: Parallel(g43,g41)
    c: DistanceX(g12,g64) = 9.8
    c: DistanceY(g12,g22) = 0
    c: DistanceY(g22,g11) = 0
    c: DistanceY(g49,g22) = 0
    c: DistanceX(g44,g45) = 13.6
    c: Equal(g50,g23)
    c: DistanceX(g58,g60) = 2
    c: DistanceX(g64,g62) = 2
    c: Equal(g53,g24)
    c: Equal(g24,g56)
    c: Equal(g18,g45)
    c: DistanceX(g18,g17) = 13.6
    c: Radius(g52) = 1.05714
    c: DistanceX(g27,g0) = 120
    c: Coincident(g41,g51)
    c: PointOnObject(g58,g34)
    c: PointOnObject(g58,g35)
    c: Tangent(g34,g57) = -1.5708
    c: Tangent(g35,g57) = -1.5708
    c: PointOnObject(g60,g37)
    c: PointOnObject(g60,g38)
    c: Tangent(g37,g59) = 1.5708
    c: Tangent(g38,g59) = 1.5708
    c: Radius(g57) = 2
    c: Radius(g59) = 2
    c: PointOnObject(g62,g7)
    c: PointOnObject(g62,g8)
    c: Tangent(g7,g61) = 1.5708
    c: Tangent(g8,g61) = 1.5708
    c: PointOnObject(g64,g10)
    c: PointOnObject(g64,g11)
    c: Tangent(g10,g63) = -1.5708
    c: Tangent(g11,g63) = -1.5708
    c: Radius(g61) = 2
    c: Radius(g63) = 2
    c: Equal(g7,g34)
    c: Equal(g11,g38)
    c: DistanceY(g23,g64) = 1.25
    c: Equal(g10,g37)
    c: Equal(g8,g35)
    c: Coincident(g65,g0)
    c: Coincident(g65,g27)
    c: Horizontal(g65)
    c: Distance(g54,g65) = 9
    c: Distance(g48,g65) = 15
    c: Distance(g46,g65) = 15
    c: Distance(g47,g65) = 15
    c: Distance(g20,g65) = 15
    c: Distance(g19,g65) = 15
    c: Distance(g21,g65) = 15
    c: DistanceY(g18,g45) = 0
    c: DistanceY(g13,g21) = 0
    c: Distance(g49,g65) = 24
    c: Equal(g51,g50)
FEATURE [PartDesign::Pad] Pad
  Direction = (1,1,1)
  Length = 100
  Length2 = 100
  Profile = -> Sketch002
  Type = 0
FEATURE [PartDesign::CoordinateSystem] LCS_1  label="LCS_0"
  AttacherType = Attacher::AttachEngine3D
  AttachmentOffset = pos=(0,0,0) rot=(0.57735,0.57735,0.57735;2.0944rad)
  MapMode = 6
  Placement = pos=(-55.0308,-39.4035,0) rot=(0.707107,0,0.707107;3.14159rad)
  Support = -> [Pad]
FEATURE [App::Part] Part
  Group = -> [Body,Sketch002,Pad,LCS_1]
  Origin = -> Origin001
---- part support1.FCStd = doc fcstd_3c80b2752f52 ----
FCSTD DOCUMENT  (FreeCAD 0.19R24291 (Git))
Label: support1
License: Creative Commons Attribution-NonCommercial-ShareAlike
LicenseURL: http://creativecommons.org/licenses/by-nc-sa/4.0/
objects: PartDesign::Line×11, Sketcher::SketchObject×6, PartDesign::Pad×6, PartDesign::Body×6, PartDesign::CoordinateSystem×3, PartDesign::SubtractiveBox×2, PartDesign::FeatureBase×2, Part::Box×1, Part::FeaturePython×1, Part::MultiFuse×1, App::Part×1
note: 47 computed .brp shape members not serialized (recipe doc carries the construction recipe); baked Part::Feature solids carry a one-line shape summary decoded from their .brp

FEATURE [PartDesign::CoordinateSystem] LCS_0
  AttacherType = Attacher::AttachEngine3D
  MapMode = 2
  Support = -> [X_Axis]
FEATURE [PartDesign::CoordinateSystem] LCS_0001
  AttacherType = Attacher::AttachEngine3D
  MapMode = 2
  Support = -> [X_Axis001]
FEATURE [Sketcher::SketchObject] Sketch001
  FullyConstrained = true
  sketch-geometry (8):
    g0: LineSegment StartX=0 StartY=0 StartZ=0 EndX=44 EndY=0 EndZ=0
    g1: LineSegment StartX=44 StartY=0 StartZ=0 EndX=44 EndY=15.2 EndZ=0
    g2: LineSegment StartX=44 StartY=15.2 StartZ=0 EndX=0 EndY=15.2 EndZ=0
    g3: LineSegment StartX=0 StartY=15.2 StartZ=0 EndX=0 EndY=0 EndZ=0
    g4: Circle CenterX=5.3 CenterY=10 CenterZ=0 NormalX=0 NormalY=0 NormalZ=1 AngleXU=0 Radius=1.6
    g5: Circle CenterX=16.97 CenterY=10 CenterZ=0 NormalX=0 NormalY=0 NormalZ=1 AngleXU=0 Radius=1.6
    g6: Circle CenterX=28.64 CenterY=10 CenterZ=0 NormalX=0 NormalY=0 NormalZ=1 AngleXU=0 Radius=1.6
    g7: Circle CenterX=40.31 CenterY=10 CenterZ=0 NormalX=0 NormalY=0 NormalZ=1 AngleXU=0 Radius=1.6
  constraints (23):
    c: Coincident(g0,g1)
    c: Coincident(g1,g2)
    c: Coincident(g2,g3)
    c: Coincident(g3,g0)
    c: Horizontal(g0)
    c: Horizontal(g2)
    c: Vertical(g1)
    c: Vertical(g3)
    c: Coincident(g0,g-1)
    c: Equal(g5,g4)
    c: Equal(g4,g6)
    c: Equal(g6,g7)
    c: DistanceY(g5,g4) = 0
    c: DistanceY(g6,g5) = 0
    c: DistanceY(g7,g6) = 0
    c: Distance(g4,g3) = 5.3
    c: Distance(g4,g2) = 5.2
    c: DistanceX(g4,g5) = 11.67
    c: DistanceX(g5,g6) = 11.67
    c: DistanceX(g6,g7) = 11.67
    c: DistanceY(g3,g3) = 15.2
    c: DistanceX(g0,g0) = 44
    c: Diameter(g4) = 3.2
FEATURE [Sketcher::SketchObject] Sketch002
  FullyConstrained = true
  sketch-geometry (8):
    g0: LineSegment StartX=0 StartY=0 StartZ=0 EndX=44 EndY=0 EndZ=0
    g1: LineSegment StartX=44 StartY=0 StartZ=0 EndX=44 EndY=15.2 EndZ=0
    g2: LineSegment StartX=44 StartY=15.2 StartZ=0 EndX=0 EndY=15.2 EndZ=0
    g3: LineSegment StartX=0 StartY=15.2 StartZ=0 EndX=0 EndY=0 EndZ=0
    g4: Circle CenterX=3.69 CenterY=10 CenterZ=0 NormalX=0 NormalY=0 NormalZ=1 AngleXU=0 Radius=1.5
    g5: Circle CenterX=15.36 CenterY=10 CenterZ=0 NormalX=0 NormalY=0 NormalZ=1 AngleXU=0 Radius=1.5
    g6: Circle CenterX=27.03 CenterY=10 CenterZ=0 NormalX=0 NormalY=0 NormalZ=1 AngleXU=0 Radius=1.5
    g7: Circle CenterX=38.7 CenterY=10 CenterZ=0 NormalX=0 NormalY=0 NormalZ=1 AngleXU=0 Radius=1.5
  constraints (24):
    c: Coincident(g0,g1)
    c: Coincident(g1,g2)
    c: Coincident(g2,g3)
    c: Coincident(g3,g0)
    c: Horizontal(g0)
    c: Horizontal(g2)
    c: Vertical(g1)
    c: Vertical(g3)
    c: Coincident(g0,g-1)
    c: Equal(g5,g4)
    c: Equal(g4,g6)
    c: Equal(g6,g7)
    c: DistanceY(g5,g4) = 0
    c: DistanceY(g6,g5) = 0
    c: DistanceY(g7,g6) = 0
    c: Distance(g4,g3) = 3.69
    c: Distance(g4,g2) = 5.2
    c: DistanceX(g4,g5) = 11.67
    c: DistanceX(g5,g6) = 11.67
    c: DistanceX(g6,g7) = 11.67
    c: DistanceY(g3,g3) = 15.2
    c: DistanceX(g0,g0) = 44
    c: Distance(g7,g1) = 5.3
    c: Diameter(g4) = 3
FEATURE [PartDesign::CoordinateSystem] LCS_0002
  AttacherType = Attacher::AttachEngine3D
  MapMode = 2
  Support = -> [X_Axis002]
FEATURE [Sketcher::SketchObject] Sketch003
  FullyConstrained = true
  MapMode = 2
  Support = -> [Sketch002]
  sketch-geometry (8):
    g0: LineSegment StartX=0 StartY=0 StartZ=0 EndX=44 EndY=0 EndZ=0
    g1: LineSegment StartX=44 StartY=0 StartZ=0 EndX=44 EndY=15.2 EndZ=0
    g2: LineSegment StartX=44 StartY=15.2 StartZ=0 EndX=0 EndY=15.2 EndZ=0
    g3: LineSegment StartX=0 StartY=15.2 StartZ=0 EndX=0 EndY=0 EndZ=0
    g4: Circle CenterX=3.69 CenterY=10 CenterZ=0 NormalX=0 NormalY=0 NormalZ=1 AngleXU=0 Radius=3.5
    g5: Circle CenterX=15.36 CenterY=10 CenterZ=0 NormalX=0 NormalY=0 NormalZ=1 AngleXU=0 Radius=3.5
    g6: Circle CenterX=27.03 CenterY=10 CenterZ=0 NormalX=0 NormalY=0 NormalZ=1 AngleXU=0 Radius=3.5
    g7: Circle CenterX=38.7 CenterY=10 CenterZ=0 NormalX=0 NormalY=0 NormalZ=1 AngleXU=0 Radius=3.5
  constraints (24):
    c: Coincident(g0,g1)
    c: Coincident(g1,g2)
    c: Coincident(g2,g3)
    c: Coincident(g3,g0)
    c: Horizontal(g0)
    c: Horizontal(g2)
    c: Vertical(g1)
    c: Vertical(g3)
    c: Coincident(g0,g-1)
    c: Equal(g5,g4)
    c: Equal(g4,g6)
    c: Equal(g6,g7)
    c: Radius(g4) = 3.5
    c: DistanceY(g5,g4) = 0
    c: DistanceY(g6,g5) = 0
    c: DistanceY(g7,g6) = 0
    c: Distance(g4,g3) = 3.69
    c: Distance(g4,g2) = 5.2
    c: DistanceX(g4,g5) = 11.67
    c: DistanceX(g5,g6) = 11.67
    c: DistanceX(g6,g7) = 11.67
    c: DistanceY(g3,g3) = 15.2
    c: DistanceX(g0,g0) = 44
    c: Distance(g7,g1) = 5.3
FEATURE [PartDesign::Pad] Pad003
  Direction = (1,1,1)
  Length = 3
  Length2 = 100
  Profile = -> Sketch003
  Type = 0
FEATURE [PartDesign::Pad] Pad002
  BaseFeature = -> Pad003
  Direction = (1,1,1)
  Length = 2
  Length2 = 100
  Profile = -> Sketch002
  Reversed = true
  Type = 0
FEATURE [PartDesign::SubtractiveBox] Box005
  AttacherType = Attacher::AttachEngine3D
  BaseFeature = -> Pad002
  Height = 1.7
  Length = 44
  MapMode = 49
  Placement = pos=(44,15.2,0) rot=(0,0.707107,-0.707107;3.14159rad)
  Support = -> [Pad002]
  Width = 4
FEATURE [Part::Box] Box006  label="Cube"
  AttacherType = Attacher::AttachEngine3D
  Height = 6
  Length = 124
  Width = 2
FEATURE [PartDesign::FeatureBase] BaseFeature
  BaseFeature = -> Box006
FEATURE [PartDesign::Body] Body002
  BaseFeature = -> Box006
  Group = -> [BaseFeature]
  Origin = -> Origin003
  Placement = pos=(-80,0,-6) rot=(0,0,1;0rad)
  Tip = -> BaseFeature
FEATURE [Sketcher::SketchObject] Sketch004
  FullyConstrained = true
  MapMode = 5
  Support = -> [XY_Plane005]
  sketch-geometry (10):
    g0: LineSegment StartX=0 StartY=13.5 StartZ=0 EndX=0 EndY=2 EndZ=0
    g1: LineSegment StartX=0 StartY=2 StartZ=0 EndX=-36 EndY=2 EndZ=0
    g2: LineSegment StartX=-36 StartY=2 StartZ=0 EndX=-36 EndY=13.5 EndZ=0
    g3: Circle CenterX=-33.3 CenterY=9.7 CenterZ=0 NormalX=0 NormalY=0 NormalZ=1 AngleXU=0 Radius=1.6
    g4: Circle CenterX=-2.7 CenterY=9.7 CenterZ=0 NormalX=0 NormalY=0 NormalZ=1 AngleXU=0 Radius=1.6
    g5: LineSegment StartX=-36 StartY=13.5 StartZ=0 EndX=-28.5 EndY=13.5 EndZ=0
    g6: LineSegment StartX=-7.5 StartY=13.5 StartZ=0 EndX=-7.5 EndY=7 EndZ=0
    g7: LineSegment StartX=-7.5 StartY=7 StartZ=0 EndX=-28.5 EndY=7 EndZ=0
    g8: LineSegment StartX=-28.5 StartY=7 StartZ=0 EndX=-28.5 EndY=13.5 EndZ=0
    g9: LineSegment StartX=-7.5 StartY=13.5 StartZ=0 EndX=0 EndY=13.5 EndZ=0
  constraints (30):
    c: Coincident(g0,g1)
    c: Coincident(g1,g2)
    c: Horizontal(g1)
    c: Vertical(g0)
    c: Vertical(g2)
    c: PointOnObject(g0,g-2)
    c: Coincident(g5,g2)
    c: Horizontal(g5)
    c: Coincident(g6,g7)
    c: Coincident(g7,g8)
    c: Horizontal(g7)
    c: Vertical(g6)
    c: Vertical(g8)
    c: Coincident(g9,g0)
    c: Horizontal(g9)
    c: DistanceY(g2,g2) = 11.5
    c: Coincident(g5,g8)
    c: Coincident(g6,g9)
    c: Equal(g8,g6)
    c: Equal(g5,g9)
    c: DistanceX(g1,g1) = 36
    c: DistanceY(g1) = 2
    c: DistanceY(g8,g8) = 6.5
    c: DistanceX(g7,g7) = 21
    c: Distance(g3,g2) = 2.7
    c: Distance(g3,g1) = 7.7
    c: Equal(g4,g3)
    c: Distance(g4,g0) = 2.7
    c: Distance(g4,g1) = 7.7
    c: Diameter(g3) = 3.2
FEATURE [PartDesign::Pad] Pad004
  Direction = (1,1,1)
  Length = 1
  Length2 = 100
  Profile = -> Sketch004
  Type = 0
FEATURE [PartDesign::Body] Body004
  Group = -> [Sketch004,Pad004]
  Origin = -> Origin005
  Placement = pos=(0,0,-2) rot=(0,0,1;0rad)
  Tip = -> Pad004
FEATURE [Sketcher::SketchObject] Sketch005
  FullyConstrained = true
  MapMode = 5
  Support = -> [XY_Plane006]
  sketch-geometry (6):
    g0: LineSegment StartX=0 StartY=13.5 StartZ=0 EndX=0 EndY=2 EndZ=0
    g1: LineSegment StartX=0 StartY=2 StartZ=0 EndX=-36 EndY=2 EndZ=0
    g2: LineSegment StartX=-36 StartY=2 StartZ=0 EndX=-36 EndY=13.5 EndZ=0
    g3: Circle CenterX=-33.3 CenterY=9.7 CenterZ=0 NormalX=0 NormalY=0 NormalZ=1 AngleXU=0 Radius=1.6
    g4: Circle CenterX=-2.7 CenterY=9.7 CenterZ=0 NormalX=0 NormalY=0 NormalZ=1 AngleXU=0 Radius=1.6
    g5: LineSegment StartX=-36 StartY=13.5 StartZ=0 EndX=0 EndY=13.5 EndZ=0
  constraints (18):
    c: Coincident(g0,g1)
    c: Coincident(g1,g2)
    c: Horizontal(g1)
    c: Vertical(g0)
    c: Vertical(g2)
    c: PointOnObject(g0,g-2)
    c: Coincident(g5,g2)
    c: Horizontal(g5)
    c: DistanceY(g2,g2) = 11.5
    c: DistanceX(g1,g1) = 36
    c: DistanceY(g1) = 2
    c: Distance(g3,g2) = 2.7
    c: Distance(g3,g1) = 7.7
    c: Equal(g4,g3)
    c: Distance(g4,g1) = 7.7
    c: Diameter(g3) = 3.2
    c: Coincident(g0,g5)
    c: Distance(g4,g0) = 2.7
FEATURE [Sketcher::SketchObject] Sketch
  FullyConstrained = true
  MapMode = 2
  Support = -> [Sketch005]
  sketch-geometry (8):
    g0: LineSegment StartX=0 StartY=0 StartZ=0 EndX=44 EndY=0 EndZ=0
    g1: LineSegment StartX=44 StartY=0 StartZ=0 EndX=44 EndY=15.2 EndZ=0
    g2: LineSegment StartX=44 StartY=15.2 StartZ=0 EndX=0 EndY=15.2 EndZ=0
    g3: LineSegment StartX=0 StartY=15.2 StartZ=0 EndX=0 EndY=0 EndZ=0
    g4: Circle CenterX=5.3 CenterY=10 CenterZ=0 NormalX=0 NormalY=0 NormalZ=1 AngleXU=0 Radius=3.5
    g5: Circle CenterX=16.97 CenterY=10 CenterZ=0 NormalX=0 NormalY=0 NormalZ=1 AngleXU=0 Radius=3.5
    g6: Circle CenterX=28.64 CenterY=10 CenterZ=0 NormalX=0 NormalY=0 NormalZ=1 AngleXU=0 Radius=3.5
    g7: Circle CenterX=40.31 CenterY=10 CenterZ=0 NormalX=0 NormalY=0 NormalZ=1 AngleXU=0 Radius=3.5
  constraints (23):
    c: Coincident(g0,g1)
    c: Coincident(g1,g2)
    c: Coincident(g2,g3)
    c: Coincident(g3,g0)
    c: Horizontal(g0)
    c: Horizontal(g2)
    c: Vertical(g1)
    c: Vertical(g3)
    c: Coincident(g0,g-1)
    c: Equal(g5,g4)
    c: Equal(g4,g6)
    c: Equal(g6,g7)
    c: Radius(g4) = 3.5
    c: DistanceY(g5,g4) = 0
    c: DistanceY(g6,g5) = 0
    c: DistanceY(g7,g6) = 0
    c: Distance(g4,g3) = 5.3
    c: Distance(g4,g2) = 5.2
    c: DistanceX(g4,g5) = 11.67
    c: DistanceX(g5,g6) = 11.67
    c: DistanceX(g6,g7) = 11.67
    c: DistanceY(g3,g3) = 15.2
    c: DistanceX(g0,g0) = 44
FEATURE [PartDesign::Pad] Pad
  Direction = (1,1,1)
  Length = 3
  Length2 = 100
  Profile = -> Sketch
  Type = 0
FEATURE [PartDesign::Pad] Pad001
  BaseFeature = -> Pad
  Direction = (1,1,1)
  Length = 2
  Length2 = 100
  Profile = -> Sketch001
  Reversed = true
  Type = 0
FEATURE [PartDesign::SubtractiveBox] Box
  AttacherType = Attacher::AttachEngine3D
  BaseFeature = -> Pad001
  Height = 1.7
  Length = 44
  MapMode = 49
  Placement = pos=(44,15.2,0) rot=(0,0.707107,-0.707107;3.14159rad)
  Support = -> [Pad001]
  Width = 4
FEATURE [PartDesign::Body] Body
  Group = -> [LCS_0001,Sketch,Pad,Sketch001,Pad001,Box]
  Origin = -> Origin001
  Placement = pos=(-80,0,0) rot=(0,0,1;0rad)
  Tip = -> Box
FEATURE [PartDesign::Pad] Pad005
  Direction = (1,1,1)
  Length = 1.6
  Length2 = 100
  Profile = -> Sketch005
  Reversed = true
  Type = 0
FEATURE [PartDesign::Body] Body005
  Group = -> [Sketch005,Pad005]
  Origin = -> Origin006
  Placement = pos=(0,0,-2) rot=(0,0,1;0rad)
  Tip = -> Pad005
FEATURE [Part::FeaturePython] Connect  # WARN: FeaturePython — macro-defined, semantics opaque (R4)
  Objects = -> [Body004,Body005]
  Tolerance = 0
FEATURE [PartDesign::FeatureBase] BaseFeature001
  BaseFeature = -> Connect
FEATURE [PartDesign::Body] Body003
  BaseFeature = -> Connect
  Group = -> [BaseFeature001]
  Origin = -> Origin004
  Tip = -> BaseFeature001
FEATURE [PartDesign::Line] HoleAxis_10
  AttacherType = Attacher::AttachEngineLine
  Length = 4.2272
  MapMode = 19
  Placement = pos=(38.7,10,5e-16) rot=(0,0,1;0rad)
  ResizeMode = 1
  Support = -> [Box005]
FEATURE [PartDesign::Body] Body001
  Group = -> [LCS_0002,Sketch003,Pad003,Sketch002,Pad002,Box005,HoleAxis_10]
  Origin = -> Origin002
  Tip = -> Box005
FEATURE [Part::MultiFuse] Fusion
  Shapes = -> [Body,Body001,Body002,Body003]
FEATURE [PartDesign::Line] HoleAxis_1 .. HoleAxis_4  x4 (patterned run collapsed; names and placements below)
  AttacherType = Attacher::AttachEngineLine
  Length = 4.50902
  MapMode = 19
  ResizeMode = 1
  Support = -> [Fusion]
  placements: 4 in arithmetic series — first pos=(-74.7,10,3.4e-15) rot=(0,0,1;0rad), step (11.67,-1.77636e-15,-1.1e-15), last pos=(-39.69,10,3e-16) rot=(0,0,1;0rad)
FEATURE [PartDesign::Line] HoleAxis_5
  AttacherType = Attacher::AttachEngineLine
  Length = 5.63627
  MapMode = 19
  Placement = pos=(-2.7,9.7,-1) rot=(0,0,1;0rad)
  ResizeMode = 1
  Support = -> [Fusion]
FEATURE [PartDesign::Line] HoleAxis_6
  AttacherType = Attacher::AttachEngineLine
  Length = 5.63627
  MapMode = 19
  Placement = pos=(-33.3,9.7,-1) rot=(0,0,1;0rad)
  ResizeMode = 1
  Support = -> [Fusion]
FEATURE [PartDesign::Line] HoleAxis_7
  AttacherType = Attacher::AttachEngineLine
  Length = 4.2272
  MapMode = 19
  Placement = pos=(15.36,10,2.5e-15) rot=(0,0,1;1.5708rad)
  ResizeMode = 1
  Support = -> [Fusion]
FEATURE [PartDesign::Line] HoleAxis_8
  AttacherType = Attacher::AttachEngineLine
  Length = 4.2272
  MapMode = 19
  Placement = pos=(27.03,10,1.5e-15) rot=(0,0,1;0rad)
  ResizeMode = 1
  Support = -> [Fusion]
FEATURE [PartDesign::Line] HoleAxis_9
  AttacherType = Attacher::AttachEngineLine
  Length = 4.2272
  MapMode = 19
  Placement = pos=(3.69,10,3.5e-15) rot=(0,0,1;0rad)
  ResizeMode = 1
  Support = -> [Fusion]
FEATURE [PartDesign::Line] HoleAxis_11
  AttacherType = Attacher::AttachEngineLine
  Length = 4.2272
  MapMode = 19
  Placement = pos=(38.7,10,5e-16) rot=(0,0,1;0rad)
  ResizeMode = 1
  Support = -> [Fusion]
FEATURE [App::Part] Part
  Group = -> [LCS_0,Body,Body001,Body002,Box006,Fusion,HoleAxis_1,HoleAxis_2,HoleAxis_3,HoleAxis_4,HoleAxis_5,HoleAxis_6,HoleAxis_7,HoleAxis_8,HoleAxis_9,Body004,Connect,HoleAxis_11]
  Origin = -> Origin
---- part switches.FCStd = doc fcstd_f9bec8acf46d ----
FCSTD DOCUMENT  (FreeCAD 0.19R24291 (Git))
Label: switches
License: Creative Commons Attribution-NonCommercial-ShareAlike
LicenseURL: http://creativecommons.org/licenses/by-nc-sa/4.0/
objects: App::Link×92, PartDesign::Line×28, Part::Feature×12, App::LinkGroup×5, PartDesign::CoordinateSystem×2, Sketcher::SketchObject×1, App::Part×1
note: 43 computed .brp shape members not serialized (recipe doc carries the construction recipe); baked Part::Feature solids carry a one-line shape summary decoded from their .brp

FEATURE [PartDesign::CoordinateSystem] Local_CS_57a1
  AttacherType = Attacher::AttachEngine3D
FEATURE [Part::Feature] Pcb_57a1
  Placement = pos=(-102.25,63.55,0) rot=(0,0,1;0rad)
  shape: bbox 120 x 75 x 1 mm, 1846 faces (baked)
FEATURE [Sketcher::SketchObject] PCB_Sketch_57a1
  FullyConstrained = false
  sketch-geometry (4):
    g0: LineSegment StartX=120 StartY=0 StartZ=0 EndX=120 EndY=-75 EndZ=0
    g1: LineSegment StartX=0 StartY=0 StartZ=0 EndX=120 EndY=0 EndZ=0
    g2: LineSegment StartX=0 StartY=-75 StartZ=0 EndX=0 EndY=0 EndZ=0
    g3: LineSegment StartX=120 StartY=-75 StartZ=0 EndX=0 EndY=-75 EndZ=0
  constraints (4):
    c: Coincident(g2,g3)
    c: Coincident(g1,g2)
    c: Coincident(g0,g3)
    c: Coincident(g0,g1)
FEATURE [App::LinkGroup] Board_Geoms_57a1
  ElementList = -> [Pcb_57a1,Local_CS_57a1,PCB_Sketch_57a1]
  LinkMode = 0
FEATURE [Part::Feature] Shape  label="U102_SOIC_8_1EP_39x49mm_P127mm_606CF202"
  Placement = pos=(64.9625,-38.595,0) rot=(0,0,1;3.14159rad)
  shape: bbox 6 x 4.9 x 1.75 mm, 161 faces (baked)
FEATURE [App::Link] U102_SOIC_8_1EP_39x49mm_P127mm_606CF202_ln_  label="U101_SOIC_8_1EP_39x49mm_P127mm_60690A70"
  LinkPlacement = pos=(55,-38.65,0) rot=(0,0,1;0rad)
  LinkedObject = -> Shape
  Placement = pos=(55,-38.65,0) rot=(0,0,1;0rad)
FEATURE [Part::Feature] Shape001  label="Q112_Infineon_PG_HSOF_8_1_606C635D"
  Placement = pos=(99.55,-51.1,0) rot=(0,0,1;1.5708rad)
  shape: bbox 9.9 x 11.68 x 2.32 mm, 90 faces (baked)
FEATURE [App::Link] Q112_Infineon_PG_HSOF_8_1_606C635D_ln_  label="Q111_Infineon_PG_HSOF_8_1_606C5E26"
  LinkPlacement = pos=(87.875,-51.1,0) rot=(0,0,1;1.5708rad)
  LinkedObject = -> Shape001
  Placement = pos=(87.875,-51.1,0) rot=(0,0,1;1.5708rad)
FEATURE [App::Link] Q112_Infineon_PG_HSOF_8_1_606C635D_ln_001  label="Q110_Infineon_PG_HSOF_8_1_606C5F73"
  LinkPlacement = pos=(76.2,-51.1,0) rot=(0,0,1;1.5708rad)
  LinkedObject = -> Shape001
  Placement = pos=(76.2,-51.1,0) rot=(0,0,1;1.5708rad)
FEATURE [App::Link] Q112_Infineon_PG_HSOF_8_1_606C635D_ln_002  label="Q109_Infineon_PG_HSOF_8_1_60699C33"
  LinkPlacement = pos=(43.8,-51.1,0) rot=(0,0,1;1.5708rad)
  LinkedObject = -> Shape001
  Placement = pos=(43.8,-51.1,0) rot=(0,0,1;1.5708rad)
FEATURE [App::Link] Q112_Infineon_PG_HSOF_8_1_606C635D_ln_003  label="Q108_Infineon_PG_HSOF_8_1_60699B67"
  LinkPlacement = pos=(32.125,-51.1,0) rot=(0,0,1;1.5708rad)
  LinkedObject = -> Shape001
  Placement = pos=(32.125,-51.1,0) rot=(0,0,1;1.5708rad)
FEATURE [App::Link] Q112_Infineon_PG_HSOF_8_1_606C635D_ln_004  label="Q107_Infineon_PG_HSOF_8_1_60699CFF"
  LinkPlacement = pos=(20.45,-51.1,0) rot=(0,0,1;1.5708rad)
  LinkedObject = -> Shape001
  Placement = pos=(20.45,-51.1,0) rot=(0,0,1;1.5708rad)
FEATURE [App::Link] Q112_Infineon_PG_HSOF_8_1_606C635D_ln_005  label="Q106_Infineon_PG_HSOF_8_1_606C6210"
  LinkPlacement = pos=(99.55,-23.9,0) rot=(0,0,1;1.5708rad)
  LinkedObject = -> Shape001
  Placement = pos=(99.55,-23.9,0) rot=(0,0,1;1.5708rad)
FEATURE [App::Link] Q112_Infineon_PG_HSOF_8_1_606C635D_ln_006  label="Q105_Infineon_PG_HSOF_8_1_606C6780"
  LinkPlacement = pos=(87.875,-23.9,0) rot=(0,0,1;1.5708rad)
  LinkedObject = -> Shape001
  Placement = pos=(87.875,-23.9,0) rot=(0,0,1;1.5708rad)
FEATURE [App::Link] Q112_Infineon_PG_HSOF_8_1_606C635D_ln_007  label="Q104_Infineon_PG_HSOF_8_1_606C60C3"
  LinkPlacement = pos=(76.2,-23.9,0) rot=(0,0,1;1.5708rad)
  LinkedObject = -> Shape001
  Placement = pos=(76.2,-23.9,0) rot=(0,0,1;1.5708rad)
FEATURE [App::Link] Q112_Infineon_PG_HSOF_8_1_606C635D_ln_008  label="Q103_Infineon_PG_HSOF_8_1_605C8D17"
  LinkPlacement = pos=(43.8,-23.9,0) rot=(0,0,1;1.5708rad)
  LinkedObject = -> Shape001
  Placement = pos=(43.8,-23.9,0) rot=(0,0,1;1.5708rad)
FEATURE [App::Link] Q112_Infineon_PG_HSOF_8_1_606C635D_ln_009  label="Q102_Infineon_PG_HSOF_8_1_605C4D4F"
  LinkPlacement = pos=(32.125,-23.9,0) rot=(0,0,1;1.5708rad)
  LinkedObject = -> Shape001
  Placement = pos=(32.125,-23.9,0) rot=(0,0,1;1.5708rad)
FEATURE [App::Link] Q112_Infineon_PG_HSOF_8_1_606C635D_ln_010  label="Q101_Infineon_PG_HSOF_8_1_605C4D0A"
  LinkPlacement = pos=(20.45,-23.9,0) rot=(0,0,1;1.5708rad)
  LinkedObject = -> Shape001
  Placement = pos=(20.45,-23.9,0) rot=(0,0,1;1.5708rad)
FEATURE [Part::Feature] Shape002  label="Rsn108_R_1210_3225Metric_607492AA"
  Placement = pos=(109.97,-50.65,0) rot=(0,0,-1;1.5708rad)
  shape: bbox 2.5 x 3.2 x 0.55 mm, 26 faces (baked)
FEATURE [App::Link] Rsn108_R_1210_3225Metric_607492AA_ln_  label="Rsn107_R_1210_3225Metric_60749299"
  LinkPlacement = pos=(106.75,-50.65,0) rot=(0,0,-1;1.5708rad)
  LinkedObject = -> Shape002
  Placement = pos=(106.75,-50.65,0) rot=(0,0,-1;1.5708rad)
FEATURE [App::Link] Rsn108_R_1210_3225Metric_607492AA_ln_001  label="Rsn106_R_1210_3225Metric_60749288"
  LinkPlacement = pos=(10.05,-50.5,0) rot=(0,0,-1;1.5708rad)
  LinkedObject = -> Shape002
  Placement = pos=(10.05,-50.5,0) rot=(0,0,-1;1.5708rad)
FEATURE [App::Link] Rsn108_R_1210_3225Metric_607492AA_ln_002  label="Rsn105_R_1210_3225Metric_60749277"
  LinkPlacement = pos=(13.25,-50.5,0) rot=(0,0,-1;1.5708rad)
  LinkedObject = -> Shape002
  Placement = pos=(13.25,-50.5,0) rot=(0,0,-1;1.5708rad)
FEATURE [App::Link] Rsn108_R_1210_3225Metric_607492AA_ln_003  label="Rsn104_R_1210_3225Metric_60749266"
  LinkPlacement = pos=(109.95,-22.05,0) rot=(0,0,-1;1.5708rad)
  LinkedObject = -> Shape002
  Placement = pos=(109.95,-22.05,0) rot=(0,0,-1;1.5708rad)
FEATURE [App::Link] Rsn108_R_1210_3225Metric_607492AA_ln_004  label="Rsn102_R_1210_3225Metric_60749245"
  LinkPlacement = pos=(10.05,-22.05,0) rot=(0,0,-1;1.5708rad)
  LinkedObject = -> Shape002
  Placement = pos=(10.05,-22.05,0) rot=(0,0,-1;1.5708rad)
FEATURE [App::Link] Rsn108_R_1210_3225Metric_607492AA_ln_005  label="Rsn101_R_1210_3225Metric_60749234"
  LinkPlacement = pos=(13.25,-22.05,0) rot=(0,0,-1;1.5708rad)
  LinkedObject = -> Shape002
  Placement = pos=(13.25,-22.05,0) rot=(0,0,-1;1.5708rad)
FEATURE [Part::Feature] Shape003  label="Dsn108_D_SOD_123F_6074702B"
  Placement = pos=(115.15,-50.7,0) rot=(0,0,1;1.5708rad)
  shape: bbox 1.6 x 3.5 x 1.1 mm, 27 faces (baked)
FEATURE [App::Link] Dsn108_D_SOD_123F_6074702B_ln_  label="Dsn107_D_SOD_123F_60747012"
  LinkPlacement = pos=(112.8,-50.7,0) rot=(0,0,1;1.5708rad)
  LinkedObject = -> Shape003
  Placement = pos=(112.8,-50.7,0) rot=(0,0,1;1.5708rad)
FEATURE [App::Link] Dsn108_D_SOD_123F_6074702B_ln_001  label="Dsn106_D_SOD_123F_60746FF9"
  LinkPlacement = pos=(7.2,-50.6,0) rot=(0,0,1;1.5708rad)
  LinkedObject = -> Shape003
  Placement = pos=(7.2,-50.6,0) rot=(0,0,1;1.5708rad)
FEATURE [App::Link] Dsn108_D_SOD_123F_6074702B_ln_002  label="Dsn105_D_SOD_123F_60746FE0"
  LinkPlacement = pos=(4.85,-50.6,0) rot=(0,0,1;1.5708rad)
  LinkedObject = -> Shape003
  Placement = pos=(4.85,-50.6,0) rot=(0,0,1;1.5708rad)
FEATURE [App::Link] Dsn108_D_SOD_123F_6074702B_ln_003  label="Dsn104_D_SOD_123F_60746FC7"
  LinkPlacement = pos=(115.25,-22.05,0) rot=(0,0,1;1.5708rad)
  LinkedObject = -> Shape003
  Placement = pos=(115.25,-22.05,0) rot=(0,0,1;1.5708rad)
FEATURE [App::Link] Dsn108_D_SOD_123F_6074702B_ln_004  label="Dsn103_D_SOD_123F_60746FAE"
  LinkPlacement = pos=(112.85,-22.05,0) rot=(0,0,1;1.5708rad)
  LinkedObject = -> Shape003
  Placement = pos=(112.85,-22.05,0) rot=(0,0,1;1.5708rad)
FEATURE [App::Link] Dsn108_D_SOD_123F_6074702B_ln_005  label="Dsn102_D_SOD_123F_60746F95"
  LinkPlacement = pos=(7.25,-22,0) rot=(0,0,1;1.5708rad)
  LinkedObject = -> Shape003
  Placement = pos=(7.25,-22,0) rot=(0,0,1;1.5708rad)
FEATURE [App::Link] Dsn108_D_SOD_123F_6074702B_ln_006  label="Dsn101_D_SOD_123F_60746F7C"
  LinkPlacement = pos=(4.9,-22,0) rot=(0,0,1;1.5708rad)
  LinkedObject = -> Shape003
  Placement = pos=(4.9,-22,0) rot=(0,0,1;1.5708rad)
FEATURE [Part::Feature] Shape004  label="Csn108_C_1210_3225Metric_60746C07"
  Placement = pos=(106.75,-55.65,0) rot=(0,0,-1;1.5708rad)
  shape: bbox 2.5 x 3.2 x 2.5 mm, 28 faces (baked)
FEATURE [App::Link] Csn108_C_1210_3225Metric_60746C07_ln_  label="Csn107_C_1210_3225Metric_60746BF6"
  LinkPlacement = pos=(110,-55.65,0) rot=(0,0,-1;1.5708rad)
  LinkedObject = -> Shape004
  Placement = pos=(110,-55.65,0) rot=(0,0,-1;1.5708rad)
FEATURE [App::Link] Csn108_C_1210_3225Metric_60746C07_ln_001  label="Csn106_C_1210_3225Metric_60746BE5"
  LinkPlacement = pos=(10,-55.55,0) rot=(0,0,-1;1.5708rad)
  LinkedObject = -> Shape004
  Placement = pos=(10,-55.55,0) rot=(0,0,-1;1.5708rad)
FEATURE [App::Link] Csn108_C_1210_3225Metric_60746C07_ln_002  label="Csn105_C_1210_3225Metric_60746BD4"
  LinkPlacement = pos=(13.25,-55.55,0) rot=(0,0,-1;1.5708rad)
  LinkedObject = -> Shape004
  Placement = pos=(13.25,-55.55,0) rot=(0,0,-1;1.5708rad)
FEATURE [App::Link] Csn108_C_1210_3225Metric_60746C07_ln_003  label="Csn104_C_1210_3225Metric_60746BC3"
  LinkPlacement = pos=(109.95,-27.05,0) rot=(0,0,-1;1.5708rad)
  LinkedObject = -> Shape004
  Placement = pos=(109.95,-27.05,0) rot=(0,0,-1;1.5708rad)
FEATURE [App::Link] Csn108_C_1210_3225Metric_60746C07_ln_004  label="Csn102_C_1210_3225Metric_60746BA2"
  LinkPlacement = pos=(10.05,-27.05,0) rot=(0,0,-1;1.5708rad)
  LinkedObject = -> Shape004
  Placement = pos=(10.05,-27.05,0) rot=(0,0,-1;1.5708rad)
FEATURE [App::Link] Csn108_C_1210_3225Metric_60746C07_ln_005  label="Csn101_C_1210_3225Metric_60746B91"
  LinkPlacement = pos=(13.3,-27.05,0) rot=(0,0,-1;1.5708rad)
  LinkedObject = -> Shape004
  Placement = pos=(13.3,-27.05,0) rot=(0,0,-1;1.5708rad)
FEATURE [Part::Feature] Shape005  label="TH101_R_0805_2012Metric_606C0318"
  Placement = pos=(69.5,-51.775,0) rot=(0,0,1;1.5708rad)
  shape: bbox 1.2 x 2 x 0.45 mm, 26 faces (baked)
FEATURE [Part::Feature] Shape006  label="C111_C_0805_2012Metric_606CF1B7"
  Placement = pos=(66.425,-43.995,0) rot=(0,0,1;3.14159rad)
  shape: bbox 2 x 1.25 x 1.25 mm, 28 faces (baked)
FEATURE [App::Link] Csn108_C_1210_3225Metric_60746C07_ln_006  label="C110_C_1210_3225Metric_606CF49C"
  LinkPlacement = pos=(66.3625,-46.695,0) rot=(0,0,1;0rad)
  LinkedObject = -> Shape004
  Placement = pos=(66.3625,-46.695,0) rot=(0,0,1;0rad)
FEATURE [App::Link] Csn108_C_1210_3225Metric_60746C07_ln_007  label="C122_C_1210_3225Metric_606CF17E"
  LinkPlacement = pos=(64.8125,-32.795,0) rot=(0,0,-1;1.5708rad)
  LinkedObject = -> Shape004
  Placement = pos=(64.8125,-32.795,0) rot=(0,0,-1;1.5708rad)
FEATURE [Part::Feature] Shape007  label="C134_C_0603_1608Metric_606C0308"
  Placement = pos=(67.6,-51.75,0) rot=(0,0,1;1.5708rad)
  shape: bbox 0.8 x 1.6 x 0.8 mm, 28 faces (baked)
FEATURE [Part::Feature] Shape008  label="R117_R_0603_1608Metric_606C02F8"
  Placement = pos=(65,-52.575,0) rot=(0,0,1;0rad)
  shape: bbox 1.6 x 0.8 x 0.45 mm, 26 faces (baked)
FEATURE [Part::Feature] Shape009  label="D118_D_SOD_323_606ADB94"
  Placement = pos=(57.95,-43.65,0) rot=(0,0,1;1.5708rad)
  shape: bbox 1.25 x 2.5 x 1.1 mm, 67 faces (baked)
FEATURE [App::Link] R117_R_0603_1608Metric_606C02F8_ln_  label="R137_R_0603_1608Metric_606CF436"
  LinkPlacement = pos=(69.8125,-33.795,0) rot=(0,0,1;1.5708rad)
  LinkedObject = -> Shape008
  Placement = pos=(69.8125,-33.795,0) rot=(0,0,1;1.5708rad)
FEATURE [App::Link] R117_R_0603_1608Metric_606C02F8_ln_001  label="R136_R_0603_1608Metric_606AA3FF"
  LinkPlacement = pos=(50.15,-43.45,0) rot=(0,0,-1;1.5708rad)
  LinkedObject = -> Shape008
  Placement = pos=(50.15,-43.45,0) rot=(0,0,-1;1.5708rad)
FEATURE [App::Link] Dsn108_D_SOD_123F_6074702B_ln_007  label="D117_D_SOD_123F_606A943E"
  LinkPlacement = pos=(100.45,-56.45,-1) rot=(1,0,0;3.14159rad)
  LinkedObject = -> Shape003
  Placement = pos=(100.45,-56.45,-1) rot=(1,0,0;3.14159rad)
FEATURE [App::Link] Dsn108_D_SOD_123F_6074702B_ln_008  label="D116_D_SOD_123F_606A9425"
  LinkPlacement = pos=(88.775,-56.45,-1) rot=(1,0,0;3.14159rad)
  LinkedObject = -> Shape003
  Placement = pos=(88.775,-56.45,-1) rot=(1,0,0;3.14159rad)
FEATURE [App::Link] Dsn108_D_SOD_123F_6074702B_ln_009  label="D115_D_SOD_123F_606A940C"
  LinkPlacement = pos=(77.1,-56.45,-1) rot=(1,0,0;3.14159rad)
  LinkedObject = -> Shape003
  Placement = pos=(77.1,-56.45,-1) rot=(1,0,0;3.14159rad)
FEATURE [App::Link] D118_D_SOD_323_606ADB94_ln_  label="D114_D_SOD_323_606CF3BC"
  LinkPlacement = pos=(62.0125,-33.595,0) rot=(0,0,-1;1.5708rad)
  LinkedObject = -> Shape009
  Placement = pos=(62.0125,-33.595,0) rot=(0,0,-1;1.5708rad)
FEATURE [App::Link] Dsn108_D_SOD_123F_6074702B_ln_010  label="D113_D_SOD_123F_606A93DB"
  LinkPlacement = pos=(100.45,-29.25,-1) rot=(1,0,0;3.14159rad)
  LinkedObject = -> Shape003
  Placement = pos=(100.45,-29.25,-1) rot=(1,0,0;3.14159rad)
FEATURE [App::Link] Dsn108_D_SOD_123F_6074702B_ln_011  label="D112_D_SOD_123F_606A93C2"
  LinkPlacement = pos=(88.775,-29.25,-1) rot=(1,0,0;3.14159rad)
  LinkedObject = -> Shape003
  Placement = pos=(88.775,-29.25,-1) rot=(1,0,0;3.14159rad)
FEATURE [App::Link] Dsn108_D_SOD_123F_6074702B_ln_012  label="D111_D_SOD_123F_606CF303"
  LinkPlacement = pos=(67.8125,-33.395,0) rot=(0,0,1;1.5708rad)
  LinkedObject = -> Shape003
  Placement = pos=(67.8125,-33.395,0) rot=(0,0,1;1.5708rad)
FEATURE [App::Link] Dsn108_D_SOD_123F_6074702B_ln_013  label="D110_D_SOD_123F_606CF34B"
  LinkPlacement = pos=(70.0125,-41.95,0) rot=(0,0,-1;1.5708rad)
  LinkedObject = -> Shape003
  Placement = pos=(70.0125,-41.95,0) rot=(0,0,-1;1.5708rad)
FEATURE [App::Link] Dsn108_D_SOD_123F_6074702B_ln_014  label="D109_D_SOD_123F_606A9377"
  LinkPlacement = pos=(77.1,-29.25,-1) rot=(1,0,0;3.14159rad)
  LinkedObject = -> Shape003
  Placement = pos=(77.1,-29.25,-1) rot=(1,0,0;3.14159rad)
FEATURE [App::Link] Dsn108_D_SOD_123F_6074702B_ln_015  label="D108_D_SOD_123F_606A935E"
  LinkPlacement = pos=(44.7,-56.45,-1) rot=(1,0,0;3.14159rad)
  LinkedObject = -> Shape003
  Placement = pos=(44.7,-56.45,-1) rot=(1,0,0;3.14159rad)
FEATURE [App::Link] Dsn108_D_SOD_123F_6074702B_ln_016  label="D107_D_SOD_123F_606A9345"
  LinkPlacement = pos=(33.025,-56.45,-1) rot=(1,0,0;3.14159rad)
  LinkedObject = -> Shape003
  Placement = pos=(33.025,-56.45,-1) rot=(1,0,0;3.14159rad)
FEATURE [App::Link] Dsn108_D_SOD_123F_6074702B_ln_017  label="D106_D_SOD_123F_606A932C"
  LinkPlacement = pos=(21.35,-56.45,-1) rot=(1,0,0;3.14159rad)
  LinkedObject = -> Shape003
  Placement = pos=(21.35,-56.45,-1) rot=(1,0,0;3.14159rad)
FEATURE [App::Link] Dsn108_D_SOD_123F_6074702B_ln_018  label="D105_D_SOD_123F_606A9313"
  LinkPlacement = pos=(44.7,-29.25,-1) rot=(1,0,0;3.14159rad)
  LinkedObject = -> Shape003
  Placement = pos=(44.7,-29.25,-1) rot=(1,0,0;3.14159rad)
FEATURE [App::Link] Dsn108_D_SOD_123F_6074702B_ln_019  label="D104_D_SOD_123F_606A92FA"
  LinkPlacement = pos=(33.025,-29.25,-1) rot=(1,0,0;3.14159rad)
  LinkedObject = -> Shape003
  Placement = pos=(33.025,-29.25,-1) rot=(1,0,0;3.14159rad)
FEATURE [App::Link] Dsn108_D_SOD_123F_6074702B_ln_020  label="D103_D_SOD_123F_606A92E1"
  LinkPlacement = pos=(52.15,-43.85,0) rot=(0,0,-1;1.5708rad)
  LinkedObject = -> Shape003
  Placement = pos=(52.15,-43.85,0) rot=(0,0,-1;1.5708rad)
FEATURE [App::Link] Dsn108_D_SOD_123F_6074702B_ln_021  label="D102_D_SOD_123F_606A92C8"
  LinkPlacement = pos=(49.95,-35.25,0) rot=(0,0,1;1.5708rad)
  LinkedObject = -> Shape003
  Placement = pos=(49.95,-35.25,0) rot=(0,0,1;1.5708rad)
FEATURE [App::Link] Dsn108_D_SOD_123F_6074702B_ln_022  label="D101_D_SOD_123F_606A92AF"
  LinkPlacement = pos=(21.35,-29.25,-1) rot=(1,0,0;3.14159rad)
  LinkedObject = -> Shape003
  Placement = pos=(21.35,-29.25,-1) rot=(1,0,0;3.14159rad)
FEATURE [App::Link] C134_C_0603_1608Metric_606C0308_ln_  label="C196_C_0603_1608Metric_606CF2C2"
  LinkPlacement = pos=(66.2875,-42.195,0) rot=(0,0,1;3.14159rad)
  LinkedObject = -> Shape007
  Placement = pos=(66.2875,-42.195,0) rot=(0,0,1;3.14159rad)
FEATURE [App::Link] C134_C_0603_1608Metric_606C0308_ln_001  label="C195_C_0603_1608Metric_606A9285"
  LinkPlacement = pos=(53.6875,-35.05,0) rot=(0,0,1;0rad)
  LinkedObject = -> Shape007
  Placement = pos=(53.6875,-35.05,0) rot=(0,0,1;0rad)
FEATURE [App::Link] R117_R_0603_1608Metric_606C02F8_ln_002  label="R135_R_0603_1608Metric_606977C6"
  LinkPlacement = pos=(103.65,-55.65,-1) rot=(0.707107,0.707107,0;3.14159rad)
  LinkedObject = -> Shape008
  Placement = pos=(103.65,-55.65,-1) rot=(0.707107,0.707107,0;3.14159rad)
FEATURE [App::Link] R117_R_0603_1608Metric_606C02F8_ln_003  label="R134_R_0603_1608Metric_606977B5"
  LinkPlacement = pos=(91.975,-55.65,-1) rot=(0.707107,0.707107,0;3.14159rad)
  LinkedObject = -> Shape008
  Placement = pos=(91.975,-55.65,-1) rot=(0.707107,0.707107,0;3.14159rad)
FEATURE [App::Link] R117_R_0603_1608Metric_606C02F8_ln_004  label="R133_R_0603_1608Metric_606977A4"
  LinkPlacement = pos=(80.3,-55.65,-1) rot=(0.707107,0.707107,0;3.14159rad)
  LinkedObject = -> Shape008
  Placement = pos=(80.3,-55.65,-1) rot=(0.707107,0.707107,0;3.14159rad)
FEATURE [App::Link] R117_R_0603_1608Metric_606C02F8_ln_005  label="R132_R_0603_1608Metric_60697793"
  LinkPlacement = pos=(103.65,-28.45,-1) rot=(0.707107,0.707107,0;3.14159rad)
  LinkedObject = -> Shape008
  Placement = pos=(103.65,-28.45,-1) rot=(0.707107,0.707107,0;3.14159rad)
FEATURE [App::Link] R117_R_0603_1608Metric_606C02F8_ln_006  label="R131_R_0603_1608Metric_60697782"
  LinkPlacement = pos=(91.975,-28.45,-1) rot=(0.707107,0.707107,0;3.14159rad)
  LinkedObject = -> Shape008
  Placement = pos=(91.975,-28.45,-1) rot=(0.707107,0.707107,0;3.14159rad)
FEATURE [App::Link] R117_R_0603_1608Metric_606C02F8_ln_007  label="R130_R_0603_1608Metric_60697771"
  LinkPlacement = pos=(80.3,-28.45,-1) rot=(0.707107,0.707107,0;3.14159rad)
  LinkedObject = -> Shape008
  Placement = pos=(80.3,-28.45,-1) rot=(0.707107,0.707107,0;3.14159rad)
FEATURE [App::Link] R117_R_0603_1608Metric_606C02F8_ln_008  label="R129_R_0603_1608Metric_60697760"
  LinkPlacement = pos=(47.9,-55.65,-1) rot=(0.707107,0.707107,0;3.14159rad)
  LinkedObject = -> Shape008
  Placement = pos=(47.9,-55.65,-1) rot=(0.707107,0.707107,0;3.14159rad)
FEATURE [App::Link] R117_R_0603_1608Metric_606C02F8_ln_009  label="R128_R_0603_1608Metric_6069774F"
  LinkPlacement = pos=(36.225,-55.65,-1) rot=(0.707107,0.707107,0;3.14159rad)
  LinkedObject = -> Shape008
  Placement = pos=(36.225,-55.65,-1) rot=(0.707107,0.707107,0;3.14159rad)
FEATURE [App::Link] R117_R_0603_1608Metric_606C02F8_ln_010  label="R127_R_0603_1608Metric_6069773E"
  LinkPlacement = pos=(24.55,-55.65,-1) rot=(0.707107,0.707107,0;3.14159rad)
  LinkedObject = -> Shape008
  Placement = pos=(24.55,-55.65,-1) rot=(0.707107,0.707107,0;3.14159rad)
FEATURE [App::Link] R117_R_0603_1608Metric_606C02F8_ln_011  label="R126_R_0603_1608Metric_6069772D"
  LinkPlacement = pos=(47.9,-28.45,-1) rot=(0.707107,0.707107,0;3.14159rad)
  LinkedObject = -> Shape008
  Placement = pos=(47.9,-28.45,-1) rot=(0.707107,0.707107,0;3.14159rad)
FEATURE [App::Link] R117_R_0603_1608Metric_606C02F8_ln_012  label="R125_R_0603_1608Metric_6069771C"
  LinkPlacement = pos=(36.225,-28.45,-1) rot=(0.707107,0.707107,0;3.14159rad)
  LinkedObject = -> Shape008
  Placement = pos=(36.225,-28.45,-1) rot=(0.707107,0.707107,0;3.14159rad)
FEATURE [App::Link] R117_R_0603_1608Metric_606C02F8_ln_013  label="R124_R_0603_1608Metric_6069770B"
  LinkPlacement = pos=(24.55,-28.45,-1) rot=(0.707107,0.707107,0;3.14159rad)
  LinkedObject = -> Shape008
  Placement = pos=(24.55,-28.45,-1) rot=(0.707107,0.707107,0;3.14159rad)
FEATURE [App::Link] C134_C_0603_1608Metric_606C0308_ln_002  label="C131_C_0603_1608Metric_606DFE7B"
  LinkPlacement = pos=(51.3875,-21.85,0) rot=(0,0,1;3.14159rad)
  LinkedObject = -> Shape007
  Placement = pos=(51.3875,-21.85,0) rot=(0,0,1;3.14159rad)
FEATURE [App::Link] R117_R_0603_1608Metric_606C02F8_ln_014  label="R123_R_0603_1608Metric_606E087C"
  LinkPlacement = pos=(68.55,-19.15,0) rot=(0,0,1;0rad)
  LinkedObject = -> Shape008
  Placement = pos=(68.55,-19.15,0) rot=(0,0,1;0rad)
FEATURE [App::Link] R117_R_0603_1608Metric_606C02F8_ln_015  label="R122_R_0603_1608Metric_606E086B"
  LinkPlacement = pos=(68.55,-25.45,0) rot=(0,0,1;0rad)
  LinkedObject = -> Shape008
  Placement = pos=(68.55,-25.45,0) rot=(0,0,1;0rad)
FEATURE [App::Link] R117_R_0603_1608Metric_606C02F8_ln_016  label="R121_R_0603_1608Metric_606E085A"
  LinkPlacement = pos=(51.35,-23.55,0) rot=(0,0,1;3.14159rad)
  LinkedObject = -> Shape008
  Placement = pos=(51.35,-23.55,0) rot=(0,0,1;3.14159rad)
FEATURE [App::Link] R117_R_0603_1608Metric_606C02F8_ln_017  label="R120_R_0603_1608Metric_606E0849"
  LinkPlacement = pos=(68.55,-17.55,0) rot=(0,0,1;3.14159rad)
  LinkedObject = -> Shape008
  Placement = pos=(68.55,-17.55,0) rot=(0,0,1;3.14159rad)
FEATURE [App::Link] R117_R_0603_1608Metric_606C02F8_ln_018  label="R119_R_0603_1608Metric_606E0838"
  LinkPlacement = pos=(68.55,-27.05,0) rot=(0,0,1;3.14159rad)
  LinkedObject = -> Shape008
  Placement = pos=(68.55,-27.05,0) rot=(0,0,1;3.14159rad)
FEATURE [App::Link] R117_R_0603_1608Metric_606C02F8_ln_019  label="R118_R_0603_1608Metric_606E0827"
  LinkPlacement = pos=(51.3375,-25.25,0) rot=(0,0,1;0rad)
  LinkedObject = -> Shape008
  Placement = pos=(51.3375,-25.25,0) rot=(0,0,1;0rad)
FEATURE [App::Link] C134_C_0603_1608Metric_606C0308_ln_003  label="C133_C_0603_1608Metric_606DFE9D"
  LinkPlacement = pos=(68.5125,-20.75,0) rot=(0,0,1;0rad)
  LinkedObject = -> Shape007
  Placement = pos=(68.5125,-20.75,0) rot=(0,0,1;0rad)
FEATURE [App::Link] C134_C_0603_1608Metric_606C0308_ln_004  label="C132_C_0603_1608Metric_606DFE8C"
  LinkPlacement = pos=(68.5125,-23.75,0) rot=(0,0,1;0rad)
  LinkedObject = -> Shape007
  Placement = pos=(68.5125,-23.75,0) rot=(0,0,1;0rad)
FEATURE [App::Link] TH101_R_0805_2012Metric_606C0318_ln_  label="R114_R_0805_2012Metric_606C6A2D"
  LinkPlacement = pos=(72.75,-56.35,-1) rot=(1,0,0;3.14159rad)
  LinkedObject = -> Shape005
  Placement = pos=(72.75,-56.35,-1) rot=(1,0,0;3.14159rad)
FEATURE [App::Link] TH101_R_0805_2012Metric_606C0318_ln_001  label="R113_R_0805_2012Metric_606C69FD"
  LinkPlacement = pos=(96.1,-29.15,-1) rot=(1,0,0;3.14159rad)
  LinkedObject = -> Shape005
  Placement = pos=(96.1,-29.15,-1) rot=(1,0,0;3.14159rad)
FEATURE [App::Link] TH101_R_0805_2012Metric_606C0318_ln_002  label="R115_R_0805_2012Metric_606C69CD"
  LinkPlacement = pos=(84.4,-56.35,-1) rot=(1,0,0;3.14159rad)
  LinkedObject = -> Shape005
  Placement = pos=(84.4,-56.35,-1) rot=(1,0,0;3.14159rad)
FEATURE [App::Link] TH101_R_0805_2012Metric_606C0318_ln_003  label="R116_R_0805_2012Metric_606C699D"
  LinkPlacement = pos=(96.1,-56.35,-1) rot=(1,0,0;3.14159rad)
  LinkedObject = -> Shape005
  Placement = pos=(96.1,-56.35,-1) rot=(1,0,0;3.14159rad)
FEATURE [App::Link] TH101_R_0805_2012Metric_606C0318_ln_004  label="R103_R_0805_2012Metric_606863C2"
  LinkPlacement = pos=(17,-29.15,-1) rot=(1,0,0;3.14159rad)
  LinkedObject = -> Shape005
  Placement = pos=(17,-29.15,-1) rot=(1,0,0;3.14159rad)
FEATURE [App::Link] C111_C_0805_2012Metric_606CF1B7_ln_  label="C108_C_0805_2012Metric_60685BB9"
  LinkPlacement = pos=(53.55,-33.25,0) rot=(0,0,1;0rad)
  LinkedObject = -> Shape006
  Placement = pos=(53.55,-33.25,0) rot=(0,0,1;0rad)
FEATURE [App::Link] TH101_R_0805_2012Metric_606C0318_ln_005  label="R107_R_0805_2012Metric_60686406"
  LinkPlacement = pos=(28.675,-56.35,-1) rot=(1,0,0;3.14159rad)
  LinkedObject = -> Shape005
  Placement = pos=(28.675,-56.35,-1) rot=(1,0,0;3.14159rad)
FEATURE [App::Link] Csn108_C_1210_3225Metric_60746C07_ln_008  label="C107_C_1210_3225Metric_60685BA8"
  LinkPlacement = pos=(53.5875,-30.65,0) rot=(0,0,1;3.14159rad)
  LinkedObject = -> Shape004
  Placement = pos=(53.5875,-30.65,0) rot=(0,0,1;3.14159rad)
FEATURE [App::Link] TH101_R_0805_2012Metric_606C0318_ln_006  label="R104_R_0805_2012Metric_606863D3"
  LinkPlacement = pos=(28.675,-29.15,-1) rot=(1,0,0;3.14159rad)
  LinkedObject = -> Shape005
  Placement = pos=(28.675,-29.15,-1) rot=(1,0,0;3.14159rad)
FEATURE [App::Link] TH101_R_0805_2012Metric_606C0318_ln_007  label="R105_R_0805_2012Metric_606863E4"
  LinkPlacement = pos=(40.35,-29.15,-1) rot=(1,0,0;3.14159rad)
  LinkedObject = -> Shape005
  Placement = pos=(40.35,-29.15,-1) rot=(1,0,0;3.14159rad)
FEATURE [App::Link] Csn108_C_1210_3225Metric_60746C07_ln_009  label="Csn103_C_1210_3225Metric_606C66EB"
  LinkPlacement = pos=(106.65,-27.05,0) rot=(0,0,-1;1.5708rad)
  LinkedObject = -> Shape004
  Placement = pos=(106.65,-27.05,0) rot=(0,0,-1;1.5708rad)
FEATURE [Part::Feature] Shape010  label="J105_PinHeader_2x10_P127mm_Vertical_SMD_606D32DE"
  Placement = pos=(60,-21.5,0) rot=(0,0,1;1.5708rad)
  shape: bbox 12.7 x 5.57 x 4.4 mm, 444 faces (baked)
FEATURE [App::Link] TH101_R_0805_2012Metric_606C0318_ln_008  label="R112_R_0805_2012Metric_606C665B"
  LinkPlacement = pos=(84.425,-29.15,-1) rot=(1,0,0;3.14159rad)
  LinkedObject = -> Shape005
  Placement = pos=(84.425,-29.15,-1) rot=(1,0,0;3.14159rad)
FEATURE [App::Link] TH101_R_0805_2012Metric_606C0318_ln_009  label="R108_R_0805_2012Metric_60686417"
  LinkPlacement = pos=(40.35,-56.35,-1) rot=(1,0,0;3.14159rad)
  LinkedObject = -> Shape005
  Placement = pos=(40.35,-56.35,-1) rot=(1,0,0;3.14159rad)
FEATURE [App::Link] Csn108_C_1210_3225Metric_60746C07_ln_010  label="C109_C_1210_3225Metric_60685BCA"
  LinkPlacement = pos=(55.15,-44.45,0) rot=(0,0,1;1.5708rad)
  LinkedObject = -> Shape004
  Placement = pos=(55.15,-44.45,0) rot=(0,0,1;1.5708rad)
FEATURE [App::Link] Rsn108_R_1210_3225Metric_607492AA_ln_006  label="Rsn103_R_1210_3225Metric_606C659B"
  LinkPlacement = pos=(106.65,-22.05,0) rot=(0,0,-1;1.5708rad)
  LinkedObject = -> Shape002
  Placement = pos=(106.65,-22.05,0) rot=(0,0,-1;1.5708rad)
FEATURE [App::LinkGroup] Top_57a1
  ElementList = -> [Shape,U102_SOIC_8_1EP_39x49mm_P127mm_606CF202_ln_,Shape001,Q112_Infineon_PG_HSOF_8_1_606C635D_ln_,Q112_Infineon_PG_HSOF_8_1_606C635D_ln_001,Q112_Infineon_PG_HSOF_8_1_606C635D_ln_002,Q112_Infineon_PG_HSOF_8_1_606C635D_ln_003,Q112_Infineon_PG_HSOF_8_1_606C635D_ln_004,Q112_Infineon_PG_HSOF_8_1_606C635D_ln_005,Q112_Infineon_PG_HSOF_8_1_606C635D_ln_006,Q112_Infineon_PG_HSOF_8_1_606C635D_ln_007,+56 more]
  LinkMode = 0
FEATURE [App::Link] TH101_R_0805_2012Metric_606C0318_ln_010  label="R106_R_0805_2012Metric_606863F5"
  LinkPlacement = pos=(17,-56.35,-1) rot=(1,0,0;3.14159rad)
  LinkedObject = -> Shape005
  Placement = pos=(17,-56.35,-1) rot=(1,0,0;3.14159rad)
FEATURE [App::Link] TH101_R_0805_2012Metric_606C0318_ln_011  label="R111_R_0805_2012Metric_606C653B"
  LinkPlacement = pos=(72.75,-29.15,-1) rot=(1,0,0;3.14159rad)
  LinkedObject = -> Shape005
  Placement = pos=(72.75,-29.15,-1) rot=(1,0,0;3.14159rad)
FEATURE [App::LinkGroup] Bot_57a1
  ElementList = -> [Dsn108_D_SOD_123F_6074702B_ln_007,Dsn108_D_SOD_123F_6074702B_ln_008,Dsn108_D_SOD_123F_6074702B_ln_009,Dsn108_D_SOD_123F_6074702B_ln_010,Dsn108_D_SOD_123F_6074702B_ln_011,Dsn108_D_SOD_123F_6074702B_ln_014,Dsn108_D_SOD_123F_6074702B_ln_015,Dsn108_D_SOD_123F_6074702B_ln_016,Dsn108_D_SOD_123F_6074702B_ln_017,Dsn108_D_SOD_123F_6074702B_ln_018,Dsn108_D_SOD_123F_6074702B_ln_019,+25 more]
  LinkMode = 0
FEATURE [App::LinkGroup] Step_Models_57a1
  ElementList = -> [Top_57a1,Bot_57a1]
  LinkMode = 0
FEATURE [App::LinkGroup] Board_57a1  label="Switches"
  ElementList = -> [Board_Geoms_57a1,Step_Models_57a1]
  LinkMode = 0
FEATURE [PartDesign::CoordinateSystem] LCS_0
  AttacherType = Attacher::AttachEngine3D
  MapMode = 2
  Support = -> [X_Axis]
FEATURE [PartDesign::Line] HoleAxis_1
  AttacherType = Attacher::AttachEngineLine
  Length = 4.50902
  MapMode = 19
  Placement = pos=(3.4,-8,0) rot=(0,0,1;0rad)
  ResizeMode = 1
  Support = -> [Pcb_57a1]
FEATURE [PartDesign::Line] HoleAxis_2
  AttacherType = Attacher::AttachEngineLine
  Length = 4.50902
  MapMode = 19
  Placement = pos=(15.0667,-8,0) rot=(0,0,1;0rad)
  ResizeMode = 1
  Support = -> [Pcb_57a1]
FEATURE [PartDesign::Line] HoleAxis_3
  AttacherType = Attacher::AttachEngineLine
  Length = 4.50902
  MapMode = 19
  Placement = pos=(26.7333,-8,0) rot=(0,0,1;0rad)
  ResizeMode = 1
  Support = -> [Pcb_57a1]
FEATURE [PartDesign::Line] HoleAxis_4
  AttacherType = Attacher::AttachEngineLine
  Length = 4.50902
  MapMode = 19
  Placement = pos=(38.4,-8,0) rot=(0,0,1;0rad)
  ResizeMode = 1
  Support = -> [Pcb_57a1]
FEATURE [PartDesign::Line] HoleAxis_5
  AttacherType = Attacher::AttachEngineLine
  Length = 4.50902
  MapMode = 19
  Placement = pos=(44.62,-7.71,0) rot=(0,0,1;0rad)
  ResizeMode = 1
  Support = -> [Pcb_57a1]
FEATURE [PartDesign::Line] HoleAxis_6
  AttacherType = Attacher::AttachEngineLine
  Length = 4.50902
  MapMode = 19
  Placement = pos=(75.27,-7.69792,0) rot=(0,0,1;0rad)
  ResizeMode = 1
  Support = -> [Pcb_57a1]
FEATURE [PartDesign::Line] HoleAxis_7
  AttacherType = Attacher::AttachEngineLine
  Length = 4.50902
  MapMode = 19
  Placement = pos=(81.6,-8,0) rot=(0,0,1;0rad)
  ResizeMode = 1
  Support = -> [Pcb_57a1]
FEATURE [PartDesign::Line] HoleAxis_8
  AttacherType = Attacher::AttachEngineLine
  Length = 4.50902
  MapMode = 19
  Placement = pos=(93.2667,-8,0) rot=(0,0,1;0rad)
  ResizeMode = 1
  Support = -> [Pcb_57a1]
FEATURE [PartDesign::Line] HoleAxis_9
  AttacherType = Attacher::AttachEngineLine
  Length = 4.50902
  MapMode = 19
  Placement = pos=(104.933,-8,0) rot=(0,0,1;0rad)
  ResizeMode = 1
  Support = -> [Pcb_57a1]
FEATURE [PartDesign::Line] HoleAxis_10
  AttacherType = Attacher::AttachEngineLine
  Length = 4.50902
  MapMode = 19
  Placement = pos=(116.6,-8,0) rot=(0,0,1;0rad)
  ResizeMode = 1
  Support = -> [Pcb_57a1]
FEATURE [PartDesign::Line] HoleAxis_11
  AttacherType = Attacher::AttachEngineLine
  Length = 4.50902
  MapMode = 19
  Placement = pos=(115.55,-37.84,0) rot=(0,0,1;0rad)
  ResizeMode = 1
  Support = -> [Pcb_57a1]
FEATURE [PartDesign::Line] HoleAxis_12
  AttacherType = Attacher::AttachEngineLine
  Length = 4.50902
  MapMode = 19
  Placement = pos=(102.55,-37.84,0) rot=(0,0,1;0rad)
  ResizeMode = 1
  Support = -> [Pcb_57a1]
FEATURE [PartDesign::Line] HoleAxis_13
  AttacherType = Attacher::AttachEngineLine
  Length = 4.50902
  MapMode = 19
  Placement = pos=(89.55,-37.84,0) rot=(0,0,1;0rad)
  ResizeMode = 1
  Support = -> [Pcb_57a1]
FEATURE [PartDesign::Line] HoleAxis_14
  AttacherType = Attacher::AttachEngineLine
  Length = 4.50902
  MapMode = 19
  Placement = pos=(76.55,-37.84,0) rot=(0,0,1;0rad)
  ResizeMode = 1
  Support = -> [Pcb_57a1]
FEATURE [PartDesign::Line] HoleAxis_15
  AttacherType = Attacher::AttachEngineLine
  Length = 4.50902
  MapMode = 19
  Placement = pos=(43.45,-37.9,0) rot=(0,0,1;0rad)
  ResizeMode = 1
  Support = -> [Pcb_57a1]
FEATURE [PartDesign::Line] HoleAxis_16
  AttacherType = Attacher::AttachEngineLine
  Length = 4.50902
  MapMode = 19
  Placement = pos=(30.45,-37.9,0) rot=(0,0,1;0rad)
  ResizeMode = 1
  Support = -> [Pcb_57a1]
FEATURE [PartDesign::Line] HoleAxis_17
  AttacherType = Attacher::AttachEngineLine
  Length = 4.50902
  MapMode = 19
  Placement = pos=(17.45,-37.9,0) rot=(0,0,1;0rad)
  ResizeMode = 1
  Support = -> [Pcb_57a1]
FEATURE [PartDesign::Line] HoleAxis_18
  AttacherType = Attacher::AttachEngineLine
  Length = 4.50902
  MapMode = 19
  Placement = pos=(4.45,-37.9,0) rot=(0,0,1;0rad)
  ResizeMode = 1
  Support = -> [Pcb_57a1]
FEATURE [PartDesign::Line] HoleAxis_19
  AttacherType = Attacher::AttachEngineLine
  Length = 4.50902
  MapMode = 19
  Placement = pos=(15.0667,-67,0) rot=(0,0,1;0rad)
  ResizeMode = 1
  Support = -> [Pcb_57a1]
FEATURE [PartDesign::Line] HoleAxis_20
  AttacherType = Attacher::AttachEngineLine
  Length = 4.50902
  MapMode = 19
  Placement = pos=(26.7333,-67,0) rot=(0,0,1;0rad)
  ResizeMode = 1
  Support = -> [Pcb_57a1]
FEATURE [PartDesign::Line] HoleAxis_21
  AttacherType = Attacher::AttachEngineLine
  Length = 4.50902
  MapMode = 19
  Placement = pos=(38.4,-67,0) rot=(0,0,1;0rad)
  ResizeMode = 1
  Support = -> [Pcb_57a1]
FEATURE [PartDesign::Line] HoleAxis_22
  AttacherType = Attacher::AttachEngineLine
  Length = 4.50902
  MapMode = 19
  Placement = pos=(44.73,-67.3021,0) rot=(0,0,1;0rad)
  ResizeMode = 1
  Support = -> [Pcb_57a1]
FEATURE [PartDesign::Line] HoleAxis_23
  AttacherType = Attacher::AttachEngineLine
  Length = 4.50902
  MapMode = 19
  Placement = pos=(75.38,-67.29,0) rot=(0,0,1;0rad)
  ResizeMode = 1
  Support = -> [Pcb_57a1]
FEATURE [PartDesign::Line] HoleAxis_24
  AttacherType = Attacher::AttachEngineLine
  Length = 4.50902
  MapMode = 19
  Placement = pos=(81.6,-67,0) rot=(0,0,1;0rad)
  ResizeMode = 1
  Support = -> [Pcb_57a1]
FEATURE [PartDesign::Line] HoleAxis_25
  AttacherType = Attacher::AttachEngineLine
  Length = 4.50902
  MapMode = 19
  Placement = pos=(93.2667,-67,0) rot=(0,0,1;0rad)
  ResizeMode = 1
  Support = -> [Pcb_57a1]
FEATURE [PartDesign::Line] HoleAxis_26
  AttacherType = Attacher::AttachEngineLine
  Length = 4.50902
  MapMode = 19
  Placement = pos=(104.933,-67,0) rot=(0,0,1;0rad)
  ResizeMode = 1
  Support = -> [Pcb_57a1]
FEATURE [PartDesign::Line] HoleAxis_27
  AttacherType = Attacher::AttachEngineLine
  Length = 4.50902
  MapMode = 19
  Placement = pos=(116.6,-67,0) rot=(0,0,1;0rad)
  ResizeMode = 1
  Support = -> [Pcb_57a1]
FEATURE [PartDesign::Line] HoleAxis_28
  AttacherType = Attacher::AttachEngineLine
  Length = 4.50902
  MapMode = 19
  Placement = pos=(3.4,-67,0) rot=(0,0,1;0rad)
  ResizeMode = 1
  Support = -> [Pcb_57a1]
FEATURE [App::Part] Part
  Group = -> [LCS_0,Rsn108_R_1210_3225Metric_607492AA_ln_004,Rsn108_R_1210_3225Metric_607492AA_ln_003,Rsn108_R_1210_3225Metric_607492AA_ln_001,R117_R_0603_1608Metric_606C02F8_ln_017,Rsn108_R_1210_3225Metric_607492AA_ln_006,R117_R_0603_1608Metric_606C02F8_ln_018,R117_R_0603_1608Metric_606C02F8_ln_019,C134_C_0603_1608Metric_606C0308_ln_003,C134_C_0603_1608Metric_606C0308_ln_004,Dsn108_D_SOD_123F_6074702B_ln_021,+129 more]
  Origin = -> Origin
